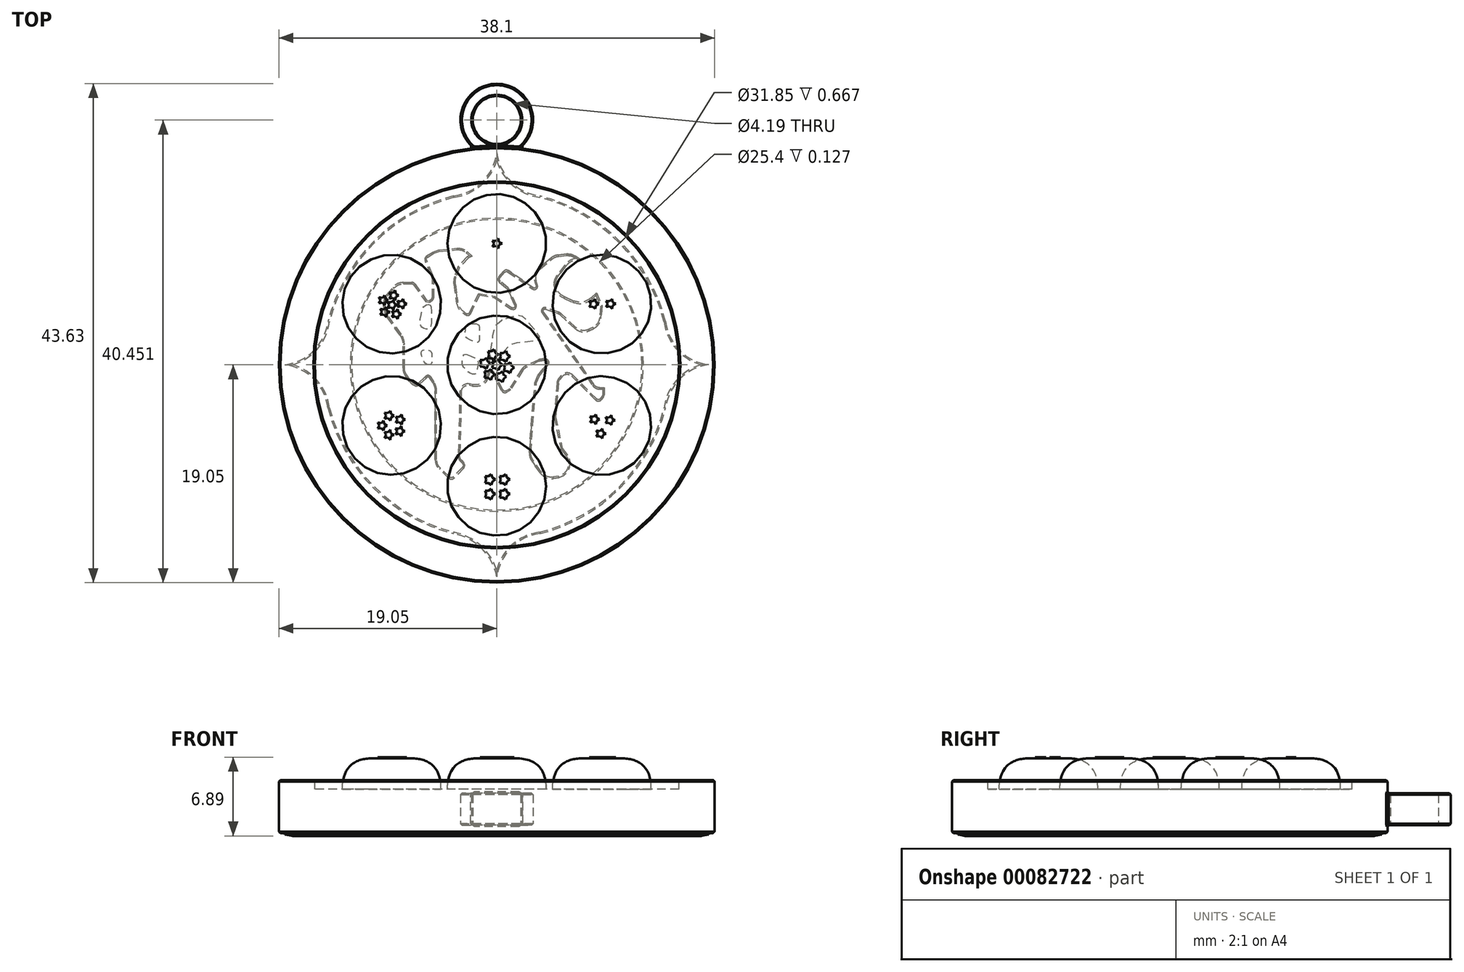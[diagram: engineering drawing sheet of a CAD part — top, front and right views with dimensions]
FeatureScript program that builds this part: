
annotation { "Feature Type Name" : "Feature", "Feature Type Description" : "" }
export const myFeature = defineFeature(function(context is Context, id is Id, definition is map)
    precondition{}
    {
        {
            var Q0;
            Q0=qCreatedBy(makeId("Top.planeOp"),FACE);
            var sketch = newSketch(context, id + "F0", { "sketchPlane" : qUnion([Q0])});
            skCircle(sketch, "E0", {"center": v(0, 0) * mm, "radius": 19.05 * mm});
            skCircle(sketch, "E1", {"center": v(0, 0) * mm, "radius": 15.92 * mm});
            skSolve(sketch);
        }
        {
            var Q0;
            Q0=qSketchRegion(id+"F0",true);
            var Q1;
            Q1=makeQuery(id+"F0.imprint","IMPRINT",FACE,{"disambiguationData":[TD([[makeQuery(id+"F0.imprint","IMPRINT",EDGE,{"derivedFrom":sQuery(id+"F0.wireOp",EDGE,"E1")}),1.0]])]});
            extrude(context, id + "F35", {"entities" : qUnion([Q0, Q1]), "oppositeDirection" : true, "depth" : 4.64 * mm});
        }
        {
            var Q0;
            Q0=makeQuery(id+"F0.imprint","IMPRINT",FACE,{"disambiguationData":[TD([[makeQuery(id+"F0.imprint","IMPRINT",EDGE,{"derivedFrom":sQuery(id+"F0.wireOp",EDGE,"E1")}),1.0]])]});
            extrude(context, id + "F36", {"entities" : qUnion([Q0]), "operationType" : NewBodyOperationType.REMOVE, "endBound" : BoundingType.SYMMETRIC, "oppositeDirection" : true, "depth" : 1.59 * mm});
        }
        {
            var Q0;
            Q0=qCreatedBy(makeId("Right.planeOp"),FACE);
            var sketch = newSketch(context, id + "F1", { "sketchPlane" : qUnion([Q0])});
            skLineSegment(sketch, "E2", {"start": v(0, -11.88) * mm, "end": v(0, 15.36) * mm});
            skLineSegment(sketch, "E3", {"start": v(14.05, 15.36) * mm, "end": v(14.05, -11.88) * mm});
            skSolve(sketch);
        }
        {
            var Q0;
            Q0=makeQuery(id+"F36.boolean.opBoolean","COPY",FACE,{"derivedFrom":makeQuery(id+"F36.opExtrude","CAP_FACE",FACE,{"disambiguationData":[OSD([sQuery(id+"F0.wireOp",EDGE,"E1")])],"isStart":false})});
            var sketch = newSketch(context, id + "F2", { "sketchPlane" : qUnion([Q0])});
            skCircle(sketch, "E4", {"center": v(0, 0) * mm, "radius": 4.32 * mm});
            skCircle(sketch, "E5", {"center": v(0, -10.61) * mm, "radius": 4.32 * mm});
            skSolve(sketch);
        }
        {
            var Q0;
            Q0=makeQuery(id+"F2.imprint","IMPRINT",FACE,{"disambiguationData":[TD([[makeQuery(id+"F2.imprint","IMPRINT",EDGE,{"derivedFrom":sQuery(id+"F2.wireOp",EDGE,"E5")}),1.0]])]});
            var Q1;
            Q1=sQuery(id+"F2.wireOp",EDGE,"E5");
            extrude(context, id + "F3", {"entities" : qUnion([Q0]), "surfaceEntities" : qUnion([Q1]), "depth" : 2.7 * mm});
        }
        {
            var Q0;
            Q0=makeQuery(id+"F3.opExtrude","SWEPT_BODY",BODY,{"disambiguationData":[OSD([sQuery(id+"F2.wireOp",EDGE,"E5")])]});
            var Q1;
            Q1=sQuery(id+"F1.wireOp",EDGE,"E2");
            circularPattern(context, id + "F4", {"entities" : qUnion([Q0]), "axis" : qUnion([Q1]), "angle" : 360 * degree, "instanceCount" : 6, "equalSpace" : true});
        }
        {
            var Q0;
            Q0=makeQuery(id+"F2.imprint","IMPRINT",FACE,{"disambiguationData":[TD([[makeQuery(id+"F2.imprint","IMPRINT",EDGE,{"derivedFrom":sQuery(id+"F2.wireOp",EDGE,"E4")}),1.0]])]});
            var Q1;
            Q1=sQuery(id+"F2.wireOp",EDGE,"E4");
            extrude(context, id + "F5", {"entities" : qUnion([Q0]), "surfaceEntities" : qUnion([Q1]), "depth" : 2.7 * mm});
        }
        {
            var Q0;
            Q0=qCreatedBy(makeId("Top.planeOp"),FACE);
            cPlane(context, id + "F6", {"entities" : qUnion([Q0]), "cplaneType" : CPlaneType.OFFSET, "offset" : 2.54 * mm, "oppositeDirection" : true, "width" : 152.4 * mm, "height" : 152.4 * mm});
        }
        {
            var Q0;
            Q0=qCreatedBy(id+"F6.planeOp",FACE);
            var sketch = newSketch(context, id + "F7", { "sketchPlane" : qUnion([Q0])});
            skCircle(sketch, "E6", {"center": v(0, 21.4) * mm, "radius": 3.18 * mm});
            skCircle(sketch, "E7", {"center": v(0, 21.4) * mm, "radius": 2.1 * mm});
            skSolve(sketch);
        }
        {
            var Q0;
            Q0=makeQuery(id+"F7.imprint","IMPRINT",FACE,{"disambiguationData":[TD([[makeQuery(id+"F7.imprint","IMPRINT",EDGE,{"derivedFrom":sQuery(id+"F7.wireOp",EDGE,"E6")}),1.0]])]});
            extrude(context, id + "F8", {"entities" : qUnion([Q0]), "operationType" : NewBodyOperationType.ADD, "endBound" : BoundingType.SYMMETRIC, "depth" : 2.8 * mm});
        }
        {
            var Q0;
            Q0=makeQuery(id+"F5.opExtrude","CAP_FACE",FACE,{"disambiguationData":[OSD([sQuery(id+"F2.wireOp",EDGE,"E4")])],"isStart":false});
            var sketch = newSketch(context, id + "F9", { "sketchPlane" : qUnion([Q0])});
            skCircle(sketch, "E8.cCircle", {"center": v(0, 0) * mm, "radius": 0.25 * mm, "construction": true});
            skLineSegment(sketch, "E8.0", {"start": v(-0.1, 0.3) * mm, "end": v(0.25, 0.18) * mm});
            skLineSegment(sketch, "E8.1", {"start": v(0.25, 0.18) * mm, "end": v(0.25, -0.18) * mm});
            skLineSegment(sketch, "E8.2", {"start": v(0.25, -0.18) * mm, "end": v(-0.1, -0.3) * mm});
            skLineSegment(sketch, "E8.3", {"start": v(-0.1, -0.3) * mm, "end": v(-0.31, 0) * mm});
            skLineSegment(sketch, "E8.4", {"start": v(-0.31, 0) * mm, "end": v(-0.1, 0.3) * mm});
            skPoint(sketch, "E8.0.midPoint", {"position": v(0.08, 0.24) * mm});
            skLineSegment(sketch, "E9", {"start": v(-0.1, 0.3) * mm, "end": v(0.15, 0.47) * mm});
            skLineSegment(sketch, "E10", {"start": v(0.15, 0.47) * mm, "end": v(0.25, 0.18) * mm});
            skLineSegment(sketch, "E11", {"start": v(0.25, 0.18) * mm, "end": v(0.5, 0) * mm});
            skPoint(sketch, "E11.endSnap0", {"position": v(0.25, 0) * mm});
            skLineSegment(sketch, "E12", {"start": v(0.5, 0) * mm, "end": v(0.25, -0.18) * mm});
            skLineSegment(sketch, "E13", {"start": v(-0.1, -0.3) * mm, "end": v(0.15, -0.47) * mm});
            skLineSegment(sketch, "E14", {"start": v(0.15, -0.47) * mm, "end": v(0.25, -0.18) * mm});
            skLineSegment(sketch, "E15", {"start": v(-0.31, 0) * mm, "end": v(-0.4, -0.3) * mm});
            skLineSegment(sketch, "E16", {"start": v(-0.4, -0.3) * mm, "end": v(-0.1, -0.3) * mm});
            skLineSegment(sketch, "E17", {"start": v(-0.31, 0) * mm, "end": v(-0.4, 0.3) * mm});
            skLineSegment(sketch, "E18", {"start": v(-0.4, 0.3) * mm, "end": v(-0.1, 0.3) * mm});
            skSolve(sketch);
        }
        {
            var Q0;
            Q0=makeQuery(id+"F9.imprint","IMPRINT",FACE,{"disambiguationData":[TD([[makeQuery(id+"F9.imprint","IMPRINT",EDGE,{"derivedFrom":sQuery(id+"F9.wireOp",EDGE,"E8.2")}),1.0]])]});
            var Q1;
            Q1=makeQuery(id+"F9.imprint","IMPRINT",FACE,{"disambiguationData":[TD([[makeQuery(id+"F9.imprint","IMPRINT",EDGE,{"derivedFrom":sQuery(id+"F9.wireOp",EDGE,"E8.3")}),1.0]])]});
            var Q2;
            Q2=makeQuery(id+"F9.imprint","IMPRINT",FACE,{"disambiguationData":[TD([[makeQuery(id+"F9.imprint","IMPRINT",EDGE,{"derivedFrom":sQuery(id+"F9.wireOp",EDGE,"E8.4")}),1.0]])]});
            var Q3;
            Q3=makeQuery(id+"F9.imprint","IMPRINT",FACE,{"disambiguationData":[TD([[makeQuery(id+"F9.imprint","IMPRINT",EDGE,{"derivedFrom":sQuery(id+"F9.wireOp",EDGE,"E8.0")}),1.0]])]});
            var Q4;
            Q4=makeQuery(id+"F9.imprint","IMPRINT",FACE,{"disambiguationData":[TD([[makeQuery(id+"F9.imprint","IMPRINT",EDGE,{"derivedFrom":sQuery(id+"F9.wireOp",EDGE,"E8.1")}),1.0]])]});
            var Q5;
            Q5=makeQuery(id+"F9.imprint","IMPRINT",FACE,{"disambiguationData":[TD([[makeQuery(id+"F9.imprint","IMPRINT",EDGE,{"derivedFrom":sQuery(id+"F9.wireOp",EDGE,"E8.0")}),-1.0]])]});
            var Q6;
            Q6=makeQuery(id+"F9.imprint","IMPRINT",FACE,{"disambiguationData":[TD([[makeQuery(id+"F9.imprint","IMPRINT",EDGE,{"derivedFrom":sQuery(id+"F9.wireOp",EDGE,"8882a5f5-dcc6-42d5-bc90-ea677534a3c9.0")}),1.0]])]});
            var Q7;
            Q7=makeQuery(id+"F9.imprint","IMPRINT",FACE,{"disambiguationData":[TD([[makeQuery(id+"F9.imprint","IMPRINT",EDGE,{"derivedFrom":sQuery(id+"F9.wireOp",EDGE,"8882a5f5-dcc6-42d5-bc90-ea677534a3c9.4")}),1.0]])]});
            var Q8;
            Q8=makeQuery(id+"F9.imprint","IMPRINT",FACE,{"disambiguationData":[TD([[makeQuery(id+"F9.imprint","IMPRINT",EDGE,{"derivedFrom":sQuery(id+"F9.wireOp",EDGE,"8882a5f5-dcc6-42d5-bc90-ea677534a3c9.3")}),1.0]])]});
            var Q9;
            Q9=makeQuery(id+"F9.imprint","IMPRINT",FACE,{"disambiguationData":[TD([[makeQuery(id+"F9.imprint","IMPRINT",EDGE,{"derivedFrom":sQuery(id+"F9.wireOp",EDGE,"8882a5f5-dcc6-42d5-bc90-ea677534a3c9.2")}),1.0]])]});
            var Q10;
            Q10=makeQuery(id+"F9.imprint","IMPRINT",FACE,{"disambiguationData":[TD([[makeQuery(id+"F9.imprint","IMPRINT",EDGE,{"derivedFrom":sQuery(id+"F9.wireOp",EDGE,"8882a5f5-dcc6-42d5-bc90-ea677534a3c9.1")}),1.0]])]});
            var Q11;
            Q11=makeQuery(id+"F9.imprint","IMPRINT",FACE,{"disambiguationData":[TD([[makeQuery(id+"F9.imprint","IMPRINT",EDGE,{"derivedFrom":sQuery(id+"F9.wireOp",EDGE,"8882a5f5-dcc6-42d5-bc90-ea677534a3c9.0")}),-1.0]])]});
            extrude(context, id + "F10", {"entities" : qUnion([Q0, Q1, Q2, Q3, Q4, Q5, Q6, Q7, Q8, Q9, Q10, Q11]), "operationType" : NewBodyOperationType.ADD, "depth" : 0.1 * mm});
        }
        {
            var Q0;
            Q0=qCreatedBy(makeId("Right.planeOp"),FACE);
            cPlane(context, id + "F11", {"entities" : qUnion([Q0]), "cplaneType" : CPlaneType.OFFSET, "offset" : 12.45 * mm, "oppositeDirection" : true, "width" : 152.4 * mm, "height" : 152.4 * mm});
        }
        {
            var Q0;
            Q0=qCreatedBy(makeId("Right.planeOp"),FACE);
            cPlane(context, id + "F12", {"entities" : qUnion([Q0]), "cplaneType" : CPlaneType.OFFSET, "offset" : 12.45 * mm, "width" : 152.4 * mm, "height" : 152.4 * mm});
        }
        {
            var Q0;
            Q0=makeQuery(id+"F5.opExtrude","CAP_EDGE",EDGE,{"disambiguationData":[OSD([sQuery(id+"F2.wireOp",EDGE,"E4")])],"isStart":false});
            var Q1;
            Q1=makeQuery(id+"F4.opPattern","COPY",EDGE,{"derivedFrom":makeQuery(id+"F3.opExtrude","CAP_EDGE",EDGE,{"disambiguationData":[OSD([sQuery(id+"F2.wireOp",EDGE,"E5")])],"isStart":false}),"instanceName":"3"});
            var Q2;
            Q2=makeQuery(id+"F4.opPattern","COPY",EDGE,{"derivedFrom":makeQuery(id+"F3.opExtrude","CAP_EDGE",EDGE,{"disambiguationData":[OSD([sQuery(id+"F2.wireOp",EDGE,"E5")])],"isStart":false}),"instanceName":"2"});
            var Q3;
            Q3=makeQuery(id+"F4.opPattern","COPY",EDGE,{"derivedFrom":makeQuery(id+"F3.opExtrude","CAP_EDGE",EDGE,{"disambiguationData":[OSD([sQuery(id+"F2.wireOp",EDGE,"E5")])],"isStart":false}),"instanceName":"1"});
            var Q4;
            Q4=makeQuery(id+"F4.opPattern","COPY",EDGE,{"derivedFrom":makeQuery(id+"F3.opExtrude","CAP_EDGE",EDGE,{"disambiguationData":[OSD([sQuery(id+"F2.wireOp",EDGE,"E5")])],"isStart":false}),"instanceName":"5"});
            var Q5;
            Q5=makeQuery(id+"F3.opExtrude","CAP_EDGE",EDGE,{"disambiguationData":[OSD([sQuery(id+"F2.wireOp",EDGE,"E5")])],"isStart":false});
            var Q6;
            Q6=makeQuery(id+"F4.opPattern","COPY",EDGE,{"derivedFrom":makeQuery(id+"F3.opExtrude","CAP_EDGE",EDGE,{"disambiguationData":[OSD([sQuery(id+"F2.wireOp",EDGE,"E5")])],"isStart":false}),"instanceName":"4"});
            fillet(context, id + "F13", {"entities" : qUnion([Q0, Q1, Q2, Q3, Q4, Q5, Q6]), "radius" : 2.7 * mm, "rho" : 0.5, "crossSection" : FilletCrossSection.CONIC, "allowEdgeOverflow" : false});
        }
        {
            var Q0;
            Q0=makeQuery(id+"F4.opPattern","COPY",FACE,{"derivedFrom":makeQuery(id+"F3.opExtrude","CAP_FACE",FACE,{"disambiguationData":[OSD([sQuery(id+"F2.wireOp",EDGE,"E5")])],"isStart":false}),"instanceName":"3"});
            var sketch = newSketch(context, id + "F14", { "sketchPlane" : qUnion([Q0])});
            skCircle(sketch, "E19.cCircle", {"center": v(0, 10.6) * mm, "radius": 0.19 * mm, "construction": true});
            skLineSegment(sketch, "E19.0", {"start": v(-0.07, 10.83) * mm, "end": v(0.19, 10.74) * mm});
            skLineSegment(sketch, "E19.1", {"start": v(0.19, 10.74) * mm, "end": v(0.19, 10.47) * mm});
            skLineSegment(sketch, "E19.2", {"start": v(0.19, 10.47) * mm, "end": v(-0.07, 10.39) * mm});
            skLineSegment(sketch, "E19.3", {"start": v(-0.07, 10.39) * mm, "end": v(-0.23, 10.6) * mm});
            skLineSegment(sketch, "E19.4", {"start": v(-0.23, 10.6) * mm, "end": v(-0.07, 10.83) * mm});
            skPoint(sketch, "E19.0.midPoint", {"position": v(0.06, 10.78) * mm});
            skLineSegment(sketch, "E20", {"start": v(-0.07, 10.83) * mm, "end": v(0.14, 11.04) * mm});
            skLineSegment(sketch, "E21", {"start": v(0.14, 11.04) * mm, "end": v(0.19, 10.74) * mm});
            skLineSegment(sketch, "E22", {"start": v(0.19, 10.74) * mm, "end": v(0.46, 10.6) * mm});
            skPoint(sketch, "E22.endSnap0", {"position": v(0.19, 10.6) * mm});
            skLineSegment(sketch, "E23", {"start": v(0.46, 10.6) * mm, "end": v(0.19, 10.47) * mm});
            skLineSegment(sketch, "E24", {"start": v(-0.07, 10.39) * mm, "end": v(0.14, 10.17) * mm});
            skLineSegment(sketch, "E25", {"start": v(0.14, 10.17) * mm, "end": v(0.19, 10.47) * mm});
            skLineSegment(sketch, "E26", {"start": v(-0.23, 10.6) * mm, "end": v(-0.37, 10.34) * mm});
            skLineSegment(sketch, "E27", {"start": v(-0.37, 10.34) * mm, "end": v(-0.07, 10.39) * mm});
            skLineSegment(sketch, "E28", {"start": v(-0.23, 10.6) * mm, "end": v(-0.37, 10.88) * mm});
            skLineSegment(sketch, "E29", {"start": v(-0.37, 10.88) * mm, "end": v(-0.07, 10.83) * mm});
            skSolve(sketch);
        }
        {
            var Q0;
            Q0=makeQuery(id+"F4.opPattern","COPY",FACE,{"derivedFrom":makeQuery(id+"F3.opExtrude","CAP_FACE",FACE,{"disambiguationData":[OSD([sQuery(id+"F2.wireOp",EDGE,"E5")])],"isStart":false}),"instanceName":"2"});
            var sketch = newSketch(context, id + "F15", { "sketchPlane" : qUnion([Q0])});
            skCircle(sketch, "E30.cCircle", {"center": v(8.46, 5.32) * mm, "radius": 0.19 * mm, "construction": true});
            skLineSegment(sketch, "E30.0", {"start": v(8.4, 5.54) * mm, "end": v(8.65, 5.46) * mm});
            skLineSegment(sketch, "E30.1", {"start": v(8.65, 5.46) * mm, "end": v(8.65, 5.19) * mm});
            skLineSegment(sketch, "E30.2", {"start": v(8.65, 5.19) * mm, "end": v(8.4, 5.1) * mm});
            skLineSegment(sketch, "E30.3", {"start": v(8.4, 5.1) * mm, "end": v(8.23, 5.32) * mm});
            skLineSegment(sketch, "E30.4", {"start": v(8.23, 5.32) * mm, "end": v(8.4, 5.54) * mm});
            skPoint(sketch, "E30.0.midPoint", {"position": v(8.52, 5.5) * mm});
            skLineSegment(sketch, "E31", {"start": v(8.4, 5.54) * mm, "end": v(8.6, 5.76) * mm});
            skLineSegment(sketch, "E32", {"start": v(8.6, 5.76) * mm, "end": v(8.65, 5.46) * mm});
            skLineSegment(sketch, "E33", {"start": v(8.65, 5.46) * mm, "end": v(8.92, 5.32) * mm});
            skPoint(sketch, "E33.endSnap0", {"position": v(8.65, 5.32) * mm});
            skLineSegment(sketch, "E34", {"start": v(8.92, 5.32) * mm, "end": v(8.65, 5.19) * mm});
            skLineSegment(sketch, "E35", {"start": v(8.4, 5.1) * mm, "end": v(8.6, 4.88) * mm});
            skLineSegment(sketch, "E36", {"start": v(8.6, 4.88) * mm, "end": v(8.65, 5.19) * mm});
            skLineSegment(sketch, "E37", {"start": v(8.23, 5.32) * mm, "end": v(8.1, 5.05) * mm});
            skLineSegment(sketch, "E38", {"start": v(8.1, 5.05) * mm, "end": v(8.4, 5.1) * mm});
            skLineSegment(sketch, "E39", {"start": v(8.23, 5.32) * mm, "end": v(8.1, 5.6) * mm});
            skLineSegment(sketch, "E40", {"start": v(8.1, 5.6) * mm, "end": v(8.4, 5.54) * mm});
            skCircle(sketch, "E41.cCircle", {"center": v(9.94, 5.33) * mm, "radius": 0.19 * mm, "construction": true});
            skLineSegment(sketch, "E41.0", {"start": v(9.87, 5.55) * mm, "end": v(10.12, 5.47) * mm});
            skLineSegment(sketch, "E41.1", {"start": v(10.12, 5.47) * mm, "end": v(10.12, 5.2) * mm});
            skLineSegment(sketch, "E41.2", {"start": v(10.12, 5.2) * mm, "end": v(9.87, 5.11) * mm});
            skLineSegment(sketch, "E41.3", {"start": v(9.87, 5.11) * mm, "end": v(9.7, 5.33) * mm});
            skLineSegment(sketch, "E41.4", {"start": v(9.7, 5.33) * mm, "end": v(9.87, 5.55) * mm});
            skPoint(sketch, "E41.0.midPoint", {"position": v(10, 5.5) * mm});
            skLineSegment(sketch, "E42", {"start": v(9.87, 5.55) * mm, "end": v(10.08, 5.77) * mm});
            skLineSegment(sketch, "E43", {"start": v(10.08, 5.77) * mm, "end": v(10.12, 5.47) * mm});
            skLineSegment(sketch, "E44", {"start": v(10.12, 5.47) * mm, "end": v(10.4, 5.33) * mm});
            skPoint(sketch, "E44.endSnap0", {"position": v(10.12, 5.33) * mm});
            skLineSegment(sketch, "E45", {"start": v(10.4, 5.33) * mm, "end": v(10.12, 5.2) * mm});
            skLineSegment(sketch, "E46", {"start": v(9.87, 5.11) * mm, "end": v(10.08, 4.9) * mm});
            skLineSegment(sketch, "E47", {"start": v(10.08, 4.9) * mm, "end": v(10.12, 5.2) * mm});
            skLineSegment(sketch, "E48", {"start": v(9.7, 5.33) * mm, "end": v(9.56, 5.06) * mm});
            skLineSegment(sketch, "E49", {"start": v(9.56, 5.06) * mm, "end": v(9.87, 5.11) * mm});
            skLineSegment(sketch, "E50", {"start": v(9.7, 5.33) * mm, "end": v(9.56, 5.6) * mm});
            skLineSegment(sketch, "E51", {"start": v(9.56, 5.6) * mm, "end": v(9.87, 5.55) * mm});
            skSolve(sketch);
        }
        {
            var Q0;
            Q0=makeQuery(id+"F4.opPattern","COPY",FACE,{"derivedFrom":makeQuery(id+"F3.opExtrude","CAP_FACE",FACE,{"disambiguationData":[OSD([sQuery(id+"F2.wireOp",EDGE,"E5")])],"isStart":false}),"instanceName":"1"});
            var sketch = newSketch(context, id + "F16", { "sketchPlane" : qUnion([Q0])});
            skCircle(sketch, "E52.cCircle", {"center": v(9.08, -6.01) * mm, "radius": 0.19 * mm, "construction": true});
            skLineSegment(sketch, "E52.0", {"start": v(9, -5.8) * mm, "end": v(9.27, -5.87) * mm});
            skLineSegment(sketch, "E52.1", {"start": v(9.27, -5.87) * mm, "end": v(9.27, -6.15) * mm});
            skLineSegment(sketch, "E52.2", {"start": v(9.27, -6.15) * mm, "end": v(9, -6.23) * mm});
            skLineSegment(sketch, "E52.3", {"start": v(9, -6.23) * mm, "end": v(8.85, -6.01) * mm});
            skLineSegment(sketch, "E52.4", {"start": v(8.85, -6.01) * mm, "end": v(9, -5.8) * mm});
            skPoint(sketch, "E52.0.midPoint", {"position": v(9.14, -5.83) * mm});
            skLineSegment(sketch, "E53", {"start": v(9, -5.8) * mm, "end": v(9.22, -5.57) * mm});
            skLineSegment(sketch, "E54", {"start": v(9.22, -5.57) * mm, "end": v(9.27, -5.87) * mm});
            skLineSegment(sketch, "E55", {"start": v(9.27, -5.87) * mm, "end": v(9.54, -6.01) * mm});
            skPoint(sketch, "E55.endSnap0", {"position": v(9.27, -6.01) * mm});
            skLineSegment(sketch, "E56", {"start": v(9.54, -6.01) * mm, "end": v(9.27, -6.15) * mm});
            skLineSegment(sketch, "E57", {"start": v(9, -6.23) * mm, "end": v(9.22, -6.45) * mm});
            skLineSegment(sketch, "E58", {"start": v(9.22, -6.45) * mm, "end": v(9.27, -6.15) * mm});
            skLineSegment(sketch, "E59", {"start": v(8.85, -6.01) * mm, "end": v(8.7, -6.28) * mm});
            skLineSegment(sketch, "E60", {"start": v(8.7, -6.28) * mm, "end": v(9, -6.23) * mm});
            skLineSegment(sketch, "E61", {"start": v(8.85, -6.01) * mm, "end": v(8.7, -5.74) * mm});
            skLineSegment(sketch, "E62", {"start": v(8.7, -5.74) * mm, "end": v(9, -5.8) * mm});
            skCircle(sketch, "E63.cCircle", {"center": v(8.54, -4.77) * mm, "radius": 0.19 * mm, "construction": true});
            skLineSegment(sketch, "E63.0", {"start": v(8.47, -4.55) * mm, "end": v(8.72, -4.63) * mm});
            skLineSegment(sketch, "E63.1", {"start": v(8.72, -4.63) * mm, "end": v(8.72, -4.9) * mm});
            skLineSegment(sketch, "E63.2", {"start": v(8.72, -4.9) * mm, "end": v(8.47, -4.99) * mm});
            skLineSegment(sketch, "E63.3", {"start": v(8.47, -4.99) * mm, "end": v(8.3, -4.77) * mm});
            skLineSegment(sketch, "E63.4", {"start": v(8.3, -4.77) * mm, "end": v(8.47, -4.55) * mm});
            skPoint(sketch, "E63.0.midPoint", {"position": v(8.6, -4.59) * mm});
            skLineSegment(sketch, "E64", {"start": v(8.47, -4.55) * mm, "end": v(8.68, -4.33) * mm});
            skLineSegment(sketch, "E65", {"start": v(8.68, -4.33) * mm, "end": v(8.72, -4.63) * mm});
            skLineSegment(sketch, "E66", {"start": v(8.72, -4.63) * mm, "end": v(9, -4.77) * mm});
            skPoint(sketch, "E66.endSnap0", {"position": v(8.72, -4.77) * mm});
            skLineSegment(sketch, "E67", {"start": v(9, -4.77) * mm, "end": v(8.72, -4.9) * mm});
            skLineSegment(sketch, "E68", {"start": v(8.47, -4.99) * mm, "end": v(8.68, -5.2) * mm});
            skLineSegment(sketch, "E69", {"start": v(8.68, -5.2) * mm, "end": v(8.72, -4.9) * mm});
            skLineSegment(sketch, "E70", {"start": v(8.3, -4.77) * mm, "end": v(8.17, -5.04) * mm});
            skLineSegment(sketch, "E71", {"start": v(8.17, -5.04) * mm, "end": v(8.47, -4.99) * mm});
            skLineSegment(sketch, "E72", {"start": v(8.3, -4.77) * mm, "end": v(8.17, -4.5) * mm});
            skLineSegment(sketch, "E73", {"start": v(8.17, -4.5) * mm, "end": v(8.47, -4.55) * mm});
            skCircle(sketch, "E74.cCircle", {"center": v(9.88, -4.84) * mm, "radius": 0.19 * mm, "construction": true});
            skLineSegment(sketch, "E74.0", {"start": v(9.8, -4.62) * mm, "end": v(10.07, -4.7) * mm});
            skLineSegment(sketch, "E74.1", {"start": v(10.07, -4.7) * mm, "end": v(10.07, -4.97) * mm});
            skLineSegment(sketch, "E74.2", {"start": v(10.07, -4.97) * mm, "end": v(9.8, -5.06) * mm});
            skLineSegment(sketch, "E74.3", {"start": v(9.8, -5.06) * mm, "end": v(9.65, -4.84) * mm});
            skLineSegment(sketch, "E74.4", {"start": v(9.65, -4.84) * mm, "end": v(9.8, -4.62) * mm});
            skPoint(sketch, "E74.0.midPoint", {"position": v(9.94, -4.66) * mm});
            skLineSegment(sketch, "E75", {"start": v(9.8, -4.62) * mm, "end": v(10.02, -4.4) * mm});
            skLineSegment(sketch, "E76", {"start": v(10.02, -4.4) * mm, "end": v(10.07, -4.7) * mm});
            skLineSegment(sketch, "E77", {"start": v(10.07, -4.7) * mm, "end": v(10.34, -4.84) * mm});
            skPoint(sketch, "E77.endSnap0", {"position": v(10.07, -4.84) * mm});
            skLineSegment(sketch, "E78", {"start": v(10.34, -4.84) * mm, "end": v(10.07, -4.97) * mm});
            skLineSegment(sketch, "E79", {"start": v(9.8, -5.06) * mm, "end": v(10.02, -5.28) * mm});
            skLineSegment(sketch, "E80", {"start": v(10.02, -5.28) * mm, "end": v(10.07, -4.97) * mm});
            skLineSegment(sketch, "E81", {"start": v(9.65, -4.84) * mm, "end": v(9.5, -5.1) * mm});
            skLineSegment(sketch, "E82", {"start": v(9.5, -5.1) * mm, "end": v(9.8, -5.06) * mm});
            skLineSegment(sketch, "E83", {"start": v(9.65, -4.84) * mm, "end": v(9.5, -4.57) * mm});
            skLineSegment(sketch, "E84", {"start": v(9.5, -4.57) * mm, "end": v(9.8, -4.62) * mm});
            skSolve(sketch);
        }
        {
            var Q0;
            Q0=makeQuery(id+"F3.opExtrude","CAP_FACE",FACE,{"disambiguationData":[OSD([sQuery(id+"F2.wireOp",EDGE,"E5")])],"isStart":false});
            var sketch = newSketch(context, id + "F17", { "sketchPlane" : qUnion([Q0])});
            skLineSegment(sketch, "E85.bottom", {"start": v(-0.62, -10.04) * mm, "end": v(0.65, -10.04) * mm});
            skLineSegment(sketch, "E85.top", {"start": v(-0.62, -11.3) * mm, "end": v(0.65, -11.3) * mm});
            skLineSegment(sketch, "E85.left", {"start": v(-0.62, -10.04) * mm, "end": v(-0.62, -11.3) * mm});
            skLineSegment(sketch, "E85.right", {"start": v(0.65, -10.04) * mm, "end": v(0.65, -11.3) * mm});
            skPoint(sketch, "E85.middle", {"position": v(0.01, -10.67) * mm});
            skCircle(sketch, "E86.cCircle", {"center": v(0.65, -10.04) * mm, "radius": 0.25 * mm, "construction": true});
            skLineSegment(sketch, "E86.0", {"start": v(0.55, -9.74) * mm, "end": v(0.9, -9.85) * mm});
            skLineSegment(sketch, "E86.1", {"start": v(0.9, -9.85) * mm, "end": v(0.9, -10.22) * mm});
            skLineSegment(sketch, "E86.2", {"start": v(0.9, -10.22) * mm, "end": v(0.55, -10.33) * mm});
            skLineSegment(sketch, "E86.3", {"start": v(0.55, -10.33) * mm, "end": v(0.34, -10.04) * mm});
            skLineSegment(sketch, "E86.4", {"start": v(0.34, -10.04) * mm, "end": v(0.55, -9.74) * mm});
            skPoint(sketch, "E86.0.midPoint", {"position": v(0.73, -9.8) * mm});
            skLineSegment(sketch, "E87", {"start": v(0.55, -9.74) * mm, "end": v(0.8, -9.56) * mm});
            skLineSegment(sketch, "E88", {"start": v(0.8, -9.56) * mm, "end": v(0.9, -9.85) * mm});
            skLineSegment(sketch, "E89", {"start": v(0.9, -9.85) * mm, "end": v(1.15, -10.04) * mm});
            skPoint(sketch, "E89.endSnap0", {"position": v(0.9, -10.04) * mm});
            skLineSegment(sketch, "E90", {"start": v(1.15, -10.04) * mm, "end": v(0.9, -10.22) * mm});
            skLineSegment(sketch, "E91", {"start": v(0.55, -10.33) * mm, "end": v(0.8, -10.5) * mm});
            skLineSegment(sketch, "E92", {"start": v(0.8, -10.5) * mm, "end": v(0.9, -10.22) * mm});
            skLineSegment(sketch, "E93", {"start": v(0.34, -10.04) * mm, "end": v(0.25, -10.33) * mm});
            skLineSegment(sketch, "E94", {"start": v(0.25, -10.33) * mm, "end": v(0.55, -10.33) * mm});
            skLineSegment(sketch, "E95", {"start": v(0.34, -10.04) * mm, "end": v(0.25, -9.74) * mm});
            skLineSegment(sketch, "E96", {"start": v(0.25, -9.74) * mm, "end": v(0.55, -9.74) * mm});
            skCircle(sketch, "E97.cCircle", {"center": v(-0.62, -10.04) * mm, "radius": 0.25 * mm, "construction": true});
            skLineSegment(sketch, "E97.0", {"start": v(-0.72, -9.74) * mm, "end": v(-0.37, -9.85) * mm});
            skLineSegment(sketch, "E97.1", {"start": v(-0.37, -9.85) * mm, "end": v(-0.37, -10.22) * mm});
            skLineSegment(sketch, "E97.2", {"start": v(-0.37, -10.22) * mm, "end": v(-0.72, -10.33) * mm});
            skLineSegment(sketch, "E97.3", {"start": v(-0.72, -10.33) * mm, "end": v(-0.93, -10.04) * mm});
            skLineSegment(sketch, "E97.4", {"start": v(-0.93, -10.04) * mm, "end": v(-0.72, -9.74) * mm});
            skPoint(sketch, "E97.0.midPoint", {"position": v(-0.54, -9.8) * mm});
            skLineSegment(sketch, "E98", {"start": v(-0.72, -9.74) * mm, "end": v(-0.47, -9.56) * mm});
            skLineSegment(sketch, "E99", {"start": v(-0.47, -9.56) * mm, "end": v(-0.37, -9.85) * mm});
            skLineSegment(sketch, "E100", {"start": v(-0.37, -9.85) * mm, "end": v(-0.12, -10.04) * mm});
            skPoint(sketch, "E100.endSnap0", {"position": v(-0.37, -10.04) * mm});
            skLineSegment(sketch, "E101", {"start": v(-0.12, -10.04) * mm, "end": v(-0.37, -10.22) * mm});
            skLineSegment(sketch, "E102", {"start": v(-0.72, -10.33) * mm, "end": v(-0.47, -10.5) * mm});
            skLineSegment(sketch, "E103", {"start": v(-0.47, -10.5) * mm, "end": v(-0.37, -10.22) * mm});
            skLineSegment(sketch, "E104", {"start": v(-0.93, -10.04) * mm, "end": v(-1.02, -10.33) * mm});
            skLineSegment(sketch, "E105", {"start": v(-1.02, -10.33) * mm, "end": v(-0.72, -10.33) * mm});
            skLineSegment(sketch, "E106", {"start": v(-0.93, -10.04) * mm, "end": v(-1.02, -9.74) * mm});
            skLineSegment(sketch, "E107", {"start": v(-1.02, -9.74) * mm, "end": v(-0.72, -9.74) * mm});
            skCircle(sketch, "E108.cCircle", {"center": v(-0.62, -11.3) * mm, "radius": 0.25 * mm, "construction": true});
            skLineSegment(sketch, "E108.0", {"start": v(-0.72, -11.01) * mm, "end": v(-0.37, -11.12) * mm});
            skLineSegment(sketch, "E108.1", {"start": v(-0.37, -11.12) * mm, "end": v(-0.37, -11.49) * mm});
            skLineSegment(sketch, "E108.2", {"start": v(-0.37, -11.49) * mm, "end": v(-0.72, -11.6) * mm});
            skLineSegment(sketch, "E108.3", {"start": v(-0.72, -11.6) * mm, "end": v(-0.93, -11.3) * mm});
            skLineSegment(sketch, "E108.4", {"start": v(-0.93, -11.3) * mm, "end": v(-0.72, -11.01) * mm});
            skPoint(sketch, "E108.0.midPoint", {"position": v(-0.54, -11.07) * mm});
            skLineSegment(sketch, "E109", {"start": v(-0.72, -11.01) * mm, "end": v(-0.47, -10.83) * mm});
            skLineSegment(sketch, "E110", {"start": v(-0.47, -10.83) * mm, "end": v(-0.37, -11.12) * mm});
            skLineSegment(sketch, "E111", {"start": v(-0.37, -11.12) * mm, "end": v(-0.12, -11.3) * mm});
            skPoint(sketch, "E111.endSnap0", {"position": v(-0.37, -11.3) * mm});
            skLineSegment(sketch, "E112", {"start": v(-0.12, -11.3) * mm, "end": v(-0.37, -11.49) * mm});
            skLineSegment(sketch, "E113", {"start": v(-0.72, -11.6) * mm, "end": v(-0.47, -11.78) * mm});
            skLineSegment(sketch, "E114", {"start": v(-0.47, -11.78) * mm, "end": v(-0.37, -11.49) * mm});
            skLineSegment(sketch, "E115", {"start": v(-0.93, -11.3) * mm, "end": v(-1.02, -11.6) * mm});
            skLineSegment(sketch, "E116", {"start": v(-1.02, -11.6) * mm, "end": v(-0.72, -11.6) * mm});
            skLineSegment(sketch, "E117", {"start": v(-0.93, -11.3) * mm, "end": v(-1.02, -11.01) * mm});
            skLineSegment(sketch, "E118", {"start": v(-1.02, -11.01) * mm, "end": v(-0.72, -11.01) * mm});
            skCircle(sketch, "E119.cCircle", {"center": v(0.65, -11.3) * mm, "radius": 0.25 * mm, "construction": true});
            skLineSegment(sketch, "E119.0", {"start": v(0.55, -11.01) * mm, "end": v(0.9, -11.12) * mm});
            skLineSegment(sketch, "E119.1", {"start": v(0.9, -11.12) * mm, "end": v(0.9, -11.49) * mm});
            skLineSegment(sketch, "E119.2", {"start": v(0.9, -11.49) * mm, "end": v(0.55, -11.6) * mm});
            skLineSegment(sketch, "E119.3", {"start": v(0.55, -11.6) * mm, "end": v(0.34, -11.3) * mm});
            skLineSegment(sketch, "E119.4", {"start": v(0.34, -11.3) * mm, "end": v(0.55, -11.01) * mm});
            skPoint(sketch, "E119.0.midPoint", {"position": v(0.73, -11.07) * mm});
            skLineSegment(sketch, "E120", {"start": v(0.55, -11.01) * mm, "end": v(0.8, -10.83) * mm});
            skLineSegment(sketch, "E121", {"start": v(0.8, -10.83) * mm, "end": v(0.9, -11.12) * mm});
            skLineSegment(sketch, "E122", {"start": v(0.9, -11.12) * mm, "end": v(1.15, -11.3) * mm});
            skPoint(sketch, "E122.endSnap0", {"position": v(0.9, -11.3) * mm});
            skLineSegment(sketch, "E123", {"start": v(1.15, -11.3) * mm, "end": v(0.9, -11.49) * mm});
            skLineSegment(sketch, "E124", {"start": v(0.55, -11.6) * mm, "end": v(0.8, -11.78) * mm});
            skLineSegment(sketch, "E125", {"start": v(0.8, -11.78) * mm, "end": v(0.9, -11.49) * mm});
            skLineSegment(sketch, "E126", {"start": v(0.34, -11.3) * mm, "end": v(0.25, -11.6) * mm});
            skLineSegment(sketch, "E127", {"start": v(0.25, -11.6) * mm, "end": v(0.55, -11.6) * mm});
            skLineSegment(sketch, "E128", {"start": v(0.34, -11.3) * mm, "end": v(0.25, -11.01) * mm});
            skLineSegment(sketch, "E129", {"start": v(0.25, -11.01) * mm, "end": v(0.55, -11.01) * mm});
            skSolve(sketch);
        }
        {
            var Q0;
            Q0=makeQuery(id+"F4.opPattern","COPY",FACE,{"derivedFrom":makeQuery(id+"F3.opExtrude","CAP_FACE",FACE,{"disambiguationData":[OSD([sQuery(id+"F2.wireOp",EDGE,"E5")])],"isStart":false}),"instanceName":"5"});
            var sketch = newSketch(context, id + "F18", { "sketchPlane" : qUnion([Q0])});
            skCircle(sketch, "E130.cCircle", {"center": v(-9.17, -5.27) * mm, "radius": 0.7 * mm, "construction": true});
            skLineSegment(sketch, "E130.0", {"start": v(-8.47, -4.76) * mm, "end": v(-8.47, -5.78) * mm});
            skLineSegment(sketch, "E130.1", {"start": v(-8.47, -5.78) * mm, "end": v(-9.44, -6.1) * mm});
            skLineSegment(sketch, "E130.2", {"start": v(-9.44, -6.1) * mm, "end": v(-10.04, -5.27) * mm});
            skLineSegment(sketch, "E130.3", {"start": v(-10.04, -5.27) * mm, "end": v(-9.44, -4.45) * mm});
            skLineSegment(sketch, "E130.4", {"start": v(-9.44, -4.45) * mm, "end": v(-8.47, -4.76) * mm});
            skPoint(sketch, "E130.0.midPoint", {"position": v(-8.47, -5.27) * mm});
            skCircle(sketch, "E131.cCircle", {"center": v(-9.44, -4.45) * mm, "radius": 0.19 * mm, "construction": true});
            skLineSegment(sketch, "E131.0", {"start": v(-9.51, -4.23) * mm, "end": v(-9.25, -4.31) * mm});
            skLineSegment(sketch, "E131.1", {"start": v(-9.25, -4.31) * mm, "end": v(-9.25, -4.58) * mm});
            skLineSegment(sketch, "E131.2", {"start": v(-9.25, -4.58) * mm, "end": v(-9.51, -4.67) * mm});
            skLineSegment(sketch, "E131.3", {"start": v(-9.51, -4.67) * mm, "end": v(-9.67, -4.45) * mm});
            skLineSegment(sketch, "E131.4", {"start": v(-9.67, -4.45) * mm, "end": v(-9.51, -4.23) * mm});
            skPoint(sketch, "E131.0.midPoint", {"position": v(-9.38, -4.27) * mm});
            skLineSegment(sketch, "E132", {"start": v(-9.51, -4.23) * mm, "end": v(-9.3, -4.01) * mm});
            skLineSegment(sketch, "E133", {"start": v(-9.3, -4.01) * mm, "end": v(-9.25, -4.31) * mm});
            skLineSegment(sketch, "E134", {"start": v(-9.25, -4.31) * mm, "end": v(-8.98, -4.45) * mm});
            skPoint(sketch, "E134.endSnap0", {"position": v(-9.25, -4.45) * mm});
            skLineSegment(sketch, "E135", {"start": v(-8.98, -4.45) * mm, "end": v(-9.25, -4.58) * mm});
            skLineSegment(sketch, "E136", {"start": v(-9.51, -4.67) * mm, "end": v(-9.3, -4.89) * mm});
            skLineSegment(sketch, "E137", {"start": v(-9.3, -4.89) * mm, "end": v(-9.25, -4.58) * mm});
            skLineSegment(sketch, "E138", {"start": v(-9.67, -4.45) * mm, "end": v(-9.81, -4.72) * mm});
            skLineSegment(sketch, "E139", {"start": v(-9.81, -4.72) * mm, "end": v(-9.51, -4.67) * mm});
            skLineSegment(sketch, "E140", {"start": v(-9.67, -4.45) * mm, "end": v(-9.81, -4.18) * mm});
            skLineSegment(sketch, "E141", {"start": v(-9.81, -4.18) * mm, "end": v(-9.51, -4.23) * mm});
            skCircle(sketch, "E142.cCircle", {"center": v(-8.46, -4.79) * mm, "radius": 0.19 * mm, "construction": true});
            skLineSegment(sketch, "E142.0", {"start": v(-8.53, -4.57) * mm, "end": v(-8.27, -4.65) * mm});
            skLineSegment(sketch, "E142.1", {"start": v(-8.27, -4.65) * mm, "end": v(-8.27, -4.92) * mm});
            skLineSegment(sketch, "E142.2", {"start": v(-8.27, -4.92) * mm, "end": v(-8.53, -5) * mm});
            skLineSegment(sketch, "E142.3", {"start": v(-8.53, -5) * mm, "end": v(-8.69, -4.79) * mm});
            skLineSegment(sketch, "E142.4", {"start": v(-8.69, -4.79) * mm, "end": v(-8.53, -4.57) * mm});
            skPoint(sketch, "E142.0.midPoint", {"position": v(-8.4, -4.61) * mm});
            skLineSegment(sketch, "E143", {"start": v(-8.53, -4.57) * mm, "end": v(-8.32, -4.35) * mm});
            skLineSegment(sketch, "E144", {"start": v(-8.32, -4.35) * mm, "end": v(-8.27, -4.65) * mm});
            skLineSegment(sketch, "E145", {"start": v(-8.27, -4.65) * mm, "end": v(-8, -4.79) * mm});
            skPoint(sketch, "E145.endSnap0", {"position": v(-8.27, -4.79) * mm});
            skLineSegment(sketch, "E146", {"start": v(-8, -4.79) * mm, "end": v(-8.27, -4.92) * mm});
            skLineSegment(sketch, "E147", {"start": v(-8.53, -5) * mm, "end": v(-8.32, -5.22) * mm});
            skLineSegment(sketch, "E148", {"start": v(-8.32, -5.22) * mm, "end": v(-8.27, -4.92) * mm});
            skLineSegment(sketch, "E149", {"start": v(-8.69, -4.79) * mm, "end": v(-8.83, -5.06) * mm});
            skLineSegment(sketch, "E150", {"start": v(-8.83, -5.06) * mm, "end": v(-8.53, -5) * mm});
            skLineSegment(sketch, "E151", {"start": v(-8.69, -4.79) * mm, "end": v(-8.83, -4.52) * mm});
            skLineSegment(sketch, "E152", {"start": v(-8.83, -4.52) * mm, "end": v(-8.53, -4.57) * mm});
            skCircle(sketch, "E153.cCircle", {"center": v(-8.48, -5.8) * mm, "radius": 0.19 * mm, "construction": true});
            skLineSegment(sketch, "E153.0", {"start": v(-8.56, -5.58) * mm, "end": v(-8.3, -5.67) * mm});
            skLineSegment(sketch, "E153.1", {"start": v(-8.3, -5.67) * mm, "end": v(-8.3, -5.94) * mm});
            skLineSegment(sketch, "E153.2", {"start": v(-8.3, -5.94) * mm, "end": v(-8.56, -6.02) * mm});
            skLineSegment(sketch, "E153.3", {"start": v(-8.56, -6.02) * mm, "end": v(-8.71, -5.8) * mm});
            skLineSegment(sketch, "E153.4", {"start": v(-8.71, -5.8) * mm, "end": v(-8.56, -5.58) * mm});
            skPoint(sketch, "E153.0.midPoint", {"position": v(-8.43, -5.62) * mm});
            skLineSegment(sketch, "E154", {"start": v(-8.56, -5.58) * mm, "end": v(-8.34, -5.37) * mm});
            skLineSegment(sketch, "E155", {"start": v(-8.34, -5.37) * mm, "end": v(-8.3, -5.67) * mm});
            skLineSegment(sketch, "E156", {"start": v(-8.3, -5.67) * mm, "end": v(-8.02, -5.8) * mm});
            skPoint(sketch, "E156.endSnap0", {"position": v(-8.3, -5.8) * mm});
            skLineSegment(sketch, "E157", {"start": v(-8.02, -5.8) * mm, "end": v(-8.3, -5.94) * mm});
            skLineSegment(sketch, "E158", {"start": v(-8.56, -6.02) * mm, "end": v(-8.34, -6.24) * mm});
            skLineSegment(sketch, "E159", {"start": v(-8.34, -6.24) * mm, "end": v(-8.3, -5.94) * mm});
            skLineSegment(sketch, "E160", {"start": v(-8.71, -5.8) * mm, "end": v(-8.86, -6.07) * mm});
            skLineSegment(sketch, "E161", {"start": v(-8.86, -6.07) * mm, "end": v(-8.56, -6.02) * mm});
            skLineSegment(sketch, "E162", {"start": v(-8.71, -5.8) * mm, "end": v(-8.86, -5.53) * mm});
            skLineSegment(sketch, "E163", {"start": v(-8.86, -5.53) * mm, "end": v(-8.56, -5.58) * mm});
            skCircle(sketch, "E164.cCircle", {"center": v(-9.45, -6.12) * mm, "radius": 0.19 * mm, "construction": true});
            skLineSegment(sketch, "E164.0", {"start": v(-9.52, -5.9) * mm, "end": v(-9.26, -5.99) * mm});
            skLineSegment(sketch, "E164.1", {"start": v(-9.26, -5.99) * mm, "end": v(-9.26, -6.26) * mm});
            skLineSegment(sketch, "E164.2", {"start": v(-9.26, -6.26) * mm, "end": v(-9.52, -6.34) * mm});
            skLineSegment(sketch, "E164.3", {"start": v(-9.52, -6.34) * mm, "end": v(-9.68, -6.12) * mm});
            skLineSegment(sketch, "E164.4", {"start": v(-9.68, -6.12) * mm, "end": v(-9.52, -5.9) * mm});
            skPoint(sketch, "E164.0.midPoint", {"position": v(-9.4, -5.94) * mm});
            skLineSegment(sketch, "E165", {"start": v(-9.52, -5.9) * mm, "end": v(-9.3, -5.68) * mm});
            skLineSegment(sketch, "E166", {"start": v(-9.3, -5.68) * mm, "end": v(-9.26, -5.99) * mm});
            skLineSegment(sketch, "E167", {"start": v(-9.26, -5.99) * mm, "end": v(-8.99, -6.12) * mm});
            skPoint(sketch, "E167.endSnap0", {"position": v(-9.26, -6.12) * mm});
            skLineSegment(sketch, "E168", {"start": v(-8.99, -6.12) * mm, "end": v(-9.26, -6.26) * mm});
            skLineSegment(sketch, "E169", {"start": v(-9.52, -6.34) * mm, "end": v(-9.3, -6.56) * mm});
            skLineSegment(sketch, "E170", {"start": v(-9.3, -6.56) * mm, "end": v(-9.26, -6.26) * mm});
            skLineSegment(sketch, "E171", {"start": v(-9.68, -6.12) * mm, "end": v(-9.82, -6.4) * mm});
            skLineSegment(sketch, "E172", {"start": v(-9.82, -6.4) * mm, "end": v(-9.52, -6.34) * mm});
            skLineSegment(sketch, "E173", {"start": v(-9.68, -6.12) * mm, "end": v(-9.82, -5.85) * mm});
            skLineSegment(sketch, "E174", {"start": v(-9.82, -5.85) * mm, "end": v(-9.52, -5.9) * mm});
            skCircle(sketch, "E175.cCircle", {"center": v(-10.04, -5.31) * mm, "radius": 0.19 * mm, "construction": true});
            skLineSegment(sketch, "E175.0", {"start": v(-10.11, -5.1) * mm, "end": v(-9.85, -5.18) * mm});
            skLineSegment(sketch, "E175.1", {"start": v(-9.85, -5.18) * mm, "end": v(-9.85, -5.45) * mm});
            skLineSegment(sketch, "E175.2", {"start": v(-9.85, -5.45) * mm, "end": v(-10.11, -5.53) * mm});
            skLineSegment(sketch, "E175.3", {"start": v(-10.11, -5.53) * mm, "end": v(-10.27, -5.31) * mm});
            skLineSegment(sketch, "E175.4", {"start": v(-10.27, -5.31) * mm, "end": v(-10.11, -5.1) * mm});
            skPoint(sketch, "E175.0.midPoint", {"position": v(-9.98, -5.14) * mm});
            skLineSegment(sketch, "E176", {"start": v(-10.11, -5.1) * mm, "end": v(-9.9, -4.88) * mm});
            skLineSegment(sketch, "E177", {"start": v(-9.9, -4.88) * mm, "end": v(-9.85, -5.18) * mm});
            skLineSegment(sketch, "E178", {"start": v(-9.85, -5.18) * mm, "end": v(-9.58, -5.31) * mm});
            skPoint(sketch, "E178.endSnap0", {"position": v(-9.85, -5.31) * mm});
            skLineSegment(sketch, "E179", {"start": v(-9.58, -5.31) * mm, "end": v(-9.85, -5.45) * mm});
            skLineSegment(sketch, "E180", {"start": v(-10.11, -5.53) * mm, "end": v(-9.9, -5.75) * mm});
            skLineSegment(sketch, "E181", {"start": v(-9.9, -5.75) * mm, "end": v(-9.85, -5.45) * mm});
            skLineSegment(sketch, "E182", {"start": v(-10.27, -5.31) * mm, "end": v(-10.41, -5.58) * mm});
            skLineSegment(sketch, "E183", {"start": v(-10.41, -5.58) * mm, "end": v(-10.11, -5.53) * mm});
            skLineSegment(sketch, "E184", {"start": v(-10.27, -5.31) * mm, "end": v(-10.41, -5.04) * mm});
            skLineSegment(sketch, "E185", {"start": v(-10.41, -5.04) * mm, "end": v(-10.11, -5.1) * mm});
            skSolve(sketch);
        }
        {
            var Q0;
            Q0=makeQuery(id+"F4.opPattern","COPY",FACE,{"derivedFrom":makeQuery(id+"F3.opExtrude","CAP_FACE",FACE,{"disambiguationData":[OSD([sQuery(id+"F2.wireOp",EDGE,"E5")])],"isStart":false}),"instanceName":"4"});
            var sketch = newSketch(context, id + "F19", { "sketchPlane" : qUnion([Q0])});
            skCircle(sketch, "E186.cCircle", {"center": v(-9.18, 5.24) * mm, "radius": 0.19 * mm, "construction": true});
            skLineSegment(sketch, "E186.0", {"start": v(-9.25, 5.46) * mm, "end": v(-8.99, 5.37) * mm});
            skLineSegment(sketch, "E186.1", {"start": v(-8.99, 5.37) * mm, "end": v(-8.99, 5.1) * mm});
            skLineSegment(sketch, "E186.2", {"start": v(-8.99, 5.1) * mm, "end": v(-9.25, 5.02) * mm});
            skLineSegment(sketch, "E186.3", {"start": v(-9.25, 5.02) * mm, "end": v(-9.4, 5.24) * mm});
            skLineSegment(sketch, "E186.4", {"start": v(-9.4, 5.24) * mm, "end": v(-9.25, 5.46) * mm});
            skPoint(sketch, "E186.0.midPoint", {"position": v(-9.12, 5.41) * mm});
            skLineSegment(sketch, "E187", {"start": v(-9.25, 5.46) * mm, "end": v(-9.03, 5.67) * mm});
            skLineSegment(sketch, "E188", {"start": v(-9.03, 5.67) * mm, "end": v(-8.99, 5.37) * mm});
            skLineSegment(sketch, "E189", {"start": v(-8.99, 5.37) * mm, "end": v(-8.72, 5.24) * mm});
            skPoint(sketch, "E189.endSnap0", {"position": v(-8.99, 5.24) * mm});
            skLineSegment(sketch, "E190", {"start": v(-8.72, 5.24) * mm, "end": v(-8.99, 5.1) * mm});
            skLineSegment(sketch, "E191", {"start": v(-9.25, 5.02) * mm, "end": v(-9.03, 4.8) * mm});
            skLineSegment(sketch, "E192", {"start": v(-9.03, 4.8) * mm, "end": v(-8.99, 5.1) * mm});
            skLineSegment(sketch, "E193", {"start": v(-9.4, 5.24) * mm, "end": v(-9.55, 4.97) * mm});
            skLineSegment(sketch, "E194", {"start": v(-9.55, 4.97) * mm, "end": v(-9.25, 5.02) * mm});
            skLineSegment(sketch, "E195", {"start": v(-9.4, 5.24) * mm, "end": v(-9.55, 5.5) * mm});
            skLineSegment(sketch, "E196", {"start": v(-9.55, 5.5) * mm, "end": v(-9.25, 5.46) * mm});
            skCircle(sketch, "E197.cCircle", {"center": v(-9.18, 5.24) * mm, "radius": 0.7 * mm, "construction": true});
            skLineSegment(sketch, "E197.0", {"start": v(-9.93, 5.65) * mm, "end": v(-9.01, 6.09) * mm});
            skLineSegment(sketch, "E197.1", {"start": v(-9.01, 6.09) * mm, "end": v(-8.32, 5.35) * mm});
            skLineSegment(sketch, "E197.2", {"start": v(-8.32, 5.35) * mm, "end": v(-8.8, 4.46) * mm});
            skLineSegment(sketch, "E197.3", {"start": v(-8.8, 4.46) * mm, "end": v(-9.8, 4.64) * mm});
            skLineSegment(sketch, "E197.4", {"start": v(-9.8, 4.64) * mm, "end": v(-9.93, 5.65) * mm});
            skPoint(sketch, "E197.0.midPoint", {"position": v(-9.47, 5.87) * mm});
            skCircle(sketch, "E198.cCircle", {"center": v(-9.03, 6.07) * mm, "radius": 0.19 * mm, "construction": true});
            skLineSegment(sketch, "E198.0", {"start": v(-9.1, 6.3) * mm, "end": v(-8.84, 6.2) * mm});
            skLineSegment(sketch, "E198.1", {"start": v(-8.84, 6.2) * mm, "end": v(-8.84, 5.94) * mm});
            skLineSegment(sketch, "E198.2", {"start": v(-8.84, 5.94) * mm, "end": v(-9.1, 5.85) * mm});
            skLineSegment(sketch, "E198.3", {"start": v(-9.1, 5.85) * mm, "end": v(-9.26, 6.07) * mm});
            skLineSegment(sketch, "E198.4", {"start": v(-9.26, 6.07) * mm, "end": v(-9.1, 6.3) * mm});
            skPoint(sketch, "E198.0.midPoint", {"position": v(-8.97, 6.25) * mm});
            skLineSegment(sketch, "E199", {"start": v(-9.1, 6.3) * mm, "end": v(-8.88, 6.5) * mm});
            skLineSegment(sketch, "E200", {"start": v(-8.88, 6.5) * mm, "end": v(-8.84, 6.2) * mm});
            skLineSegment(sketch, "E201", {"start": v(-8.84, 6.2) * mm, "end": v(-8.57, 6.07) * mm});
            skPoint(sketch, "E201.endSnap0", {"position": v(-8.84, 6.07) * mm});
            skLineSegment(sketch, "E202", {"start": v(-8.57, 6.07) * mm, "end": v(-8.84, 5.94) * mm});
            skLineSegment(sketch, "E203", {"start": v(-9.1, 5.85) * mm, "end": v(-8.88, 5.64) * mm});
            skLineSegment(sketch, "E204", {"start": v(-8.88, 5.64) * mm, "end": v(-8.84, 5.94) * mm});
            skLineSegment(sketch, "E205", {"start": v(-9.26, 6.07) * mm, "end": v(-9.4, 5.8) * mm});
            skLineSegment(sketch, "E206", {"start": v(-9.4, 5.8) * mm, "end": v(-9.1, 5.85) * mm});
            skLineSegment(sketch, "E207", {"start": v(-9.26, 6.07) * mm, "end": v(-9.4, 6.34) * mm});
            skLineSegment(sketch, "E208", {"start": v(-9.4, 6.34) * mm, "end": v(-9.1, 6.3) * mm});
            skCircle(sketch, "E209.cCircle", {"center": v(-8.32, 5.33) * mm, "radius": 0.19 * mm, "construction": true});
            skLineSegment(sketch, "E209.0", {"start": v(-8.4, 5.55) * mm, "end": v(-8.14, 5.46) * mm});
            skLineSegment(sketch, "E209.1", {"start": v(-8.14, 5.46) * mm, "end": v(-8.14, 5.2) * mm});
            skLineSegment(sketch, "E209.2", {"start": v(-8.14, 5.2) * mm, "end": v(-8.4, 5.1) * mm});
            skLineSegment(sketch, "E209.3", {"start": v(-8.4, 5.1) * mm, "end": v(-8.55, 5.33) * mm});
            skLineSegment(sketch, "E209.4", {"start": v(-8.55, 5.33) * mm, "end": v(-8.4, 5.55) * mm});
            skPoint(sketch, "E209.0.midPoint", {"position": v(-8.27, 5.5) * mm});
            skLineSegment(sketch, "E210", {"start": v(-8.4, 5.55) * mm, "end": v(-8.18, 5.76) * mm});
            skLineSegment(sketch, "E211", {"start": v(-8.18, 5.76) * mm, "end": v(-8.14, 5.46) * mm});
            skLineSegment(sketch, "E212", {"start": v(-8.14, 5.46) * mm, "end": v(-7.86, 5.33) * mm});
            skPoint(sketch, "E212.endSnap0", {"position": v(-8.14, 5.33) * mm});
            skLineSegment(sketch, "E213", {"start": v(-7.86, 5.33) * mm, "end": v(-8.14, 5.2) * mm});
            skLineSegment(sketch, "E214", {"start": v(-8.4, 5.1) * mm, "end": v(-8.18, 4.89) * mm});
            skLineSegment(sketch, "E215", {"start": v(-8.18, 4.89) * mm, "end": v(-8.14, 5.2) * mm});
            skLineSegment(sketch, "E216", {"start": v(-8.55, 5.33) * mm, "end": v(-8.7, 5.06) * mm});
            skLineSegment(sketch, "E217", {"start": v(-8.7, 5.06) * mm, "end": v(-8.4, 5.1) * mm});
            skLineSegment(sketch, "E218", {"start": v(-8.55, 5.33) * mm, "end": v(-8.7, 5.6) * mm});
            skLineSegment(sketch, "E219", {"start": v(-8.7, 5.6) * mm, "end": v(-8.4, 5.55) * mm});
            skCircle(sketch, "E220.cCircle", {"center": v(-8.8, 4.44) * mm, "radius": 0.19 * mm, "construction": true});
            skLineSegment(sketch, "E220.0", {"start": v(-8.87, 4.66) * mm, "end": v(-8.62, 4.57) * mm});
            skLineSegment(sketch, "E220.1", {"start": v(-8.62, 4.57) * mm, "end": v(-8.62, 4.3) * mm});
            skLineSegment(sketch, "E220.2", {"start": v(-8.62, 4.3) * mm, "end": v(-8.87, 4.22) * mm});
            skLineSegment(sketch, "E220.3", {"start": v(-8.87, 4.22) * mm, "end": v(-9.03, 4.44) * mm});
            skLineSegment(sketch, "E220.4", {"start": v(-9.03, 4.44) * mm, "end": v(-8.87, 4.66) * mm});
            skPoint(sketch, "E220.0.midPoint", {"position": v(-8.75, 4.61) * mm});
            skLineSegment(sketch, "E221", {"start": v(-8.87, 4.66) * mm, "end": v(-8.66, 4.87) * mm});
            skLineSegment(sketch, "E222", {"start": v(-8.66, 4.87) * mm, "end": v(-8.62, 4.57) * mm});
            skLineSegment(sketch, "E223", {"start": v(-8.62, 4.57) * mm, "end": v(-8.34, 4.44) * mm});
            skPoint(sketch, "E223.endSnap0", {"position": v(-8.62, 4.44) * mm});
            skLineSegment(sketch, "E224", {"start": v(-8.34, 4.44) * mm, "end": v(-8.62, 4.3) * mm});
            skLineSegment(sketch, "E225", {"start": v(-8.87, 4.22) * mm, "end": v(-8.66, 4) * mm});
            skLineSegment(sketch, "E226", {"start": v(-8.66, 4) * mm, "end": v(-8.62, 4.3) * mm});
            skLineSegment(sketch, "E227", {"start": v(-9.03, 4.44) * mm, "end": v(-9.17, 4.17) * mm});
            skLineSegment(sketch, "E228", {"start": v(-9.17, 4.17) * mm, "end": v(-8.87, 4.22) * mm});
            skLineSegment(sketch, "E229", {"start": v(-9.03, 4.44) * mm, "end": v(-9.17, 4.7) * mm});
            skLineSegment(sketch, "E230", {"start": v(-9.17, 4.7) * mm, "end": v(-8.87, 4.66) * mm});
            skCircle(sketch, "E231.cCircle", {"center": v(-9.81, 4.62) * mm, "radius": 0.19 * mm, "construction": true});
            skLineSegment(sketch, "E231.0", {"start": v(-9.88, 4.84) * mm, "end": v(-9.62, 4.76) * mm});
            skLineSegment(sketch, "E231.1", {"start": v(-9.62, 4.76) * mm, "end": v(-9.62, 4.48) * mm});
            skLineSegment(sketch, "E231.2", {"start": v(-9.62, 4.48) * mm, "end": v(-9.88, 4.4) * mm});
            skLineSegment(sketch, "E231.3", {"start": v(-9.88, 4.4) * mm, "end": v(-10.04, 4.62) * mm});
            skLineSegment(sketch, "E231.4", {"start": v(-10.04, 4.62) * mm, "end": v(-9.88, 4.84) * mm});
            skPoint(sketch, "E231.0.midPoint", {"position": v(-9.75, 4.8) * mm});
            skLineSegment(sketch, "E232", {"start": v(-9.88, 4.84) * mm, "end": v(-9.67, 5.06) * mm});
            skLineSegment(sketch, "E233", {"start": v(-9.67, 5.06) * mm, "end": v(-9.62, 4.76) * mm});
            skLineSegment(sketch, "E234", {"start": v(-9.62, 4.76) * mm, "end": v(-9.35, 4.62) * mm});
            skPoint(sketch, "E234.endSnap0", {"position": v(-9.62, 4.62) * mm});
            skLineSegment(sketch, "E235", {"start": v(-9.35, 4.62) * mm, "end": v(-9.62, 4.48) * mm});
            skLineSegment(sketch, "E236", {"start": v(-9.88, 4.4) * mm, "end": v(-9.67, 4.18) * mm});
            skLineSegment(sketch, "E237", {"start": v(-9.67, 4.18) * mm, "end": v(-9.62, 4.48) * mm});
            skLineSegment(sketch, "E238", {"start": v(-10.04, 4.62) * mm, "end": v(-10.18, 4.35) * mm});
            skLineSegment(sketch, "E239", {"start": v(-10.18, 4.35) * mm, "end": v(-9.88, 4.4) * mm});
            skLineSegment(sketch, "E240", {"start": v(-10.04, 4.62) * mm, "end": v(-10.18, 4.89) * mm});
            skLineSegment(sketch, "E241", {"start": v(-10.18, 4.89) * mm, "end": v(-9.88, 4.84) * mm});
            skCircle(sketch, "E242.cCircle", {"center": v(-9.94, 5.64) * mm, "radius": 0.19 * mm, "construction": true});
            skLineSegment(sketch, "E242.0", {"start": v(-10.02, 5.86) * mm, "end": v(-9.76, 5.78) * mm});
            skLineSegment(sketch, "E242.1", {"start": v(-9.76, 5.78) * mm, "end": v(-9.76, 5.5) * mm});
            skLineSegment(sketch, "E242.2", {"start": v(-9.76, 5.5) * mm, "end": v(-10.02, 5.42) * mm});
            skLineSegment(sketch, "E242.3", {"start": v(-10.02, 5.42) * mm, "end": v(-10.18, 5.64) * mm});
            skLineSegment(sketch, "E242.4", {"start": v(-10.18, 5.64) * mm, "end": v(-10.02, 5.86) * mm});
            skPoint(sketch, "E242.0.midPoint", {"position": v(-9.89, 5.82) * mm});
            skLineSegment(sketch, "E243", {"start": v(-10.02, 5.86) * mm, "end": v(-9.8, 6.08) * mm});
            skLineSegment(sketch, "E244", {"start": v(-9.8, 6.08) * mm, "end": v(-9.76, 5.78) * mm});
            skLineSegment(sketch, "E245", {"start": v(-9.76, 5.78) * mm, "end": v(-9.48, 5.64) * mm});
            skPoint(sketch, "E245.endSnap0", {"position": v(-9.76, 5.64) * mm});
            skLineSegment(sketch, "E246", {"start": v(-9.48, 5.64) * mm, "end": v(-9.76, 5.5) * mm});
            skLineSegment(sketch, "E247", {"start": v(-10.02, 5.42) * mm, "end": v(-9.8, 5.2) * mm});
            skLineSegment(sketch, "E248", {"start": v(-9.8, 5.2) * mm, "end": v(-9.76, 5.5) * mm});
            skLineSegment(sketch, "E249", {"start": v(-10.18, 5.64) * mm, "end": v(-10.32, 5.37) * mm});
            skLineSegment(sketch, "E250", {"start": v(-10.32, 5.37) * mm, "end": v(-10.02, 5.42) * mm});
            skLineSegment(sketch, "E251", {"start": v(-10.18, 5.64) * mm, "end": v(-10.32, 5.91) * mm});
            skLineSegment(sketch, "E252", {"start": v(-10.32, 5.91) * mm, "end": v(-10.02, 5.86) * mm});
            skSolve(sketch);
        }
        {
            var Q0;
            Q0=makeQuery(id+"F14.imprint","IMPRINT",FACE,{"disambiguationData":[TD([[makeQuery(id+"F14.imprint","IMPRINT",EDGE,{"derivedFrom":sQuery(id+"F14.wireOp",EDGE,"E19.4")}),1.0]])]});
            var Q1;
            Q1=makeQuery(id+"F14.imprint","IMPRINT",FACE,{"disambiguationData":[TD([[makeQuery(id+"F14.imprint","IMPRINT",EDGE,{"derivedFrom":sQuery(id+"F14.wireOp",EDGE,"E19.3")}),1.0]])]});
            var Q2;
            Q2=makeQuery(id+"F14.imprint","IMPRINT",FACE,{"disambiguationData":[TD([[makeQuery(id+"F14.imprint","IMPRINT",EDGE,{"derivedFrom":sQuery(id+"F14.wireOp",EDGE,"E19.2")}),1.0]])]});
            var Q3;
            Q3=makeQuery(id+"F14.imprint","IMPRINT",FACE,{"disambiguationData":[TD([[makeQuery(id+"F14.imprint","IMPRINT",EDGE,{"derivedFrom":sQuery(id+"F14.wireOp",EDGE,"E19.1")}),1.0]])]});
            var Q4;
            Q4=makeQuery(id+"F14.imprint","IMPRINT",FACE,{"disambiguationData":[TD([[makeQuery(id+"F14.imprint","IMPRINT",EDGE,{"derivedFrom":sQuery(id+"F14.wireOp",EDGE,"E19.0")}),1.0]])]});
            var Q5;
            Q5=makeQuery(id+"F14.imprint","IMPRINT",FACE,{"disambiguationData":[TD([[makeQuery(id+"F14.imprint","IMPRINT",EDGE,{"derivedFrom":sQuery(id+"F14.wireOp",EDGE,"E19.0")}),-1.0]])]});
            extrude(context, id + "F20", {"entities" : qUnion([Q0, Q1, Q2, Q3, Q4, Q5]), "operationType" : NewBodyOperationType.ADD, "depth" : 0.1 * mm});
        }
        {
            var Q0;
            Q0=makeQuery(id+"F15.imprint","IMPRINT",FACE,{"disambiguationData":[TD([[makeQuery(id+"F15.imprint","IMPRINT",EDGE,{"derivedFrom":sQuery(id+"F15.wireOp",EDGE,"E30.3")}),1.0]])]});
            var Q1;
            Q1=makeQuery(id+"F15.imprint","IMPRINT",FACE,{"disambiguationData":[TD([[makeQuery(id+"F15.imprint","IMPRINT",EDGE,{"derivedFrom":sQuery(id+"F15.wireOp",EDGE,"E30.4")}),1.0]])]});
            var Q2;
            Q2=makeQuery(id+"F15.imprint","IMPRINT",FACE,{"disambiguationData":[TD([[makeQuery(id+"F15.imprint","IMPRINT",EDGE,{"derivedFrom":sQuery(id+"F15.wireOp",EDGE,"E30.0")}),1.0]])]});
            var Q3;
            Q3=makeQuery(id+"F15.imprint","IMPRINT",FACE,{"disambiguationData":[TD([[makeQuery(id+"F15.imprint","IMPRINT",EDGE,{"derivedFrom":sQuery(id+"F15.wireOp",EDGE,"E30.1")}),1.0]])]});
            var Q4;
            Q4=makeQuery(id+"F15.imprint","IMPRINT",FACE,{"disambiguationData":[TD([[makeQuery(id+"F15.imprint","IMPRINT",EDGE,{"derivedFrom":sQuery(id+"F15.wireOp",EDGE,"E30.2")}),1.0]])]});
            var Q5;
            Q5=makeQuery(id+"F15.imprint","IMPRINT",FACE,{"disambiguationData":[TD([[makeQuery(id+"F15.imprint","IMPRINT",EDGE,{"derivedFrom":sQuery(id+"F15.wireOp",EDGE,"E30.0")}),-1.0]])]});
            var Q6;
            Q6=makeQuery(id+"F15.imprint","IMPRINT",FACE,{"disambiguationData":[TD([[makeQuery(id+"F15.imprint","IMPRINT",EDGE,{"derivedFrom":sQuery(id+"F15.wireOp",EDGE,"E41.0")}),1.0]])]});
            var Q7;
            Q7=makeQuery(id+"F15.imprint","IMPRINT",FACE,{"disambiguationData":[TD([[makeQuery(id+"F15.imprint","IMPRINT",EDGE,{"derivedFrom":sQuery(id+"F15.wireOp",EDGE,"E41.4")}),1.0]])]});
            var Q8;
            Q8=makeQuery(id+"F15.imprint","IMPRINT",FACE,{"disambiguationData":[TD([[makeQuery(id+"F15.imprint","IMPRINT",EDGE,{"derivedFrom":sQuery(id+"F15.wireOp",EDGE,"E41.2")}),1.0]])]});
            var Q9;
            Q9=makeQuery(id+"F15.imprint","IMPRINT",FACE,{"disambiguationData":[TD([[makeQuery(id+"F15.imprint","IMPRINT",EDGE,{"derivedFrom":sQuery(id+"F15.wireOp",EDGE,"E41.1")}),1.0]])]});
            var Q10;
            Q10=makeQuery(id+"F15.imprint","IMPRINT",FACE,{"disambiguationData":[TD([[makeQuery(id+"F15.imprint","IMPRINT",EDGE,{"derivedFrom":sQuery(id+"F15.wireOp",EDGE,"E41.3")}),1.0]])]});
            var Q11;
            Q11=makeQuery(id+"F15.imprint","IMPRINT",FACE,{"disambiguationData":[TD([[makeQuery(id+"F15.imprint","IMPRINT",EDGE,{"derivedFrom":sQuery(id+"F15.wireOp",EDGE,"E41.0")}),-1.0]])]});
            extrude(context, id + "F21", {"entities" : qUnion([Q0, Q1, Q2, Q3, Q4, Q5, Q6, Q7, Q8, Q9, Q10, Q11]), "operationType" : NewBodyOperationType.ADD, "depth" : 0.1 * mm});
        }
        {
            var Q0;
            Q0=makeQuery(id+"F16.imprint","IMPRINT",FACE,{"disambiguationData":[TD([[makeQuery(id+"F16.imprint","IMPRINT",EDGE,{"derivedFrom":sQuery(id+"F16.wireOp",EDGE,"E63.4")}),1.0]])]});
            var Q1;
            Q1=makeQuery(id+"F16.imprint","IMPRINT",FACE,{"disambiguationData":[TD([[makeQuery(id+"F16.imprint","IMPRINT",EDGE,{"derivedFrom":sQuery(id+"F16.wireOp",EDGE,"E63.3")}),1.0]])]});
            var Q2;
            Q2=makeQuery(id+"F16.imprint","IMPRINT",FACE,{"disambiguationData":[TD([[makeQuery(id+"F16.imprint","IMPRINT",EDGE,{"derivedFrom":sQuery(id+"F16.wireOp",EDGE,"E63.2")}),1.0]])]});
            var Q3;
            Q3=makeQuery(id+"F16.imprint","IMPRINT",FACE,{"disambiguationData":[TD([[makeQuery(id+"F16.imprint","IMPRINT",EDGE,{"derivedFrom":sQuery(id+"F16.wireOp",EDGE,"E63.0")}),1.0]])]});
            var Q4;
            Q4=makeQuery(id+"F16.imprint","IMPRINT",FACE,{"disambiguationData":[TD([[makeQuery(id+"F16.imprint","IMPRINT",EDGE,{"derivedFrom":sQuery(id+"F16.wireOp",EDGE,"E63.1")}),1.0]])]});
            var Q5;
            Q5=makeQuery(id+"F16.imprint","IMPRINT",FACE,{"disambiguationData":[TD([[makeQuery(id+"F16.imprint","IMPRINT",EDGE,{"derivedFrom":sQuery(id+"F16.wireOp",EDGE,"E63.0")}),-1.0]])]});
            var Q6;
            Q6=makeQuery(id+"F16.imprint","IMPRINT",FACE,{"disambiguationData":[TD([[makeQuery(id+"F16.imprint","IMPRINT",EDGE,{"derivedFrom":sQuery(id+"F16.wireOp",EDGE,"E52.0")}),1.0]])]});
            var Q7;
            Q7=makeQuery(id+"F16.imprint","IMPRINT",FACE,{"disambiguationData":[TD([[makeQuery(id+"F16.imprint","IMPRINT",EDGE,{"derivedFrom":sQuery(id+"F16.wireOp",EDGE,"E52.0")}),-1.0]])]});
            var Q8;
            Q8=makeQuery(id+"F16.imprint","IMPRINT",FACE,{"disambiguationData":[TD([[makeQuery(id+"F16.imprint","IMPRINT",EDGE,{"derivedFrom":sQuery(id+"F16.wireOp",EDGE,"E52.4")}),1.0]])]});
            var Q9;
            Q9=makeQuery(id+"F16.imprint","IMPRINT",FACE,{"disambiguationData":[TD([[makeQuery(id+"F16.imprint","IMPRINT",EDGE,{"derivedFrom":sQuery(id+"F16.wireOp",EDGE,"E52.3")}),1.0]])]});
            var Q10;
            Q10=makeQuery(id+"F16.imprint","IMPRINT",FACE,{"disambiguationData":[TD([[makeQuery(id+"F16.imprint","IMPRINT",EDGE,{"derivedFrom":sQuery(id+"F16.wireOp",EDGE,"E52.2")}),1.0]])]});
            var Q11;
            Q11=makeQuery(id+"F16.imprint","IMPRINT",FACE,{"disambiguationData":[TD([[makeQuery(id+"F16.imprint","IMPRINT",EDGE,{"derivedFrom":sQuery(id+"F16.wireOp",EDGE,"E52.1")}),1.0]])]});
            var Q12;
            Q12=makeQuery(id+"F16.imprint","IMPRINT",FACE,{"disambiguationData":[TD([[makeQuery(id+"F16.imprint","IMPRINT",EDGE,{"derivedFrom":sQuery(id+"F16.wireOp",EDGE,"E74.0")}),-1.0]])]});
            var Q13;
            Q13=makeQuery(id+"F16.imprint","IMPRINT",FACE,{"disambiguationData":[TD([[makeQuery(id+"F16.imprint","IMPRINT",EDGE,{"derivedFrom":sQuery(id+"F16.wireOp",EDGE,"E74.4")}),1.0]])]});
            var Q14;
            Q14=makeQuery(id+"F16.imprint","IMPRINT",FACE,{"disambiguationData":[TD([[makeQuery(id+"F16.imprint","IMPRINT",EDGE,{"derivedFrom":sQuery(id+"F16.wireOp",EDGE,"E74.3")}),1.0]])]});
            var Q15;
            Q15=makeQuery(id+"F16.imprint","IMPRINT",FACE,{"disambiguationData":[TD([[makeQuery(id+"F16.imprint","IMPRINT",EDGE,{"derivedFrom":sQuery(id+"F16.wireOp",EDGE,"E74.2")}),1.0]])]});
            var Q16;
            Q16=makeQuery(id+"F16.imprint","IMPRINT",FACE,{"disambiguationData":[TD([[makeQuery(id+"F16.imprint","IMPRINT",EDGE,{"derivedFrom":sQuery(id+"F16.wireOp",EDGE,"E74.1")}),1.0]])]});
            var Q17;
            Q17=makeQuery(id+"F16.imprint","IMPRINT",FACE,{"disambiguationData":[TD([[makeQuery(id+"F16.imprint","IMPRINT",EDGE,{"derivedFrom":sQuery(id+"F16.wireOp",EDGE,"E74.0")}),1.0]])]});
            extrude(context, id + "F22", {"entities" : qUnion([Q0, Q1, Q2, Q3, Q4, Q5, Q6, Q7, Q8, Q9, Q10, Q11, Q12, Q13, Q14, Q15, Q16, Q17]), "operationType" : NewBodyOperationType.ADD, "depth" : 0.1 * mm});
        }
        {
            var Q0;
            Q0=makeQuery(id+"F9.imprint","IMPRINT",FACE,{"disambiguationData":[TD([[makeQuery(id+"F9.imprint","IMPRINT",EDGE,{"derivedFrom":sQuery(id+"F9.wireOp",EDGE,"E9")}),1.0]])]});
            var sketch = newSketch(context, id + "F23", { "sketchPlane" : qUnion([Q0])});
            skCircle(sketch, "E253.cCircle", {"center": v(0, -0.04) * mm, "radius": 0.9 * mm, "construction": true});
            skLineSegment(sketch, "E253.0", {"start": v(-1.03, 0.14) * mm, "end": v(-0.37, 0.94) * mm});
            skLineSegment(sketch, "E253.1", {"start": v(-0.37, 0.94) * mm, "end": v(0.66, 0.77) * mm});
            skLineSegment(sketch, "E253.2", {"start": v(0.66, 0.77) * mm, "end": v(1.02, -0.2) * mm});
            skLineSegment(sketch, "E253.3", {"start": v(1.02, -0.2) * mm, "end": v(0.36, -1.01) * mm});
            skLineSegment(sketch, "E253.4", {"start": v(0.36, -1.01) * mm, "end": v(-0.67, -0.84) * mm});
            skLineSegment(sketch, "E253.5", {"start": v(-0.67, -0.84) * mm, "end": v(-1.03, 0.14) * mm});
            skPoint(sketch, "E253.0.midPoint", {"position": v(-0.7, 0.54) * mm});
            skCircle(sketch, "E254.cCircle", {"center": v(-0.37, 0.88) * mm, "radius": 0.25 * mm, "construction": true});
            skLineSegment(sketch, "E254.0", {"start": v(-0.46, 1.18) * mm, "end": v(-0.12, 1.07) * mm});
            skLineSegment(sketch, "E254.1", {"start": v(-0.12, 1.07) * mm, "end": v(-0.12, 0.7) * mm});
            skLineSegment(sketch, "E254.2", {"start": v(-0.12, 0.7) * mm, "end": v(-0.46, 0.59) * mm});
            skLineSegment(sketch, "E254.3", {"start": v(-0.46, 0.59) * mm, "end": v(-0.68, 0.88) * mm});
            skLineSegment(sketch, "E254.4", {"start": v(-0.68, 0.88) * mm, "end": v(-0.46, 1.18) * mm});
            skPoint(sketch, "E254.0.midPoint", {"position": v(-0.3, 1.12) * mm});
            skLineSegment(sketch, "E255", {"start": v(-0.46, 1.18) * mm, "end": v(-0.22, 1.35) * mm});
            skLineSegment(sketch, "E256", {"start": v(-0.22, 1.35) * mm, "end": v(-0.12, 1.07) * mm});
            skLineSegment(sketch, "E257", {"start": v(-0.12, 1.07) * mm, "end": v(0.13, 0.88) * mm});
            skPoint(sketch, "E257.endSnap0", {"position": v(-0.12, 0.88) * mm});
            skLineSegment(sketch, "E258", {"start": v(0.13, 0.88) * mm, "end": v(-0.12, 0.7) * mm});
            skLineSegment(sketch, "E259", {"start": v(-0.46, 0.59) * mm, "end": v(-0.22, 0.41) * mm});
            skLineSegment(sketch, "E260", {"start": v(-0.22, 0.41) * mm, "end": v(-0.12, 0.7) * mm});
            skLineSegment(sketch, "E261", {"start": v(-0.68, 0.88) * mm, "end": v(-0.77, 0.6) * mm});
            skLineSegment(sketch, "E262", {"start": v(-0.77, 0.6) * mm, "end": v(-0.46, 0.59) * mm});
            skLineSegment(sketch, "E263", {"start": v(-0.68, 0.88) * mm, "end": v(-0.77, 1.17) * mm});
            skLineSegment(sketch, "E264", {"start": v(-0.77, 1.17) * mm, "end": v(-0.46, 1.18) * mm});
            skCircle(sketch, "E265.cCircle", {"center": v(0.67, 0.73) * mm, "radius": 0.25 * mm, "construction": true});
            skLineSegment(sketch, "E265.0", {"start": v(0.57, 1.02) * mm, "end": v(0.92, 0.91) * mm});
            skLineSegment(sketch, "E265.1", {"start": v(0.92, 0.91) * mm, "end": v(0.92, 0.55) * mm});
            skLineSegment(sketch, "E265.2", {"start": v(0.92, 0.55) * mm, "end": v(0.57, 0.43) * mm});
            skLineSegment(sketch, "E265.3", {"start": v(0.57, 0.43) * mm, "end": v(0.36, 0.73) * mm});
            skLineSegment(sketch, "E265.4", {"start": v(0.36, 0.73) * mm, "end": v(0.57, 1.02) * mm});
            skPoint(sketch, "E265.0.midPoint", {"position": v(0.75, 0.97) * mm});
            skLineSegment(sketch, "E266", {"start": v(0.57, 1.02) * mm, "end": v(0.82, 1.2) * mm});
            skLineSegment(sketch, "E267", {"start": v(0.82, 1.2) * mm, "end": v(0.92, 0.91) * mm});
            skLineSegment(sketch, "E268", {"start": v(0.92, 0.91) * mm, "end": v(1.16, 0.73) * mm});
            skPoint(sketch, "E268.endSnap0", {"position": v(0.92, 0.73) * mm});
            skLineSegment(sketch, "E269", {"start": v(1.16, 0.73) * mm, "end": v(0.92, 0.55) * mm});
            skLineSegment(sketch, "E270", {"start": v(0.57, 0.43) * mm, "end": v(0.82, 0.26) * mm});
            skLineSegment(sketch, "E271", {"start": v(0.82, 0.26) * mm, "end": v(0.92, 0.55) * mm});
            skLineSegment(sketch, "E272", {"start": v(0.36, 0.73) * mm, "end": v(0.27, 0.44) * mm});
            skLineSegment(sketch, "E273", {"start": v(0.27, 0.44) * mm, "end": v(0.57, 0.43) * mm});
            skLineSegment(sketch, "E274", {"start": v(0.36, 0.73) * mm, "end": v(0.27, 1.02) * mm});
            skLineSegment(sketch, "E275", {"start": v(0.27, 1.02) * mm, "end": v(0.57, 1.02) * mm});
            skCircle(sketch, "E276.cCircle", {"center": v(1.02, -0.25) * mm, "radius": 0.25 * mm, "construction": true});
            skLineSegment(sketch, "E276.0", {"start": v(0.92, 0.04) * mm, "end": v(1.27, -0.07) * mm});
            skLineSegment(sketch, "E276.1", {"start": v(1.27, -0.07) * mm, "end": v(1.27, -0.44) * mm});
            skLineSegment(sketch, "E276.2", {"start": v(1.27, -0.44) * mm, "end": v(0.92, -0.55) * mm});
            skLineSegment(sketch, "E276.3", {"start": v(0.92, -0.55) * mm, "end": v(0.7, -0.25) * mm});
            skLineSegment(sketch, "E276.4", {"start": v(0.7, -0.25) * mm, "end": v(0.92, 0.04) * mm});
            skPoint(sketch, "E276.0.midPoint", {"position": v(1.1, -0.01) * mm});
            skLineSegment(sketch, "E277", {"start": v(0.92, 0.04) * mm, "end": v(1.17, 0.22) * mm});
            skLineSegment(sketch, "E278", {"start": v(1.17, 0.22) * mm, "end": v(1.27, -0.07) * mm});
            skLineSegment(sketch, "E279", {"start": v(1.27, -0.07) * mm, "end": v(1.52, -0.25) * mm});
            skPoint(sketch, "E279.endSnap0", {"position": v(1.27, -0.25) * mm});
            skLineSegment(sketch, "E280", {"start": v(1.52, -0.25) * mm, "end": v(1.27, -0.44) * mm});
            skLineSegment(sketch, "E281", {"start": v(0.92, -0.55) * mm, "end": v(1.17, -0.72) * mm});
            skLineSegment(sketch, "E282", {"start": v(1.17, -0.72) * mm, "end": v(1.27, -0.44) * mm});
            skLineSegment(sketch, "E283", {"start": v(0.7, -0.25) * mm, "end": v(0.62, -0.54) * mm});
            skLineSegment(sketch, "E284", {"start": v(0.62, -0.54) * mm, "end": v(0.92, -0.55) * mm});
            skLineSegment(sketch, "E285", {"start": v(0.7, -0.25) * mm, "end": v(0.62, 0.04) * mm});
            skLineSegment(sketch, "E286", {"start": v(0.62, 0.04) * mm, "end": v(0.92, 0.04) * mm});
            skCircle(sketch, "E287.cCircle", {"center": v(0.34, -1.04) * mm, "radius": 0.25 * mm, "construction": true});
            skLineSegment(sketch, "E287.0", {"start": v(0.24, -0.74) * mm, "end": v(0.6, -0.86) * mm});
            skLineSegment(sketch, "E287.1", {"start": v(0.6, -0.86) * mm, "end": v(0.6, -1.22) * mm});
            skLineSegment(sketch, "E287.2", {"start": v(0.6, -1.22) * mm, "end": v(0.24, -1.33) * mm});
            skLineSegment(sketch, "E287.3", {"start": v(0.24, -1.33) * mm, "end": v(0.03, -1.04) * mm});
            skLineSegment(sketch, "E287.4", {"start": v(0.03, -1.04) * mm, "end": v(0.24, -0.74) * mm});
            skPoint(sketch, "E287.0.midPoint", {"position": v(0.42, -0.8) * mm});
            skLineSegment(sketch, "E288", {"start": v(0.24, -0.74) * mm, "end": v(0.5, -0.57) * mm});
            skLineSegment(sketch, "E289", {"start": v(0.5, -0.57) * mm, "end": v(0.6, -0.86) * mm});
            skLineSegment(sketch, "E290", {"start": v(0.6, -0.86) * mm, "end": v(0.84, -1.04) * mm});
            skPoint(sketch, "E290.endSnap0", {"position": v(0.6, -1.04) * mm});
            skLineSegment(sketch, "E291", {"start": v(0.84, -1.04) * mm, "end": v(0.6, -1.22) * mm});
            skLineSegment(sketch, "E292", {"start": v(0.24, -1.33) * mm, "end": v(0.5, -1.5) * mm});
            skLineSegment(sketch, "E293", {"start": v(0.5, -1.5) * mm, "end": v(0.6, -1.22) * mm});
            skLineSegment(sketch, "E294", {"start": v(0.03, -1.04) * mm, "end": v(-0.06, -1.33) * mm});
            skLineSegment(sketch, "E295", {"start": v(-0.06, -1.33) * mm, "end": v(0.24, -1.33) * mm});
            skLineSegment(sketch, "E296", {"start": v(0.03, -1.04) * mm, "end": v(-0.06, -0.75) * mm});
            skLineSegment(sketch, "E297", {"start": v(-0.06, -0.75) * mm, "end": v(0.24, -0.74) * mm});
            skCircle(sketch, "E298.cCircle", {"center": v(-0.67, -0.85) * mm, "radius": 0.25 * mm, "construction": true});
            skLineSegment(sketch, "E298.0", {"start": v(-0.77, -0.55) * mm, "end": v(-0.42, -0.67) * mm});
            skLineSegment(sketch, "E298.1", {"start": v(-0.42, -0.67) * mm, "end": v(-0.42, -1.03) * mm});
            skLineSegment(sketch, "E298.2", {"start": v(-0.42, -1.03) * mm, "end": v(-0.77, -1.14) * mm});
            skLineSegment(sketch, "E298.3", {"start": v(-0.77, -1.14) * mm, "end": v(-0.98, -0.85) * mm});
            skLineSegment(sketch, "E298.4", {"start": v(-0.98, -0.85) * mm, "end": v(-0.77, -0.55) * mm});
            skPoint(sketch, "E298.0.midPoint", {"position": v(-0.6, -0.6) * mm});
            skLineSegment(sketch, "E299", {"start": v(-0.77, -0.55) * mm, "end": v(-0.52, -0.38) * mm});
            skLineSegment(sketch, "E300", {"start": v(-0.52, -0.38) * mm, "end": v(-0.42, -0.67) * mm});
            skLineSegment(sketch, "E301", {"start": v(-0.42, -0.67) * mm, "end": v(-0.17, -0.85) * mm});
            skPoint(sketch, "E301.endSnap0", {"position": v(-0.42, -0.85) * mm});
            skLineSegment(sketch, "E302", {"start": v(-0.17, -0.85) * mm, "end": v(-0.42, -1.03) * mm});
            skLineSegment(sketch, "E303", {"start": v(-0.77, -1.14) * mm, "end": v(-0.52, -1.32) * mm});
            skLineSegment(sketch, "E304", {"start": v(-0.52, -1.32) * mm, "end": v(-0.42, -1.03) * mm});
            skLineSegment(sketch, "E305", {"start": v(-0.98, -0.85) * mm, "end": v(-1.07, -1.14) * mm});
            skLineSegment(sketch, "E306", {"start": v(-1.07, -1.14) * mm, "end": v(-0.77, -1.14) * mm});
            skLineSegment(sketch, "E307", {"start": v(-0.98, -0.85) * mm, "end": v(-1.07, -0.56) * mm});
            skLineSegment(sketch, "E308", {"start": v(-1.07, -0.56) * mm, "end": v(-0.77, -0.55) * mm});
            skCircle(sketch, "E309.cCircle", {"center": v(-1.06, 0.13) * mm, "radius": 0.25 * mm, "construction": true});
            skLineSegment(sketch, "E309.0", {"start": v(-1.15, 0.42) * mm, "end": v(-0.8, 0.3) * mm});
            skLineSegment(sketch, "E309.1", {"start": v(-0.8, 0.3) * mm, "end": v(-0.8, -0.06) * mm});
            skLineSegment(sketch, "E309.2", {"start": v(-0.8, -0.06) * mm, "end": v(-1.15, -0.17) * mm});
            skLineSegment(sketch, "E309.3", {"start": v(-1.15, -0.17) * mm, "end": v(-1.37, 0.13) * mm});
            skLineSegment(sketch, "E309.4", {"start": v(-1.37, 0.13) * mm, "end": v(-1.15, 0.42) * mm});
            skPoint(sketch, "E309.0.midPoint", {"position": v(-0.98, 0.37) * mm});
            skLineSegment(sketch, "E310", {"start": v(-1.15, 0.42) * mm, "end": v(-0.9, 0.6) * mm});
            skLineSegment(sketch, "E311", {"start": v(-0.9, 0.6) * mm, "end": v(-0.8, 0.3) * mm});
            skLineSegment(sketch, "E312", {"start": v(-0.8, 0.3) * mm, "end": v(-0.56, 0.13) * mm});
            skPoint(sketch, "E312.endSnap0", {"position": v(-0.8, 0.13) * mm});
            skLineSegment(sketch, "E313", {"start": v(-0.56, 0.13) * mm, "end": v(-0.8, -0.06) * mm});
            skLineSegment(sketch, "E314", {"start": v(-1.15, -0.17) * mm, "end": v(-0.9, -0.35) * mm});
            skLineSegment(sketch, "E315", {"start": v(-0.9, -0.35) * mm, "end": v(-0.8, -0.06) * mm});
            skLineSegment(sketch, "E316", {"start": v(-1.37, 0.13) * mm, "end": v(-1.46, -0.17) * mm});
            skLineSegment(sketch, "E317", {"start": v(-1.46, -0.17) * mm, "end": v(-1.15, -0.17) * mm});
            skLineSegment(sketch, "E318", {"start": v(-1.37, 0.13) * mm, "end": v(-1.46, 0.42) * mm});
            skLineSegment(sketch, "E319", {"start": v(-1.46, 0.42) * mm, "end": v(-1.15, 0.42) * mm});
            skSolve(sketch);
        }
        {
            var Q0;
            Q0=makeQuery(id+"F18.imprint","IMPRINT",FACE,{"disambiguationData":[TD([[makeQuery(id+"F18.imprint","IMPRINT",EDGE,{"derivedFrom":sQuery(id+"F18.wireOp",EDGE,"E131.4")}),1.0]])]});
            var Q1;
            {var subQ5=sQuery(id+"F18.wireOp",EDGE,"E138");Q1=makeQuery(id+"F18.imprint","IMPRINT",FACE,{"disambiguationData":[TD([[makeQuery(id+"F18.imprint","IMPRINT",EDGE,{"derivedFrom":subQ5}),1.0]])]});}
            var Q2;
            {var subQ0=sQuery(id+"F18.wireOp",EDGE,"E139");var subQ1=sQuery(id+"F18.wireOp",EDGE,"E130.3");var subQ2=makeQuery(id+"F18.imprint","INTERSECT",VERTEX,{"derivedFrom":[subQ1,subQ0]});Q2=makeQuery(id+"F18.imprint","IMPRINT",FACE,{"disambiguationData":[TD([[makeQuery(id+"F18.imprint","IMPRINT",EDGE,{"disambiguationData":[TD([[subQ2,-1.0]])],"derivedFrom":subQ1}),-1.0]])]});}
            var Q3;
            Q3=makeQuery(id+"F18.imprint","IMPRINT",FACE,{"disambiguationData":[TD([[makeQuery(id+"F18.imprint","IMPRINT",EDGE,{"derivedFrom":sQuery(id+"F18.wireOp",EDGE,"E131.2")}),1.0]])]});
            var Q4;
            {var subQ5=sQuery(id+"F18.wireOp",EDGE,"E134");Q4=makeQuery(id+"F18.imprint","IMPRINT",FACE,{"disambiguationData":[TD([[makeQuery(id+"F18.imprint","IMPRINT",EDGE,{"derivedFrom":subQ5}),-1.0]])]});}
            var Q5;
            {var subQ0=sQuery(id+"F18.wireOp",EDGE,"E131.1");var subQ1=sQuery(id+"F18.wireOp",EDGE,"E130.4");var subQ2=makeQuery(id+"F18.imprint","INTERSECT",VERTEX,{"derivedFrom":[subQ1,subQ0]});Q5=makeQuery(id+"F18.imprint","IMPRINT",FACE,{"disambiguationData":[TD([[makeQuery(id+"F18.imprint","IMPRINT",EDGE,{"disambiguationData":[TD([[subQ2,-1.0]])],"derivedFrom":subQ1}),-1.0]])]});}
            var Q6;
            Q6=makeQuery(id+"F18.imprint","IMPRINT",FACE,{"disambiguationData":[TD([[makeQuery(id+"F18.imprint","IMPRINT",EDGE,{"derivedFrom":sQuery(id+"F18.wireOp",EDGE,"E131.0")}),1.0]])]});
            var Q7;
            {var subQ5=sQuery(id+"F18.wireOp",EDGE,"E176");Q7=makeQuery(id+"F18.imprint","IMPRINT",FACE,{"disambiguationData":[TD([[makeQuery(id+"F18.imprint","IMPRINT",EDGE,{"derivedFrom":subQ5}),-1.0]])]});}
            var Q8;
            Q8=makeQuery(id+"F18.imprint","IMPRINT",FACE,{"disambiguationData":[TD([[makeQuery(id+"F18.imprint","IMPRINT",EDGE,{"derivedFrom":sQuery(id+"F18.wireOp",EDGE,"E175.4")}),1.0]])]});
            var Q9;
            Q9=makeQuery(id+"F18.imprint","IMPRINT",FACE,{"disambiguationData":[TD([[makeQuery(id+"F18.imprint","IMPRINT",EDGE,{"derivedFrom":sQuery(id+"F18.wireOp",EDGE,"E175.3")}),1.0]])]});
            var Q10;
            {var subQ5=sQuery(id+"F18.wireOp",EDGE,"E180");Q10=makeQuery(id+"F18.imprint","IMPRINT",FACE,{"disambiguationData":[TD([[makeQuery(id+"F18.imprint","IMPRINT",EDGE,{"derivedFrom":subQ5}),1.0]])]});}
            var Q11;
            Q11=makeQuery(id+"F18.imprint","IMPRINT",FACE,{"disambiguationData":[TD([[makeQuery(id+"F18.imprint","IMPRINT",EDGE,{"derivedFrom":sQuery(id+"F18.wireOp",EDGE,"E175.1")}),1.0]])]});
            var Q12;
            {var subQ0=sQuery(id+"F18.wireOp",EDGE,"E175.0");var subQ1=sQuery(id+"F18.wireOp",EDGE,"E130.3");var subQ2=makeQuery(id+"F18.imprint","INTERSECT",VERTEX,{"derivedFrom":[subQ1,subQ0]});Q12=makeQuery(id+"F18.imprint","IMPRINT",FACE,{"disambiguationData":[TD([[makeQuery(id+"F18.imprint","IMPRINT",EDGE,{"disambiguationData":[TD([[subQ2,-1.0]])],"derivedFrom":subQ1}),-1.0]])]});}
            var Q13;
            {var subQ0=sQuery(id+"F18.wireOp",EDGE,"E175.3");Q13=makeQuery(id+"F18.imprint","IMPRINT",FACE,{"disambiguationData":[TD([[makeQuery(id+"F18.imprint","IMPRINT",EDGE,{"derivedFrom":subQ0}),-1.0]])]});}
            var Q14;
            {var subQ0=sQuery(id+"F18.wireOp",EDGE,"E175.1");Q14=makeQuery(id+"F18.imprint","IMPRINT",FACE,{"disambiguationData":[TD([[makeQuery(id+"F18.imprint","IMPRINT",EDGE,{"derivedFrom":subQ0}),-1.0]])]});}
            var Q15;
            {var subQ1=sQuery(id+"F18.wireOp",EDGE,"E131.0");Q15=makeQuery(id+"F18.imprint","IMPRINT",FACE,{"disambiguationData":[TD([[makeQuery(id+"F18.imprint","IMPRINT",EDGE,{"derivedFrom":subQ1}),-1.0]])]});}
            var Q16;
            {var subQ0=sQuery(id+"F18.wireOp",EDGE,"E131.2");Q16=makeQuery(id+"F18.imprint","IMPRINT",FACE,{"disambiguationData":[TD([[makeQuery(id+"F18.imprint","IMPRINT",EDGE,{"derivedFrom":subQ0}),-1.0]])]});}
            var Q17;
            {var subQ0=sQuery(id+"F18.wireOp",EDGE,"E142.3");Q17=makeQuery(id+"F18.imprint","IMPRINT",FACE,{"disambiguationData":[TD([[makeQuery(id+"F18.imprint","IMPRINT",EDGE,{"derivedFrom":subQ0}),-1.0]])]});}
            var Q18;
            {var subQ6=sQuery(id+"F18.wireOp",EDGE,"E142.0");Q18=makeQuery(id+"F18.imprint","IMPRINT",FACE,{"disambiguationData":[TD([[makeQuery(id+"F18.imprint","IMPRINT",EDGE,{"derivedFrom":subQ6}),-1.0]])]});}
            var Q19;
            {var subQ0=sQuery(id+"F18.wireOp",EDGE,"E153.4");Q19=makeQuery(id+"F18.imprint","IMPRINT",FACE,{"disambiguationData":[TD([[makeQuery(id+"F18.imprint","IMPRINT",EDGE,{"derivedFrom":subQ0}),-1.0]])]});}
            var Q20;
            {var subQ0=sQuery(id+"F18.wireOp",EDGE,"E153.1");Q20=makeQuery(id+"F18.imprint","IMPRINT",FACE,{"disambiguationData":[TD([[makeQuery(id+"F18.imprint","IMPRINT",EDGE,{"derivedFrom":subQ0}),-1.0]])]});}
            var Q21;
            {var subQ0=sQuery(id+"F18.wireOp",EDGE,"E164.0");Q21=makeQuery(id+"F18.imprint","IMPRINT",FACE,{"disambiguationData":[TD([[makeQuery(id+"F18.imprint","IMPRINT",EDGE,{"derivedFrom":subQ0}),-1.0]])]});}
            var Q22;
            {var subQ0=sQuery(id+"F18.wireOp",EDGE,"E164.2");Q22=makeQuery(id+"F18.imprint","IMPRINT",FACE,{"disambiguationData":[TD([[makeQuery(id+"F18.imprint","IMPRINT",EDGE,{"derivedFrom":subQ0}),-1.0]])]});}
            var Q23;
            {var subQ5=sQuery(id+"F18.wireOp",EDGE,"E173");Q23=makeQuery(id+"F18.imprint","IMPRINT",FACE,{"disambiguationData":[TD([[makeQuery(id+"F18.imprint","IMPRINT",EDGE,{"derivedFrom":subQ5}),-1.0]])]});}
            var Q24;
            Q24=makeQuery(id+"F18.imprint","IMPRINT",FACE,{"disambiguationData":[TD([[makeQuery(id+"F18.imprint","IMPRINT",EDGE,{"derivedFrom":sQuery(id+"F18.wireOp",EDGE,"E164.3")}),1.0]])]});
            var Q25;
            Q25=makeQuery(id+"F18.imprint","IMPRINT",FACE,{"disambiguationData":[TD([[makeQuery(id+"F18.imprint","IMPRINT",EDGE,{"derivedFrom":sQuery(id+"F18.wireOp",EDGE,"E164.2")}),1.0]])]});
            var Q26;
            {var subQ5=sQuery(id+"F18.wireOp",EDGE,"E168");Q26=makeQuery(id+"F18.imprint","IMPRINT",FACE,{"disambiguationData":[TD([[makeQuery(id+"F18.imprint","IMPRINT",EDGE,{"derivedFrom":subQ5}),-1.0]])]});}
            var Q27;
            Q27=makeQuery(id+"F18.imprint","IMPRINT",FACE,{"disambiguationData":[TD([[makeQuery(id+"F18.imprint","IMPRINT",EDGE,{"derivedFrom":sQuery(id+"F18.wireOp",EDGE,"E164.0")}),1.0]])]});
            var Q28;
            Q28=makeQuery(id+"F18.imprint","IMPRINT",FACE,{"disambiguationData":[TD([[makeQuery(id+"F18.imprint","IMPRINT",EDGE,{"derivedFrom":sQuery(id+"F18.wireOp",EDGE,"E153.4")}),1.0]])]});
            var Q29;
            {var subQ5=sQuery(id+"F18.wireOp",EDGE,"E161");Q29=makeQuery(id+"F18.imprint","IMPRINT",FACE,{"disambiguationData":[TD([[makeQuery(id+"F18.imprint","IMPRINT",EDGE,{"derivedFrom":subQ5}),1.0]])]});}
            var Q30;
            {var subQ0=sQuery(id+"F18.wireOp",EDGE,"E153.3");var subQ1=sQuery(id+"F18.wireOp",EDGE,"E130.1");var subQ2=makeQuery(id+"F18.imprint","INTERSECT",VERTEX,{"derivedFrom":[subQ1,subQ0]});Q30=makeQuery(id+"F18.imprint","IMPRINT",FACE,{"disambiguationData":[TD([[makeQuery(id+"F18.imprint","IMPRINT",EDGE,{"disambiguationData":[TD([[subQ2,-1.0]])],"derivedFrom":subQ1}),-1.0]])]});}
            var Q31;
            Q31=makeQuery(id+"F18.imprint","IMPRINT",FACE,{"disambiguationData":[TD([[makeQuery(id+"F18.imprint","IMPRINT",EDGE,{"derivedFrom":sQuery(id+"F18.wireOp",EDGE,"E153.2")}),1.0]])]});
            var Q32;
            Q32=makeQuery(id+"F18.imprint","IMPRINT",FACE,{"disambiguationData":[TD([[makeQuery(id+"F18.imprint","IMPRINT",EDGE,{"derivedFrom":sQuery(id+"F18.wireOp",EDGE,"E153.1")}),1.0]])]});
            var Q33;
            {var subQ5=sQuery(id+"F18.wireOp",EDGE,"E155");Q33=makeQuery(id+"F18.imprint","IMPRINT",FACE,{"disambiguationData":[TD([[makeQuery(id+"F18.imprint","IMPRINT",EDGE,{"derivedFrom":subQ5}),-1.0]])]});}
            var Q34;
            {var subQ5=sQuery(id+"F18.wireOp",EDGE,"E148");Q34=makeQuery(id+"F18.imprint","IMPRINT",FACE,{"disambiguationData":[TD([[makeQuery(id+"F18.imprint","IMPRINT",EDGE,{"derivedFrom":subQ5}),1.0]])]});}
            var Q35;
            Q35=makeQuery(id+"F18.imprint","IMPRINT",FACE,{"disambiguationData":[TD([[makeQuery(id+"F18.imprint","IMPRINT",EDGE,{"derivedFrom":sQuery(id+"F18.wireOp",EDGE,"E142.1")}),1.0]])]});
            var Q36;
            Q36=makeQuery(id+"F18.imprint","IMPRINT",FACE,{"disambiguationData":[TD([[makeQuery(id+"F18.imprint","IMPRINT",EDGE,{"derivedFrom":sQuery(id+"F18.wireOp",EDGE,"E142.0")}),1.0]])]});
            var Q37;
            {var subQ5=sQuery(id+"F18.wireOp",EDGE,"E152");Q37=makeQuery(id+"F18.imprint","IMPRINT",FACE,{"disambiguationData":[TD([[makeQuery(id+"F18.imprint","IMPRINT",EDGE,{"derivedFrom":subQ5}),-1.0]])]});}
            var Q38;
            {var subQ0=sQuery(id+"F18.wireOp",EDGE,"E151");var subQ1=sQuery(id+"F18.wireOp",EDGE,"E130.4");var subQ2=makeQuery(id+"F18.imprint","INTERSECT",VERTEX,{"derivedFrom":[subQ1,subQ0]});Q38=makeQuery(id+"F18.imprint","IMPRINT",FACE,{"disambiguationData":[TD([[makeQuery(id+"F18.imprint","IMPRINT",EDGE,{"disambiguationData":[TD([[subQ2,-1.0]])],"derivedFrom":subQ1}),-1.0]])]});}
            var Q39;
            Q39=makeQuery(id+"F18.imprint","IMPRINT",FACE,{"disambiguationData":[TD([[makeQuery(id+"F18.imprint","IMPRINT",EDGE,{"derivedFrom":sQuery(id+"F18.wireOp",EDGE,"E142.3")}),1.0]])]});
            var Q40;
            {var subQ0=sQuery(id+"F18.wireOp",EDGE,"E142.2");var subQ1=sQuery(id+"F18.wireOp",EDGE,"E130.0");var subQ2=makeQuery(id+"F18.imprint","INTERSECT",VERTEX,{"derivedFrom":[subQ1,subQ0]});Q40=makeQuery(id+"F18.imprint","IMPRINT",FACE,{"disambiguationData":[TD([[makeQuery(id+"F18.imprint","IMPRINT",EDGE,{"disambiguationData":[TD([[subQ2,-1.0]])],"derivedFrom":subQ1}),-1.0]])]});}
            var Q41;
            {var subQ0=sQuery(id+"F18.wireOp",EDGE,"E154");var subQ1=sQuery(id+"F18.wireOp",EDGE,"E130.0");var subQ2=makeQuery(id+"F18.imprint","INTERSECT",VERTEX,{"derivedFrom":[subQ1,subQ0]});Q41=makeQuery(id+"F18.imprint","IMPRINT",FACE,{"disambiguationData":[TD([[makeQuery(id+"F18.imprint","IMPRINT",EDGE,{"disambiguationData":[TD([[subQ2,-1.0]])],"derivedFrom":subQ1}),-1.0]])]});}
            var Q42;
            {var subQ0=sQuery(id+"F18.wireOp",EDGE,"E164.4");var subQ1=sQuery(id+"F18.wireOp",EDGE,"E130.2");var subQ2=makeQuery(id+"F18.imprint","INTERSECT",VERTEX,{"derivedFrom":[subQ1,subQ0]});Q42=makeQuery(id+"F18.imprint","IMPRINT",FACE,{"disambiguationData":[TD([[makeQuery(id+"F18.imprint","IMPRINT",EDGE,{"disambiguationData":[TD([[subQ2,-1.0]])],"derivedFrom":subQ1}),-1.0]])]});}
            var Q43;
            {var subQ0=sQuery(id+"F18.wireOp",EDGE,"E167");var subQ1=sQuery(id+"F18.wireOp",EDGE,"E130.1");var subQ2=makeQuery(id+"F18.imprint","INTERSECT",VERTEX,{"derivedFrom":[subQ1,subQ0]});Q43=makeQuery(id+"F18.imprint","IMPRINT",FACE,{"disambiguationData":[TD([[makeQuery(id+"F18.imprint","IMPRINT",EDGE,{"disambiguationData":[TD([[subQ2,-1.0]])],"derivedFrom":subQ1}),-1.0]])]});}
            var Q44;
            {var subQ0=sQuery(id+"F18.wireOp",EDGE,"E181");var subQ1=sQuery(id+"F18.wireOp",EDGE,"E130.2");var subQ2=makeQuery(id+"F18.imprint","INTERSECT",VERTEX,{"derivedFrom":[subQ1,subQ0]});Q44=makeQuery(id+"F18.imprint","IMPRINT",FACE,{"disambiguationData":[TD([[makeQuery(id+"F18.imprint","IMPRINT",EDGE,{"disambiguationData":[TD([[subQ2,-1.0]])],"derivedFrom":subQ1}),-1.0]])]});}
            extrude(context, id + "F24", {"entities" : qUnion([Q0, Q1, Q2, Q3, Q4, Q5, Q6, Q7, Q8, Q9, Q10, Q11, Q12, Q13, Q14, Q15, Q16, Q17, Q18, Q19, Q20, Q21, Q22, Q23, Q24, Q25, Q26, Q27, Q28, Q29, Q30, Q31, Q32, Q33, Q34, Q35, Q36, Q37, Q38, Q39, Q40, Q41, Q42, Q43, Q44]), "operationType" : NewBodyOperationType.ADD, "depth" : 0.1 * mm});
        }
        {
            var Q0;
            {var subQ5=sQuery(id+"F23.wireOp",EDGE,"E310");Q0=makeQuery(id+"F23.imprint","IMPRINT",FACE,{"disambiguationData":[TD([[makeQuery(id+"F23.imprint","IMPRINT",EDGE,{"derivedFrom":subQ5}),-1.0]])]});}
            var Q1;
            Q1=makeQuery(id+"F23.imprint","IMPRINT",FACE,{"disambiguationData":[TD([[makeQuery(id+"F23.imprint","IMPRINT",EDGE,{"derivedFrom":sQuery(id+"F23.wireOp",EDGE,"E309.4")}),1.0]])]});
            var Q2;
            Q2=makeQuery(id+"F23.imprint","IMPRINT",FACE,{"disambiguationData":[TD([[makeQuery(id+"F23.imprint","IMPRINT",EDGE,{"derivedFrom":sQuery(id+"F23.wireOp",EDGE,"E309.3")}),1.0]])]});
            var Q3;
            {var subQ5=sQuery(id+"F23.wireOp",EDGE,"E314");Q3=makeQuery(id+"F23.imprint","IMPRINT",FACE,{"disambiguationData":[TD([[makeQuery(id+"F23.imprint","IMPRINT",EDGE,{"derivedFrom":subQ5}),1.0]])]});}
            var Q4;
            {var subQ0=sQuery(id+"F23.wireOp",EDGE,"E315");var subQ1=sQuery(id+"F23.wireOp",EDGE,"E253.5");var subQ2=makeQuery(id+"F23.imprint","INTERSECT",VERTEX,{"derivedFrom":[subQ1,subQ0]});Q4=makeQuery(id+"F23.imprint","IMPRINT",FACE,{"disambiguationData":[TD([[makeQuery(id+"F23.imprint","IMPRINT",EDGE,{"disambiguationData":[TD([[subQ2,-1.0]])],"derivedFrom":subQ1}),-1.0]])]});}
            var Q5;
            Q5=makeQuery(id+"F23.imprint","IMPRINT",FACE,{"disambiguationData":[TD([[makeQuery(id+"F23.imprint","IMPRINT",EDGE,{"derivedFrom":sQuery(id+"F23.wireOp",EDGE,"E309.1")}),1.0]])]});
            var Q6;
            {var subQ0=sQuery(id+"F23.wireOp",EDGE,"E309.1");Q6=makeQuery(id+"F23.imprint","IMPRINT",FACE,{"disambiguationData":[TD([[makeQuery(id+"F23.imprint","IMPRINT",EDGE,{"derivedFrom":subQ0}),-1.0]])]});}
            var Q7;
            {var subQ0=sQuery(id+"F23.wireOp",EDGE,"E309.3");Q7=makeQuery(id+"F23.imprint","IMPRINT",FACE,{"disambiguationData":[TD([[makeQuery(id+"F23.imprint","IMPRINT",EDGE,{"derivedFrom":subQ0}),-1.0]])]});}
            var Q8;
            {var subQ0=sQuery(id+"F23.wireOp",EDGE,"E309.0");var subQ1=sQuery(id+"F23.wireOp",EDGE,"E253.0");var subQ2=makeQuery(id+"F23.imprint","INTERSECT",VERTEX,{"derivedFrom":[subQ1,subQ0]});Q8=makeQuery(id+"F23.imprint","IMPRINT",FACE,{"disambiguationData":[TD([[makeQuery(id+"F23.imprint","IMPRINT",EDGE,{"disambiguationData":[TD([[subQ2,-1.0]])],"derivedFrom":subQ1}),-1.0]])]});}
            var Q9;
            {var subQ5=sQuery(id+"F23.wireOp",EDGE,"E261");Q9=makeQuery(id+"F23.imprint","IMPRINT",FACE,{"disambiguationData":[TD([[makeQuery(id+"F23.imprint","IMPRINT",EDGE,{"derivedFrom":subQ5}),1.0]])]});}
            var Q10;
            {var subQ0=sQuery(id+"F23.wireOp",EDGE,"E262");var subQ1=sQuery(id+"F23.wireOp",EDGE,"E253.0");var subQ2=makeQuery(id+"F23.imprint","INTERSECT",VERTEX,{"derivedFrom":[subQ1,subQ0]});Q10=makeQuery(id+"F23.imprint","IMPRINT",FACE,{"disambiguationData":[TD([[makeQuery(id+"F23.imprint","IMPRINT",EDGE,{"disambiguationData":[TD([[subQ2,-1.0]])],"derivedFrom":subQ1}),-1.0]])]});}
            var Q11;
            Q11=makeQuery(id+"F23.imprint","IMPRINT",FACE,{"disambiguationData":[TD([[makeQuery(id+"F23.imprint","IMPRINT",EDGE,{"derivedFrom":sQuery(id+"F23.wireOp",EDGE,"E254.2")}),1.0]])]});
            var Q12;
            {var subQ0=sQuery(id+"F23.wireOp",EDGE,"E254.1");var subQ1=sQuery(id+"F23.wireOp",EDGE,"E253.1");var subQ2=makeQuery(id+"F23.imprint","INTERSECT",VERTEX,{"derivedFrom":[subQ1,subQ0]});Q12=makeQuery(id+"F23.imprint","IMPRINT",FACE,{"disambiguationData":[TD([[makeQuery(id+"F23.imprint","IMPRINT",EDGE,{"disambiguationData":[TD([[subQ2,-1.0]])],"derivedFrom":subQ1}),-1.0]])]});}
            var Q13;
            {var subQ5=sQuery(id+"F23.wireOp",EDGE,"E257");Q13=makeQuery(id+"F23.imprint","IMPRINT",FACE,{"disambiguationData":[TD([[makeQuery(id+"F23.imprint","IMPRINT",EDGE,{"derivedFrom":subQ5}),-1.0]])]});}
            var Q14;
            Q14=makeQuery(id+"F23.imprint","IMPRINT",FACE,{"disambiguationData":[TD([[makeQuery(id+"F23.imprint","IMPRINT",EDGE,{"derivedFrom":sQuery(id+"F23.wireOp",EDGE,"E254.0")}),1.0]])]});
            var Q15;
            Q15=makeQuery(id+"F23.imprint","IMPRINT",FACE,{"disambiguationData":[TD([[makeQuery(id+"F23.imprint","IMPRINT",EDGE,{"derivedFrom":sQuery(id+"F23.wireOp",EDGE,"E254.4")}),1.0]])]});
            var Q16;
            {var subQ1=sQuery(id+"F23.wireOp",EDGE,"E254.0");Q16=makeQuery(id+"F23.imprint","IMPRINT",FACE,{"disambiguationData":[TD([[makeQuery(id+"F23.imprint","IMPRINT",EDGE,{"derivedFrom":subQ1}),-1.0]])]});}
            var Q17;
            {var subQ0=sQuery(id+"F23.wireOp",EDGE,"E254.2");Q17=makeQuery(id+"F23.imprint","IMPRINT",FACE,{"disambiguationData":[TD([[makeQuery(id+"F23.imprint","IMPRINT",EDGE,{"derivedFrom":subQ0}),-1.0]])]});}
            var Q18;
            {var subQ5=sQuery(id+"F23.wireOp",EDGE,"E275");Q18=makeQuery(id+"F23.imprint","IMPRINT",FACE,{"disambiguationData":[TD([[makeQuery(id+"F23.imprint","IMPRINT",EDGE,{"derivedFrom":subQ5}),-1.0]])]});}
            var Q19;
            {var subQ0=sQuery(id+"F23.wireOp",EDGE,"E274");var subQ1=sQuery(id+"F23.wireOp",EDGE,"E253.1");var subQ2=makeQuery(id+"F23.imprint","INTERSECT",VERTEX,{"derivedFrom":[subQ1,subQ0]});Q19=makeQuery(id+"F23.imprint","IMPRINT",FACE,{"disambiguationData":[TD([[makeQuery(id+"F23.imprint","IMPRINT",EDGE,{"disambiguationData":[TD([[subQ2,-1.0]])],"derivedFrom":subQ1}),-1.0]])]});}
            var Q20;
            Q20=makeQuery(id+"F23.imprint","IMPRINT",FACE,{"disambiguationData":[TD([[makeQuery(id+"F23.imprint","IMPRINT",EDGE,{"derivedFrom":sQuery(id+"F23.wireOp",EDGE,"E265.3")}),1.0]])]});
            var Q21;
            {var subQ5=sQuery(id+"F23.wireOp",EDGE,"E270");Q21=makeQuery(id+"F23.imprint","IMPRINT",FACE,{"disambiguationData":[TD([[makeQuery(id+"F23.imprint","IMPRINT",EDGE,{"derivedFrom":subQ5}),1.0]])]});}
            var Q22;
            {var subQ0=sQuery(id+"F23.wireOp",EDGE,"E265.2");var subQ1=sQuery(id+"F23.wireOp",EDGE,"E253.2");var subQ2=makeQuery(id+"F23.imprint","INTERSECT",VERTEX,{"derivedFrom":[subQ1,subQ0]});Q22=makeQuery(id+"F23.imprint","IMPRINT",FACE,{"disambiguationData":[TD([[makeQuery(id+"F23.imprint","IMPRINT",EDGE,{"disambiguationData":[TD([[subQ2,-1.0]])],"derivedFrom":subQ1}),1.0]])]});}
            var Q23;
            Q23=makeQuery(id+"F23.imprint","IMPRINT",FACE,{"disambiguationData":[TD([[makeQuery(id+"F23.imprint","IMPRINT",EDGE,{"derivedFrom":sQuery(id+"F23.wireOp",EDGE,"E265.1")}),1.0]])]});
            var Q24;
            Q24=makeQuery(id+"F23.imprint","IMPRINT",FACE,{"disambiguationData":[TD([[makeQuery(id+"F23.imprint","IMPRINT",EDGE,{"derivedFrom":sQuery(id+"F23.wireOp",EDGE,"E265.0")}),1.0]])]});
            var Q25;
            {var subQ2=sQuery(id+"F23.wireOp",EDGE,"E265.0");Q25=makeQuery(id+"F23.imprint","IMPRINT",FACE,{"disambiguationData":[TD([[makeQuery(id+"F23.imprint","IMPRINT",EDGE,{"derivedFrom":subQ2}),-1.0]])]});}
            var Q26;
            {var subQ0=sQuery(id+"F23.wireOp",EDGE,"E265.3");Q26=makeQuery(id+"F23.imprint","IMPRINT",FACE,{"disambiguationData":[TD([[makeQuery(id+"F23.imprint","IMPRINT",EDGE,{"derivedFrom":subQ0}),-1.0]])]});}
            var Q27;
            Q27=makeQuery(id+"F23.imprint","IMPRINT",FACE,{"disambiguationData":[TD([[makeQuery(id+"F23.imprint","IMPRINT",EDGE,{"derivedFrom":sQuery(id+"F23.wireOp",EDGE,"E276.4")}),1.0]])]});
            var Q28;
            {var subQ5=sQuery(id+"F23.wireOp",EDGE,"E283");Q28=makeQuery(id+"F23.imprint","IMPRINT",FACE,{"disambiguationData":[TD([[makeQuery(id+"F23.imprint","IMPRINT",EDGE,{"derivedFrom":subQ5}),1.0]])]});}
            var Q29;
            {var subQ0=sQuery(id+"F23.wireOp",EDGE,"E276.3");var subQ1=sQuery(id+"F23.wireOp",EDGE,"E253.3");var subQ2=makeQuery(id+"F23.imprint","INTERSECT",VERTEX,{"derivedFrom":[subQ1,subQ0]});Q29=makeQuery(id+"F23.imprint","IMPRINT",FACE,{"disambiguationData":[TD([[makeQuery(id+"F23.imprint","IMPRINT",EDGE,{"disambiguationData":[TD([[subQ2,-1.0]])],"derivedFrom":subQ1}),1.0]])]});}
            var Q30;
            Q30=makeQuery(id+"F23.imprint","IMPRINT",FACE,{"disambiguationData":[TD([[makeQuery(id+"F23.imprint","IMPRINT",EDGE,{"derivedFrom":sQuery(id+"F23.wireOp",EDGE,"E276.2")}),1.0]])]});
            var Q31;
            Q31=makeQuery(id+"F23.imprint","IMPRINT",FACE,{"disambiguationData":[TD([[makeQuery(id+"F23.imprint","IMPRINT",EDGE,{"derivedFrom":sQuery(id+"F23.wireOp",EDGE,"E276.1")}),1.0]])]});
            var Q32;
            {var subQ5=sQuery(id+"F23.wireOp",EDGE,"E278");Q32=makeQuery(id+"F23.imprint","IMPRINT",FACE,{"disambiguationData":[TD([[makeQuery(id+"F23.imprint","IMPRINT",EDGE,{"derivedFrom":subQ5}),-1.0]])]});}
            var Q33;
            {var subQ0=sQuery(id+"F23.wireOp",EDGE,"E276.4");Q33=makeQuery(id+"F23.imprint","IMPRINT",FACE,{"disambiguationData":[TD([[makeQuery(id+"F23.imprint","IMPRINT",EDGE,{"derivedFrom":subQ0}),-1.0]])]});}
            var Q34;
            {var subQ0=sQuery(id+"F23.wireOp",EDGE,"E276.1");Q34=makeQuery(id+"F23.imprint","IMPRINT",FACE,{"disambiguationData":[TD([[makeQuery(id+"F23.imprint","IMPRINT",EDGE,{"derivedFrom":subQ0}),-1.0]])]});}
            var Q35;
            Q35=makeQuery(id+"F23.imprint","IMPRINT",FACE,{"disambiguationData":[TD([[makeQuery(id+"F23.imprint","IMPRINT",EDGE,{"derivedFrom":sQuery(id+"F23.wireOp",EDGE,"E287.1")}),1.0]])]});
            var Q36;
            Q36=makeQuery(id+"F23.imprint","IMPRINT",FACE,{"disambiguationData":[TD([[makeQuery(id+"F23.imprint","IMPRINT",EDGE,{"derivedFrom":sQuery(id+"F23.wireOp",EDGE,"E287.2")}),1.0]])]});
            var Q37;
            Q37=makeQuery(id+"F23.imprint","IMPRINT",FACE,{"disambiguationData":[TD([[makeQuery(id+"F23.imprint","IMPRINT",EDGE,{"derivedFrom":sQuery(id+"F23.wireOp",EDGE,"E287.3")}),1.0]])]});
            var Q38;
            {var subQ0=sQuery(id+"F23.wireOp",EDGE,"E287.4");var subQ1=sQuery(id+"F23.wireOp",EDGE,"E253.4");var subQ2=makeQuery(id+"F23.imprint","INTERSECT",VERTEX,{"derivedFrom":[subQ1,subQ0]});Q38=makeQuery(id+"F23.imprint","IMPRINT",FACE,{"disambiguationData":[TD([[makeQuery(id+"F23.imprint","IMPRINT",EDGE,{"disambiguationData":[TD([[subQ2,-1.0]])],"derivedFrom":subQ1}),1.0]])]});}
            var Q39;
            {var subQ5=sQuery(id+"F23.wireOp",EDGE,"E297");Q39=makeQuery(id+"F23.imprint","IMPRINT",FACE,{"disambiguationData":[TD([[makeQuery(id+"F23.imprint","IMPRINT",EDGE,{"derivedFrom":subQ5}),-1.0]])]});}
            var Q40;
            {var subQ5=sQuery(id+"F23.wireOp",EDGE,"E288");Q40=makeQuery(id+"F23.imprint","IMPRINT",FACE,{"disambiguationData":[TD([[makeQuery(id+"F23.imprint","IMPRINT",EDGE,{"derivedFrom":subQ5}),-1.0]])]});}
            var Q41;
            {var subQ0=sQuery(id+"F23.wireOp",EDGE,"E253.4");var subQ1=sQuery(id+"F23.wireOp",EDGE,"E253.3");var subQ2=makeQuery(id+"F23.imprint","INTERSECT",VERTEX,{"derivedFrom":[subQ1,subQ0]});Q41=makeQuery(id+"F23.imprint","IMPRINT",FACE,{"disambiguationData":[TD([[makeQuery(id+"F23.imprint","IMPRINT",EDGE,{"disambiguationData":[TD([[subQ2,1.0]])],"derivedFrom":subQ1}),-1.0]])]});}
            var Q42;
            {var subQ0=sQuery(id+"F23.wireOp",EDGE,"E287.1");Q42=makeQuery(id+"F23.imprint","IMPRINT",FACE,{"disambiguationData":[TD([[makeQuery(id+"F23.imprint","IMPRINT",EDGE,{"derivedFrom":subQ0}),-1.0]])]});}
            var Q43;
            {var subQ5=sQuery(id+"F23.wireOp",EDGE,"E301");Q43=makeQuery(id+"F23.imprint","IMPRINT",FACE,{"disambiguationData":[TD([[makeQuery(id+"F23.imprint","IMPRINT",EDGE,{"derivedFrom":subQ5}),-1.0]])]});}
            var Q44;
            {var subQ0=sQuery(id+"F23.wireOp",EDGE,"E302");var subQ1=sQuery(id+"F23.wireOp",EDGE,"E253.4");var subQ2=makeQuery(id+"F23.imprint","INTERSECT",VERTEX,{"derivedFrom":[subQ1,subQ0]});Q44=makeQuery(id+"F23.imprint","IMPRINT",FACE,{"disambiguationData":[TD([[makeQuery(id+"F23.imprint","IMPRINT",EDGE,{"disambiguationData":[TD([[subQ2,-1.0]])],"derivedFrom":subQ1}),1.0]])]});}
            var Q45;
            Q45=makeQuery(id+"F23.imprint","IMPRINT",FACE,{"disambiguationData":[TD([[makeQuery(id+"F23.imprint","IMPRINT",EDGE,{"derivedFrom":sQuery(id+"F23.wireOp",EDGE,"E298.2")}),1.0]])]});
            var Q46;
            Q46=makeQuery(id+"F23.imprint","IMPRINT",FACE,{"disambiguationData":[TD([[makeQuery(id+"F23.imprint","IMPRINT",EDGE,{"derivedFrom":sQuery(id+"F23.wireOp",EDGE,"E298.3")}),1.0]])]});
            var Q47;
            {var subQ5=sQuery(id+"F23.wireOp",EDGE,"E307");Q47=makeQuery(id+"F23.imprint","IMPRINT",FACE,{"disambiguationData":[TD([[makeQuery(id+"F23.imprint","IMPRINT",EDGE,{"derivedFrom":subQ5}),-1.0]])]});}
            var Q48;
            Q48=makeQuery(id+"F23.imprint","IMPRINT",FACE,{"disambiguationData":[TD([[makeQuery(id+"F23.imprint","IMPRINT",EDGE,{"derivedFrom":sQuery(id+"F23.wireOp",EDGE,"E298.0")}),1.0]])]});
            var Q49;
            {var subQ1=sQuery(id+"F23.wireOp",EDGE,"E298.0");Q49=makeQuery(id+"F23.imprint","IMPRINT",FACE,{"disambiguationData":[TD([[makeQuery(id+"F23.imprint","IMPRINT",EDGE,{"derivedFrom":subQ1}),-1.0]])]});}
            var Q50;
            {var subQ0=sQuery(id+"F23.wireOp",EDGE,"E298.2");Q50=makeQuery(id+"F23.imprint","IMPRINT",FACE,{"disambiguationData":[TD([[makeQuery(id+"F23.imprint","IMPRINT",EDGE,{"derivedFrom":subQ0}),-1.0]])]});}
            extrude(context, id + "F25", {"entities" : qUnion([Q0, Q1, Q2, Q3, Q4, Q5, Q6, Q7, Q8, Q9, Q10, Q11, Q12, Q13, Q14, Q15, Q16, Q17, Q18, Q19, Q20, Q21, Q22, Q23, Q24, Q25, Q26, Q27, Q28, Q29, Q30, Q31, Q32, Q33, Q34, Q35, Q36, Q37, Q38, Q39, Q40, Q41, Q42, Q43, Q44, Q45, Q46, Q47, Q48, Q49, Q50]), "operationType" : NewBodyOperationType.ADD, "depth" : 0.1 * mm});
        }
        {
            var Q0;
            Q0=makeQuery(id+"F17.imprint","IMPRINT",FACE,{"disambiguationData":[TD([[makeQuery(id+"F17.imprint","IMPRINT",EDGE,{"derivedFrom":sQuery(id+"F17.wireOp",EDGE,"E97.0")}),1.0]])]});
            var Q1;
            Q1=makeQuery(id+"F17.imprint","IMPRINT",FACE,{"disambiguationData":[TD([[makeQuery(id+"F17.imprint","IMPRINT",EDGE,{"derivedFrom":sQuery(id+"F17.wireOp",EDGE,"E97.4")}),1.0]])]});
            var Q2;
            Q2=makeQuery(id+"F17.imprint","IMPRINT",FACE,{"disambiguationData":[TD([[makeQuery(id+"F17.imprint","IMPRINT",EDGE,{"derivedFrom":sQuery(id+"F17.wireOp",EDGE,"E97.3")}),1.0]])]});
            var Q3;
            {var subQ5=sQuery(id+"F17.wireOp",EDGE,"E103");Q3=makeQuery(id+"F17.imprint","IMPRINT",FACE,{"disambiguationData":[TD([[makeQuery(id+"F17.imprint","IMPRINT",EDGE,{"derivedFrom":subQ5}),1.0]])]});}
            var Q4;
            {var subQ0=sQuery(id+"F17.wireOp",EDGE,"E97.2");var subQ1=sQuery(id+"F17.wireOp",EDGE,"E85.left");var subQ2=makeQuery(id+"F17.imprint","INTERSECT",VERTEX,{"derivedFrom":[subQ1,subQ0]});Q4=makeQuery(id+"F17.imprint","IMPRINT",FACE,{"disambiguationData":[TD([[makeQuery(id+"F17.imprint","IMPRINT",EDGE,{"disambiguationData":[TD([[subQ2,-1.0]])],"derivedFrom":subQ1}),-1.0]])]});}
            var Q5;
            {var subQ1=sQuery(id+"F17.wireOp",EDGE,"E97.0");Q5=makeQuery(id+"F17.imprint","IMPRINT",FACE,{"disambiguationData":[TD([[makeQuery(id+"F17.imprint","IMPRINT",EDGE,{"derivedFrom":subQ1}),-1.0]])]});}
            var Q6;
            {var subQ0=sQuery(id+"F17.wireOp",EDGE,"E85.left");var subQ1=sQuery(id+"F17.wireOp",EDGE,"E85.bottom");var subQ2=makeQuery(id+"F17.imprint","INTERSECT",VERTEX,{"derivedFrom":[subQ1,subQ0]});Q6=makeQuery(id+"F17.imprint","IMPRINT",FACE,{"disambiguationData":[TD([[makeQuery(id+"F17.imprint","IMPRINT",EDGE,{"disambiguationData":[TD([[subQ2,-1.0]])],"derivedFrom":subQ1}),-1.0]])]});}
            var Q7;
            {var subQ0=sQuery(id+"F17.wireOp",EDGE,"E101");Q7=makeQuery(id+"F17.imprint","IMPRINT",FACE,{"disambiguationData":[TD([[makeQuery(id+"F17.imprint","IMPRINT",EDGE,{"derivedFrom":subQ0}),-1.0]])]});}
            var Q8;
            {var subQ0=sQuery(id+"F17.wireOp",EDGE,"E100");Q8=makeQuery(id+"F17.imprint","IMPRINT",FACE,{"disambiguationData":[TD([[makeQuery(id+"F17.imprint","IMPRINT",EDGE,{"derivedFrom":subQ0}),-1.0]])]});}
            var Q9;
            Q9=makeQuery(id+"F17.imprint","IMPRINT",FACE,{"disambiguationData":[TD([[makeQuery(id+"F17.imprint","IMPRINT",EDGE,{"derivedFrom":sQuery(id+"F17.wireOp",EDGE,"E86.4")}),1.0]])]});
            var Q10;
            Q10=makeQuery(id+"F17.imprint","IMPRINT",FACE,{"disambiguationData":[TD([[makeQuery(id+"F17.imprint","IMPRINT",EDGE,{"derivedFrom":sQuery(id+"F17.wireOp",EDGE,"E86.0")}),-1.0]])]});
            var Q11;
            Q11=makeQuery(id+"F17.imprint","IMPRINT",FACE,{"disambiguationData":[TD([[makeQuery(id+"F17.imprint","IMPRINT",EDGE,{"derivedFrom":sQuery(id+"F17.wireOp",EDGE,"E86.0")}),1.0]])]});
            var Q12;
            Q12=makeQuery(id+"F17.imprint","IMPRINT",FACE,{"disambiguationData":[TD([[makeQuery(id+"F17.imprint","IMPRINT",EDGE,{"derivedFrom":sQuery(id+"F17.wireOp",EDGE,"E86.1")}),1.0]])]});
            var Q13;
            {var subQ5=sQuery(id+"F17.wireOp",EDGE,"E92");Q13=makeQuery(id+"F17.imprint","IMPRINT",FACE,{"disambiguationData":[TD([[makeQuery(id+"F17.imprint","IMPRINT",EDGE,{"derivedFrom":subQ5}),1.0]])]});}
            var Q14;
            {var subQ3=sQuery(id+"F17.wireOp",EDGE,"E86.3");Q14=makeQuery(id+"F17.imprint","IMPRINT",FACE,{"disambiguationData":[TD([[makeQuery(id+"F17.imprint","IMPRINT",EDGE,{"derivedFrom":subQ3}),-1.0]])]});}
            var Q15;
            Q15=makeQuery(id+"F17.imprint","IMPRINT",FACE,{"disambiguationData":[TD([[makeQuery(id+"F17.imprint","IMPRINT",EDGE,{"derivedFrom":sQuery(id+"F17.wireOp",EDGE,"E86.3")}),1.0]])]});
            var Q16;
            {var subQ0=sQuery(id+"F17.wireOp",EDGE,"E86.2");var subQ1=sQuery(id+"F17.wireOp",EDGE,"E85.right");var subQ2=makeQuery(id+"F17.imprint","INTERSECT",VERTEX,{"derivedFrom":[subQ1,subQ0]});Q16=makeQuery(id+"F17.imprint","IMPRINT",FACE,{"disambiguationData":[TD([[makeQuery(id+"F17.imprint","IMPRINT",EDGE,{"disambiguationData":[TD([[subQ2,-1.0]])],"derivedFrom":subQ1}),-1.0]])]});}
            var Q17;
            {var subQ5=sQuery(id+"F17.wireOp",EDGE,"E121");Q17=makeQuery(id+"F17.imprint","IMPRINT",FACE,{"disambiguationData":[TD([[makeQuery(id+"F17.imprint","IMPRINT",EDGE,{"derivedFrom":subQ5}),-1.0]])]});}
            var Q18;
            {var subQ0=sQuery(id+"F17.wireOp",EDGE,"E120");var subQ1=sQuery(id+"F17.wireOp",EDGE,"E85.right");var subQ2=makeQuery(id+"F17.imprint","INTERSECT",VERTEX,{"derivedFrom":[subQ1,subQ0]});Q18=makeQuery(id+"F17.imprint","IMPRINT",FACE,{"disambiguationData":[TD([[makeQuery(id+"F17.imprint","IMPRINT",EDGE,{"disambiguationData":[TD([[subQ2,-1.0]])],"derivedFrom":subQ1}),-1.0]])]});}
            var Q19;
            Q19=makeQuery(id+"F17.imprint","IMPRINT",FACE,{"disambiguationData":[TD([[makeQuery(id+"F17.imprint","IMPRINT",EDGE,{"derivedFrom":sQuery(id+"F17.wireOp",EDGE,"E119.4")}),1.0]])]});
            var Q20;
            Q20=makeQuery(id+"F17.imprint","IMPRINT",FACE,{"disambiguationData":[TD([[makeQuery(id+"F17.imprint","IMPRINT",EDGE,{"derivedFrom":sQuery(id+"F17.wireOp",EDGE,"E119.3")}),1.0]])]});
            var Q21;
            Q21=makeQuery(id+"F17.imprint","IMPRINT",FACE,{"disambiguationData":[TD([[makeQuery(id+"F17.imprint","IMPRINT",EDGE,{"derivedFrom":sQuery(id+"F17.wireOp",EDGE,"E119.2")}),1.0]])]});
            var Q22;
            Q22=makeQuery(id+"F17.imprint","IMPRINT",FACE,{"disambiguationData":[TD([[makeQuery(id+"F17.imprint","IMPRINT",EDGE,{"derivedFrom":sQuery(id+"F17.wireOp",EDGE,"E119.1")}),1.0]])]});
            var Q23;
            {var subQ0=sQuery(id+"F17.wireOp",EDGE,"E119.1");Q23=makeQuery(id+"F17.imprint","IMPRINT",FACE,{"disambiguationData":[TD([[makeQuery(id+"F17.imprint","IMPRINT",EDGE,{"derivedFrom":subQ0}),-1.0]])]});}
            var Q24;
            {var subQ3=sQuery(id+"F17.wireOp",EDGE,"E119.4");Q24=makeQuery(id+"F17.imprint","IMPRINT",FACE,{"disambiguationData":[TD([[makeQuery(id+"F17.imprint","IMPRINT",EDGE,{"derivedFrom":subQ3}),-1.0]])]});}
            var Q25;
            Q25=makeQuery(id+"F17.imprint","IMPRINT",FACE,{"disambiguationData":[TD([[makeQuery(id+"F17.imprint","IMPRINT",EDGE,{"derivedFrom":sQuery(id+"F17.wireOp",EDGE,"E119.4")}),1.0]])]});
            var Q26;
            {var subQ5=sQuery(id+"F17.wireOp",EDGE,"E110");Q26=makeQuery(id+"F17.imprint","IMPRINT",FACE,{"disambiguationData":[TD([[makeQuery(id+"F17.imprint","IMPRINT",EDGE,{"derivedFrom":subQ5}),-1.0]])]});}
            var Q27;
            {var subQ0=sQuery(id+"F17.wireOp",EDGE,"E85.left");var subQ1=sQuery(id+"F17.wireOp",EDGE,"E85.top");var subQ2=makeQuery(id+"F17.imprint","INTERSECT",VERTEX,{"derivedFrom":[subQ1,subQ0]});Q27=makeQuery(id+"F17.imprint","IMPRINT",FACE,{"disambiguationData":[TD([[makeQuery(id+"F17.imprint","IMPRINT",EDGE,{"disambiguationData":[TD([[subQ2,-1.0]])],"derivedFrom":subQ1}),1.0]])]});}
            var Q28;
            {var subQ0=sQuery(id+"F17.wireOp",EDGE,"E111");Q28=makeQuery(id+"F17.imprint","IMPRINT",FACE,{"disambiguationData":[TD([[makeQuery(id+"F17.imprint","IMPRINT",EDGE,{"derivedFrom":subQ0}),-1.0]])]});}
            var Q29;
            {var subQ0=sQuery(id+"F17.wireOp",EDGE,"E112");Q29=makeQuery(id+"F17.imprint","IMPRINT",FACE,{"disambiguationData":[TD([[makeQuery(id+"F17.imprint","IMPRINT",EDGE,{"derivedFrom":subQ0}),-1.0]])]});}
            var Q30;
            {var subQ0=sQuery(id+"F17.wireOp",EDGE,"E108.2");Q30=makeQuery(id+"F17.imprint","IMPRINT",FACE,{"disambiguationData":[TD([[makeQuery(id+"F17.imprint","IMPRINT",EDGE,{"derivedFrom":subQ0}),-1.0]])]});}
            var Q31;
            Q31=makeQuery(id+"F17.imprint","IMPRINT",FACE,{"disambiguationData":[TD([[makeQuery(id+"F17.imprint","IMPRINT",EDGE,{"derivedFrom":sQuery(id+"F17.wireOp",EDGE,"E108.2")}),1.0]])]});
            var Q32;
            Q32=makeQuery(id+"F17.imprint","IMPRINT",FACE,{"disambiguationData":[TD([[makeQuery(id+"F17.imprint","IMPRINT",EDGE,{"derivedFrom":sQuery(id+"F17.wireOp",EDGE,"E108.3")}),1.0]])]});
            var Q33;
            Q33=makeQuery(id+"F17.imprint","IMPRINT",FACE,{"disambiguationData":[TD([[makeQuery(id+"F17.imprint","IMPRINT",EDGE,{"derivedFrom":sQuery(id+"F17.wireOp",EDGE,"E108.4")}),1.0]])]});
            var Q34;
            {var subQ0=sQuery(id+"F17.wireOp",EDGE,"E109");var subQ1=sQuery(id+"F17.wireOp",EDGE,"E85.left");var subQ2=makeQuery(id+"F17.imprint","INTERSECT",VERTEX,{"derivedFrom":[subQ1,subQ0]});Q34=makeQuery(id+"F17.imprint","IMPRINT",FACE,{"disambiguationData":[TD([[makeQuery(id+"F17.imprint","IMPRINT",EDGE,{"disambiguationData":[TD([[subQ2,-1.0]])],"derivedFrom":subQ1}),-1.0]])]});}
            extrude(context, id + "F26", {"entities" : qUnion([Q0, Q1, Q2, Q3, Q4, Q5, Q6, Q7, Q8, Q9, Q10, Q11, Q12, Q13, Q14, Q15, Q16, Q17, Q18, Q19, Q20, Q21, Q22, Q23, Q24, Q25, Q26, Q27, Q28, Q29, Q30, Q31, Q32, Q33, Q34]), "operationType" : NewBodyOperationType.ADD, "depth" : 0.1 * mm});
        }
        {
            var Q0;
            Q0=makeQuery(id+"F19.imprint","IMPRINT",FACE,{"disambiguationData":[TD([[makeQuery(id+"F19.imprint","IMPRINT",EDGE,{"derivedFrom":sQuery(id+"F19.wireOp",EDGE,"E186.0")}),-1.0]])]});
            var Q1;
            {var subQ0=sQuery(id+"F19.wireOp",EDGE,"E231.2");Q1=makeQuery(id+"F19.imprint","IMPRINT",FACE,{"disambiguationData":[TD([[makeQuery(id+"F19.imprint","IMPRINT",EDGE,{"derivedFrom":subQ0}),-1.0]])]});}
            var Q2;
            {var subQ0=sQuery(id+"F19.wireOp",EDGE,"E197.4");var subQ1=sQuery(id+"F19.wireOp",EDGE,"E197.3");var subQ2=makeQuery(id+"F19.imprint","INTERSECT",VERTEX,{"derivedFrom":[subQ1,subQ0]});Q2=makeQuery(id+"F19.imprint","IMPRINT",FACE,{"disambiguationData":[TD([[makeQuery(id+"F19.imprint","IMPRINT",EDGE,{"disambiguationData":[TD([[subQ2,1.0]])],"derivedFrom":subQ1}),-1.0]])]});}
            var Q3;
            {var subQ0=sQuery(id+"F19.wireOp",EDGE,"E242.0");Q3=makeQuery(id+"F19.imprint","IMPRINT",FACE,{"disambiguationData":[TD([[makeQuery(id+"F19.imprint","IMPRINT",EDGE,{"derivedFrom":subQ0}),-1.0]])]});}
            var Q4;
            {var subQ0=sQuery(id+"F19.wireOp",EDGE,"E197.4");var subQ1=sQuery(id+"F19.wireOp",EDGE,"E197.0");var subQ2=makeQuery(id+"F19.imprint","INTERSECT",VERTEX,{"derivedFrom":[subQ1,subQ0]});Q4=makeQuery(id+"F19.imprint","IMPRINT",FACE,{"disambiguationData":[TD([[makeQuery(id+"F19.imprint","IMPRINT",EDGE,{"disambiguationData":[TD([[subQ2,-1.0]])],"derivedFrom":subQ1}),-1.0]])]});}
            var Q5;
            {var subQ0=sQuery(id+"F19.wireOp",EDGE,"E197.1");var subQ1=sQuery(id+"F19.wireOp",EDGE,"E197.0");var subQ2=makeQuery(id+"F19.imprint","INTERSECT",VERTEX,{"derivedFrom":[subQ1,subQ0]});Q5=makeQuery(id+"F19.imprint","IMPRINT",FACE,{"disambiguationData":[TD([[makeQuery(id+"F19.imprint","IMPRINT",EDGE,{"disambiguationData":[TD([[subQ2,1.0]])],"derivedFrom":subQ1}),-1.0]])]});}
            var Q6;
            Q6=makeQuery(id+"F19.imprint","IMPRINT",FACE,{"disambiguationData":[TD([[makeQuery(id+"F19.imprint","IMPRINT",EDGE,{"derivedFrom":sQuery(id+"F19.wireOp",EDGE,"E198.0")}),-1.0]])]});
            var Q7;
            {var subQ0=sQuery(id+"F19.wireOp",EDGE,"E197.2");var subQ1=sQuery(id+"F19.wireOp",EDGE,"E197.1");var subQ2=makeQuery(id+"F19.imprint","INTERSECT",VERTEX,{"derivedFrom":[subQ1,subQ0]});Q7=makeQuery(id+"F19.imprint","IMPRINT",FACE,{"disambiguationData":[TD([[makeQuery(id+"F19.imprint","IMPRINT",EDGE,{"disambiguationData":[TD([[subQ2,1.0]])],"derivedFrom":subQ1}),-1.0]])]});}
            var Q8;
            {var subQ5=sQuery(id+"F19.wireOp",EDGE,"E209.0");Q8=makeQuery(id+"F19.imprint","IMPRINT",FACE,{"disambiguationData":[TD([[makeQuery(id+"F19.imprint","IMPRINT",EDGE,{"derivedFrom":subQ5}),-1.0]])]});}
            var Q9;
            {var subQ0=sQuery(id+"F19.wireOp",EDGE,"E197.3");var subQ1=sQuery(id+"F19.wireOp",EDGE,"E197.2");var subQ2=makeQuery(id+"F19.imprint","INTERSECT",VERTEX,{"derivedFrom":[subQ1,subQ0]});Q9=makeQuery(id+"F19.imprint","IMPRINT",FACE,{"disambiguationData":[TD([[makeQuery(id+"F19.imprint","IMPRINT",EDGE,{"disambiguationData":[TD([[subQ2,1.0]])],"derivedFrom":subQ1}),-1.0]])]});}
            var Q10;
            {var subQ0=sQuery(id+"F19.wireOp",EDGE,"E220.1");Q10=makeQuery(id+"F19.imprint","IMPRINT",FACE,{"disambiguationData":[TD([[makeQuery(id+"F19.imprint","IMPRINT",EDGE,{"derivedFrom":subQ0}),-1.0]])]});}
            var Q11;
            Q11=makeQuery(id+"F19.imprint","IMPRINT",FACE,{"disambiguationData":[TD([[makeQuery(id+"F19.imprint","IMPRINT",EDGE,{"derivedFrom":sQuery(id+"F19.wireOp",EDGE,"E220.3")}),1.0]])]});
            var Q12;
            Q12=makeQuery(id+"F19.imprint","IMPRINT",FACE,{"disambiguationData":[TD([[makeQuery(id+"F19.imprint","IMPRINT",EDGE,{"derivedFrom":sQuery(id+"F19.wireOp",EDGE,"E220.2")}),1.0]])]});
            var Q13;
            Q13=makeQuery(id+"F19.imprint","IMPRINT",FACE,{"disambiguationData":[TD([[makeQuery(id+"F19.imprint","IMPRINT",EDGE,{"derivedFrom":sQuery(id+"F19.wireOp",EDGE,"E220.1")}),1.0]])]});
            var Q14;
            {var subQ0=sQuery(id+"F19.wireOp",EDGE,"E222");var subQ1=sQuery(id+"F19.wireOp",EDGE,"E197.2");var subQ2=makeQuery(id+"F19.imprint","INTERSECT",VERTEX,{"derivedFrom":[subQ1,subQ0]});Q14=makeQuery(id+"F19.imprint","IMPRINT",FACE,{"disambiguationData":[TD([[makeQuery(id+"F19.imprint","IMPRINT",EDGE,{"disambiguationData":[TD([[subQ2,-1.0]])],"derivedFrom":subQ1}),1.0]])]});}
            var Q15;
            {var subQ5=sQuery(id+"F19.wireOp",EDGE,"E221");Q15=makeQuery(id+"F19.imprint","IMPRINT",FACE,{"disambiguationData":[TD([[makeQuery(id+"F19.imprint","IMPRINT",EDGE,{"derivedFrom":subQ5}),-1.0]])]});}
            var Q16;
            {var subQ5=sQuery(id+"F19.wireOp",EDGE,"E230");Q16=makeQuery(id+"F19.imprint","IMPRINT",FACE,{"disambiguationData":[TD([[makeQuery(id+"F19.imprint","IMPRINT",EDGE,{"derivedFrom":subQ5}),-1.0]])]});}
            var Q17;
            {var subQ0=sQuery(id+"F19.wireOp",EDGE,"E220.4");var subQ1=sQuery(id+"F19.wireOp",EDGE,"E197.3");var subQ2=makeQuery(id+"F19.imprint","INTERSECT",VERTEX,{"derivedFrom":[subQ1,subQ0]});Q17=makeQuery(id+"F19.imprint","IMPRINT",FACE,{"disambiguationData":[TD([[makeQuery(id+"F19.imprint","IMPRINT",EDGE,{"disambiguationData":[TD([[subQ2,-1.0]])],"derivedFrom":subQ1}),1.0]])]});}
            var Q18;
            {var subQ5=sQuery(id+"F19.wireOp",EDGE,"E234");Q18=makeQuery(id+"F19.imprint","IMPRINT",FACE,{"disambiguationData":[TD([[makeQuery(id+"F19.imprint","IMPRINT",EDGE,{"derivedFrom":subQ5}),-1.0]])]});}
            var Q19;
            {var subQ0=sQuery(id+"F19.wireOp",EDGE,"E235");var subQ1=sQuery(id+"F19.wireOp",EDGE,"E197.3");var subQ2=makeQuery(id+"F19.imprint","INTERSECT",VERTEX,{"derivedFrom":[subQ1,subQ0]});Q19=makeQuery(id+"F19.imprint","IMPRINT",FACE,{"disambiguationData":[TD([[makeQuery(id+"F19.imprint","IMPRINT",EDGE,{"disambiguationData":[TD([[subQ2,-1.0]])],"derivedFrom":subQ1}),1.0]])]});}
            var Q20;
            Q20=makeQuery(id+"F19.imprint","IMPRINT",FACE,{"disambiguationData":[TD([[makeQuery(id+"F19.imprint","IMPRINT",EDGE,{"derivedFrom":sQuery(id+"F19.wireOp",EDGE,"E231.2")}),1.0]])]});
            var Q21;
            Q21=makeQuery(id+"F19.imprint","IMPRINT",FACE,{"disambiguationData":[TD([[makeQuery(id+"F19.imprint","IMPRINT",EDGE,{"derivedFrom":sQuery(id+"F19.wireOp",EDGE,"E231.3")}),1.0]])]});
            var Q22;
            Q22=makeQuery(id+"F19.imprint","IMPRINT",FACE,{"disambiguationData":[TD([[makeQuery(id+"F19.imprint","IMPRINT",EDGE,{"derivedFrom":sQuery(id+"F19.wireOp",EDGE,"E231.4")}),1.0]])]});
            var Q23;
            {var subQ0=sQuery(id+"F19.wireOp",EDGE,"E231.0");var subQ1=sQuery(id+"F19.wireOp",EDGE,"E197.4");var subQ2=makeQuery(id+"F19.imprint","INTERSECT",VERTEX,{"derivedFrom":[subQ1,subQ0]});Q23=makeQuery(id+"F19.imprint","IMPRINT",FACE,{"disambiguationData":[TD([[makeQuery(id+"F19.imprint","IMPRINT",EDGE,{"disambiguationData":[TD([[subQ2,-1.0]])],"derivedFrom":subQ1}),1.0]])]});}
            var Q24;
            {var subQ5=sQuery(id+"F19.wireOp",EDGE,"E233");Q24=makeQuery(id+"F19.imprint","IMPRINT",FACE,{"disambiguationData":[TD([[makeQuery(id+"F19.imprint","IMPRINT",EDGE,{"derivedFrom":subQ5}),-1.0]])]});}
            var Q25;
            Q25=makeQuery(id+"F19.imprint","IMPRINT",FACE,{"disambiguationData":[TD([[makeQuery(id+"F19.imprint","IMPRINT",EDGE,{"derivedFrom":sQuery(id+"F19.wireOp",EDGE,"E242.3")}),1.0]])]});
            var Q26;
            Q26=makeQuery(id+"F19.imprint","IMPRINT",FACE,{"disambiguationData":[TD([[makeQuery(id+"F19.imprint","IMPRINT",EDGE,{"derivedFrom":sQuery(id+"F19.wireOp",EDGE,"E242.4")}),1.0]])]});
            var Q27;
            Q27=makeQuery(id+"F19.imprint","IMPRINT",FACE,{"disambiguationData":[TD([[makeQuery(id+"F19.imprint","IMPRINT",EDGE,{"derivedFrom":sQuery(id+"F19.wireOp",EDGE,"E242.0")}),1.0]])]});
            var Q28;
            {var subQ5=sQuery(id+"F19.wireOp",EDGE,"E248");Q28=makeQuery(id+"F19.imprint","IMPRINT",FACE,{"disambiguationData":[TD([[makeQuery(id+"F19.imprint","IMPRINT",EDGE,{"derivedFrom":subQ5}),1.0]])]});}
            var Q29;
            {var subQ0=sQuery(id+"F19.wireOp",EDGE,"E247");var subQ1=sQuery(id+"F19.wireOp",EDGE,"E197.4");var subQ2=makeQuery(id+"F19.imprint","INTERSECT",VERTEX,{"derivedFrom":[subQ1,subQ0]});Q29=makeQuery(id+"F19.imprint","IMPRINT",FACE,{"disambiguationData":[TD([[makeQuery(id+"F19.imprint","IMPRINT",EDGE,{"disambiguationData":[TD([[subQ2,-1.0]])],"derivedFrom":subQ1}),1.0]])]});}
            var Q30;
            Q30=makeQuery(id+"F19.imprint","IMPRINT",FACE,{"disambiguationData":[TD([[makeQuery(id+"F19.imprint","IMPRINT",EDGE,{"derivedFrom":sQuery(id+"F19.wireOp",EDGE,"E198.4")}),1.0]])]});
            var Q31;
            {var subQ0=sQuery(id+"F19.wireOp",EDGE,"E205");var subQ1=sQuery(id+"F19.wireOp",EDGE,"E197.0");var subQ2=makeQuery(id+"F19.imprint","INTERSECT",VERTEX,{"derivedFrom":[subQ1,subQ0]});Q31=makeQuery(id+"F19.imprint","IMPRINT",FACE,{"disambiguationData":[TD([[makeQuery(id+"F19.imprint","IMPRINT",EDGE,{"disambiguationData":[TD([[subQ2,-1.0]])],"derivedFrom":subQ1}),1.0]])]});}
            var Q32;
            {var subQ5=sQuery(id+"F19.wireOp",EDGE,"E206");Q32=makeQuery(id+"F19.imprint","IMPRINT",FACE,{"disambiguationData":[TD([[makeQuery(id+"F19.imprint","IMPRINT",EDGE,{"derivedFrom":subQ5}),1.0]])]});}
            var Q33;
            {var subQ5=sQuery(id+"F19.wireOp",EDGE,"E203");Q33=makeQuery(id+"F19.imprint","IMPRINT",FACE,{"disambiguationData":[TD([[makeQuery(id+"F19.imprint","IMPRINT",EDGE,{"derivedFrom":subQ5}),1.0]])]});}
            var Q34;
            Q34=makeQuery(id+"F19.imprint","IMPRINT",FACE,{"disambiguationData":[TD([[makeQuery(id+"F19.imprint","IMPRINT",EDGE,{"derivedFrom":sQuery(id+"F19.wireOp",EDGE,"E198.1")}),1.0]])]});
            var Q35;
            Q35=makeQuery(id+"F19.imprint","IMPRINT",FACE,{"disambiguationData":[TD([[makeQuery(id+"F19.imprint","IMPRINT",EDGE,{"derivedFrom":sQuery(id+"F19.wireOp",EDGE,"E198.0")}),1.0]])]});
            var Q36;
            {var subQ5=sQuery(id+"F19.wireOp",EDGE,"E218");Q36=makeQuery(id+"F19.imprint","IMPRINT",FACE,{"disambiguationData":[TD([[makeQuery(id+"F19.imprint","IMPRINT",EDGE,{"derivedFrom":subQ5}),-1.0]])]});}
            var Q37;
            {var subQ5=sQuery(id+"F19.wireOp",EDGE,"E216");Q37=makeQuery(id+"F19.imprint","IMPRINT",FACE,{"disambiguationData":[TD([[makeQuery(id+"F19.imprint","IMPRINT",EDGE,{"derivedFrom":subQ5}),1.0]])]});}
            var Q38;
            Q38=makeQuery(id+"F19.imprint","IMPRINT",FACE,{"disambiguationData":[TD([[makeQuery(id+"F19.imprint","IMPRINT",EDGE,{"derivedFrom":sQuery(id+"F19.wireOp",EDGE,"E209.2")}),1.0]])]});
            var Q39;
            Q39=makeQuery(id+"F19.imprint","IMPRINT",FACE,{"disambiguationData":[TD([[makeQuery(id+"F19.imprint","IMPRINT",EDGE,{"derivedFrom":sQuery(id+"F19.wireOp",EDGE,"E209.1")}),1.0]])]});
            var Q40;
            Q40=makeQuery(id+"F19.imprint","IMPRINT",FACE,{"disambiguationData":[TD([[makeQuery(id+"F19.imprint","IMPRINT",EDGE,{"derivedFrom":sQuery(id+"F19.wireOp",EDGE,"E209.0")}),1.0]])]});
            var Q41;
            {var subQ0=sQuery(id+"F19.wireOp",EDGE,"E219");var subQ1=sQuery(id+"F19.wireOp",EDGE,"E197.1");var subQ2=makeQuery(id+"F19.imprint","INTERSECT",VERTEX,{"derivedFrom":[subQ1,subQ0]});Q41=makeQuery(id+"F19.imprint","IMPRINT",FACE,{"disambiguationData":[TD([[makeQuery(id+"F19.imprint","IMPRINT",EDGE,{"disambiguationData":[TD([[subQ2,-1.0]])],"derivedFrom":subQ1}),1.0]])]});}
            var Q42;
            {var subQ0=sQuery(id+"F19.wireOp",EDGE,"E209.3");var subQ1=sQuery(id+"F19.wireOp",EDGE,"E197.2");var subQ2=makeQuery(id+"F19.imprint","INTERSECT",VERTEX,{"derivedFrom":[subQ1,subQ0]});Q42=makeQuery(id+"F19.imprint","IMPRINT",FACE,{"disambiguationData":[TD([[makeQuery(id+"F19.imprint","IMPRINT",EDGE,{"disambiguationData":[TD([[subQ2,-1.0]])],"derivedFrom":subQ1}),1.0]])]});}
            var Q43;
            {var subQ0=sQuery(id+"F19.wireOp",EDGE,"E198.2");var subQ1=sQuery(id+"F19.wireOp",EDGE,"E197.1");var subQ2=makeQuery(id+"F19.imprint","INTERSECT",VERTEX,{"derivedFrom":[subQ1,subQ0]});Q43=makeQuery(id+"F19.imprint","IMPRINT",FACE,{"disambiguationData":[TD([[makeQuery(id+"F19.imprint","IMPRINT",EDGE,{"disambiguationData":[TD([[subQ2,-1.0]])],"derivedFrom":subQ1}),1.0]])]});}
            var Q44;
            {var subQ5=sQuery(id+"F19.wireOp",EDGE,"E246");Q44=makeQuery(id+"F19.imprint","IMPRINT",FACE,{"disambiguationData":[TD([[makeQuery(id+"F19.imprint","IMPRINT",EDGE,{"derivedFrom":subQ5}),-1.0]])]});}
            var Q45;
            Q45=makeQuery(id+"F19.imprint","IMPRINT",FACE,{"disambiguationData":[TD([[makeQuery(id+"F19.imprint","IMPRINT",EDGE,{"derivedFrom":sQuery(id+"F19.wireOp",EDGE,"E186.3")}),1.0]])]});
            var Q46;
            Q46=makeQuery(id+"F19.imprint","IMPRINT",FACE,{"disambiguationData":[TD([[makeQuery(id+"F19.imprint","IMPRINT",EDGE,{"derivedFrom":sQuery(id+"F19.wireOp",EDGE,"E186.4")}),1.0]])]});
            var Q47;
            Q47=makeQuery(id+"F19.imprint","IMPRINT",FACE,{"disambiguationData":[TD([[makeQuery(id+"F19.imprint","IMPRINT",EDGE,{"derivedFrom":sQuery(id+"F19.wireOp",EDGE,"E186.0")}),1.0]])]});
            var Q48;
            Q48=makeQuery(id+"F19.imprint","IMPRINT",FACE,{"disambiguationData":[TD([[makeQuery(id+"F19.imprint","IMPRINT",EDGE,{"derivedFrom":sQuery(id+"F19.wireOp",EDGE,"E186.1")}),1.0]])]});
            var Q49;
            Q49=makeQuery(id+"F19.imprint","IMPRINT",FACE,{"disambiguationData":[TD([[makeQuery(id+"F19.imprint","IMPRINT",EDGE,{"derivedFrom":sQuery(id+"F19.wireOp",EDGE,"E186.2")}),1.0]])]});
            var Q50;
            {var subQ0=sQuery(id+"F19.wireOp",EDGE,"E242.1");var subQ1=sQuery(id+"F19.wireOp",EDGE,"E197.0");var subQ2=makeQuery(id+"F19.imprint","INTERSECT",VERTEX,{"derivedFrom":[subQ1,subQ0]});Q50=makeQuery(id+"F19.imprint","IMPRINT",FACE,{"disambiguationData":[TD([[makeQuery(id+"F19.imprint","IMPRINT",EDGE,{"disambiguationData":[TD([[subQ2,-1.0]])],"derivedFrom":subQ1}),1.0]])]});}
            extrude(context, id + "F27", {"entities" : qUnion([Q0, Q1, Q2, Q3, Q4, Q5, Q6, Q7, Q8, Q9, Q10, Q11, Q12, Q13, Q14, Q15, Q16, Q17, Q18, Q19, Q20, Q21, Q22, Q23, Q24, Q25, Q26, Q27, Q28, Q29, Q30, Q31, Q32, Q33, Q34, Q35, Q36, Q37, Q38, Q39, Q40, Q41, Q42, Q43, Q44, Q45, Q46, Q47, Q48, Q49, Q50]), "operationType" : NewBodyOperationType.ADD, "depth" : 0.1 * mm});
        }
        {
            var Q0;
            Q0=makeQuery(id+"F35.opExtrude","CAP_FACE",FACE,{"disambiguationData":[OSD([sQuery(id+"F0.wireOp",EDGE,"E0")])],"isStart":false});
            var sketch = newSketch(context, id + "F28", { "sketchPlane" : qUnion([Q0])});
            skCircle(sketch, "E320", {"center": v(0, 0) * mm, "radius": 15.24 * mm});
            skCircle(sketch, "E321", {"center": v(0, 0) * mm, "radius": 12.7 * mm});
            skLineSegment(sketch, "E322", {"start": v(0, 18.54) * mm, "end": v(0, 15.24) * mm});
            skLineSegment(sketch, "E323", {"start": v(0, 15.24) * mm, "end": v(0, -15.24) * mm});
            skLineSegment(sketch, "E324", {"start": v(0, -15.24) * mm, "end": v(0, -18.54) * mm});
            skLineSegment(sketch, "E325", {"start": v(18.54, 0) * mm, "end": v(15.24, 0) * mm});
            skLineSegment(sketch, "E326", {"start": v(15.24, 0) * mm, "end": v(-15.24, 0) * mm});
            skLineSegment(sketch, "E327", {"start": v(-15.24, 0) * mm, "end": v(-18.54, 0) * mm});
            skLineSegment(sketch, "E328", {"start": v(0, 18.54) * mm, "end": v(3.78, 14.76) * mm});
            skLineSegment(sketch, "E329", {"start": v(0, 18.54) * mm, "end": v(-3.78, 14.76) * mm});
            skArc(sketch, "E330", {"start": v(0, 18.54) * mm, "mid": v(1.24, 16) * mm, "end": v(3.78, 14.76) * mm});
            skArc(sketch, "E331", {"start": v(-3.78, 14.76) * mm, "mid": v(-1.3, 16.07) * mm, "end": v(0, 18.54) * mm});
            skLineSegment(sketch, "E332", {"start": v(18.54, 0) * mm, "end": v(14.76, -3.78) * mm});
            skLineSegment(sketch, "E333", {"start": v(18.54, 0) * mm, "end": v(14.76, 3.78) * mm});
            skArc(sketch, "E334", {"start": v(18.54, 0) * mm, "mid": v(16, -1.24) * mm, "end": v(14.76, -3.78) * mm});
            skArc(sketch, "E335", {"start": v(14.76, 3.78) * mm, "mid": v(16, 1.24) * mm, "end": v(18.54, 0) * mm});
            skLineSegment(sketch, "E336", {"start": v(0, -18.54) * mm, "end": v(3.78, -14.76) * mm});
            skLineSegment(sketch, "E337", {"start": v(0, -18.54) * mm, "end": v(-3.78, -14.76) * mm});
            skArc(sketch, "E338", {"start": v(0, -18.54) * mm, "mid": v(-1.24, -16) * mm, "end": v(-3.78, -14.76) * mm});
            skArc(sketch, "E339", {"start": v(3.78, -14.76) * mm, "mid": v(1.24, -16) * mm, "end": v(0, -18.54) * mm});
            skLineSegment(sketch, "E340", {"start": v(-18.54, 0) * mm, "end": v(-14.76, 3.78) * mm});
            skLineSegment(sketch, "E341", {"start": v(-18.54, 0) * mm, "end": v(-14.76, -3.78) * mm});
            skArc(sketch, "E342", {"start": v(-18.54, 0) * mm, "mid": v(-16, 1.24) * mm, "end": v(-14.76, 3.78) * mm});
            skArc(sketch, "E343", {"start": v(-14.76, -3.78) * mm, "mid": v(-16, -1.24) * mm, "end": v(-18.54, 0) * mm});
            skSolve(sketch);
        }
        {
            var Q0;
            {var subQ0=sQuery(id+"F28.wireOp",EDGE,"E323");var subQ5=sQuery(id+"F28.wireOp",EDGE,"E321");var subQ6=makeQuery(id+"F28.imprint","INTERSECT",VERTEX,{"disambiguationData":[OD(0.0)],"derivedFrom":[subQ5,subQ0]});Q0=makeQuery(id+"F28.imprint","IMPRINT",FACE,{"disambiguationData":[TD([[makeQuery(id+"F28.imprint","IMPRINT",EDGE,{"disambiguationData":[TD([[subQ6,-1.0]])],"derivedFrom":subQ5}),-1.0]])]});}
            var Q1;
            {var subQ1=sQuery(id+"F28.wireOp",EDGE,"E320");var subQ5=sQuery(id+"F28.wireOp",EDGE,"E326");var subQ8=makeQuery(id+"F28.imprint","INTERSECT",VERTEX,{"disambiguationData":[OD(0.0)],"derivedFrom":[subQ1,subQ5]});Q1=makeQuery(id+"F28.imprint","IMPRINT",FACE,{"disambiguationData":[TD([[makeQuery(id+"F28.imprint","IMPRINT",EDGE,{"disambiguationData":[TD([[subQ8,-1.0]])],"derivedFrom":subQ1}),1.0]])]});}
            var Q2;
            {var subQ0=sQuery(id+"F28.wireOp",EDGE,"E323");var subQ1=sQuery(id+"F28.wireOp",EDGE,"E320");var subQ2=makeQuery(id+"F28.imprint","INTERSECT",VERTEX,{"derivedFrom":[subQ1,subQ0]});Q2=makeQuery(id+"F28.imprint","IMPRINT",FACE,{"disambiguationData":[TD([[makeQuery(id+"F28.imprint","IMPRINT",EDGE,{"disambiguationData":[TD([[subQ2,-1.0]])],"derivedFrom":subQ1}),1.0]])]});}
            var Q3;
            {var subQ0=sQuery(id+"F28.wireOp",EDGE,"E323");var subQ1=sQuery(id+"F28.wireOp",EDGE,"E320");var subQ2=makeQuery(id+"F28.imprint","INTERSECT",VERTEX,{"derivedFrom":[subQ1,subQ0]});Q3=makeQuery(id+"F28.imprint","IMPRINT",FACE,{"disambiguationData":[TD([[makeQuery(id+"F28.imprint","IMPRINT",EDGE,{"disambiguationData":[TD([[subQ2,1.0]])],"derivedFrom":subQ1}),1.0]])]});}
            var Q4;
            {var subQ0=sQuery(id+"F28.wireOp",EDGE,"E323");var subQ1=sQuery(id+"F28.wireOp",EDGE,"E321");var subQ2=makeQuery(id+"F28.imprint","INTERSECT",VERTEX,{"disambiguationData":[OD(0.0)],"derivedFrom":[subQ1,subQ0]});Q4=makeQuery(id+"F28.imprint","IMPRINT",FACE,{"disambiguationData":[TD([[makeQuery(id+"F28.imprint","IMPRINT",EDGE,{"disambiguationData":[TD([[subQ2,1.0]])],"derivedFrom":subQ1}),-1.0]])]});}
            var Q5;
            {var subQ0=sQuery(id+"F28.wireOp",EDGE,"E326");var subQ1=sQuery(id+"F28.wireOp",EDGE,"E321");var subQ2=makeQuery(id+"F28.imprint","INTERSECT",VERTEX,{"disambiguationData":[OD(0.0)],"derivedFrom":[subQ1,subQ0]});Q5=makeQuery(id+"F28.imprint","IMPRINT",FACE,{"disambiguationData":[TD([[makeQuery(id+"F28.imprint","IMPRINT",EDGE,{"disambiguationData":[TD([[subQ2,1.0]])],"derivedFrom":subQ1}),-1.0]])]});}
            var Q6;
            {var subQ0=sQuery(id+"F28.wireOp",EDGE,"E327");Q6=makeQuery(id+"F28.imprint","IMPRINT",FACE,{"disambiguationData":[TD([[makeQuery(id+"F28.imprint","IMPRINT",EDGE,{"derivedFrom":subQ0}),-1.0]])]});}
            var Q7;
            {var subQ0=sQuery(id+"F28.wireOp",EDGE,"E327");Q7=makeQuery(id+"F28.imprint","IMPRINT",FACE,{"disambiguationData":[TD([[makeQuery(id+"F28.imprint","IMPRINT",EDGE,{"derivedFrom":subQ0}),1.0]])]});}
            var Q8;
            {var subQ0=sQuery(id+"F28.wireOp",EDGE,"E324");Q8=makeQuery(id+"F28.imprint","IMPRINT",FACE,{"disambiguationData":[TD([[makeQuery(id+"F28.imprint","IMPRINT",EDGE,{"derivedFrom":subQ0}),-1.0]])]});}
            var Q9;
            {var subQ0=sQuery(id+"F28.wireOp",EDGE,"E324");Q9=makeQuery(id+"F28.imprint","IMPRINT",FACE,{"disambiguationData":[TD([[makeQuery(id+"F28.imprint","IMPRINT",EDGE,{"derivedFrom":subQ0}),1.0]])]});}
            var Q10;
            {var subQ0=sQuery(id+"F28.wireOp",EDGE,"E325");Q10=makeQuery(id+"F28.imprint","IMPRINT",FACE,{"disambiguationData":[TD([[makeQuery(id+"F28.imprint","IMPRINT",EDGE,{"derivedFrom":subQ0}),1.0]])]});}
            var Q11;
            {var subQ0=sQuery(id+"F28.wireOp",EDGE,"E325");Q11=makeQuery(id+"F28.imprint","IMPRINT",FACE,{"disambiguationData":[TD([[makeQuery(id+"F28.imprint","IMPRINT",EDGE,{"derivedFrom":subQ0}),-1.0]])]});}
            var Q12;
            {var subQ0=sQuery(id+"F28.wireOp",EDGE,"E322");Q12=makeQuery(id+"F28.imprint","IMPRINT",FACE,{"disambiguationData":[TD([[makeQuery(id+"F28.imprint","IMPRINT",EDGE,{"derivedFrom":subQ0}),-1.0]])]});}
            var Q13;
            {var subQ0=sQuery(id+"F28.wireOp",EDGE,"E322");Q13=makeQuery(id+"F28.imprint","IMPRINT",FACE,{"disambiguationData":[TD([[makeQuery(id+"F28.imprint","IMPRINT",EDGE,{"derivedFrom":subQ0}),1.0]])]});}
            extrude(context, id + "F29", {"entities" : qUnion([Q0, Q1, Q2, Q3, Q4, Q5, Q6, Q7, Q8, Q9, Q10, Q11, Q12, Q13]), "operationType" : NewBodyOperationType.ADD, "depth" : 0.25 * mm});
        }
        {
            var Q0;
            Q0=makeQuery(id+"F35.opExtrude","CAP_FACE",FACE,{"disambiguationData":[OSD([sQuery(id+"F0.wireOp",EDGE,"E0")])],"isStart":false});
            var sketch = newSketch(context, id + "F30", { "sketchPlane" : qUnion([Q0])});
            skLineSegment(sketch, "E344", {"start": v(1.04, -8.23) * mm, "end": v(3.18, -6.74) * mm});
            skLineSegment(sketch, "E345", {"start": v(3.44, -6.93) * mm, "end": v(3.35, -7.2) * mm});
            skLineSegment(sketch, "E346", {"start": v(3.71, -8.48) * mm, "end": v(4.75, -9.34) * mm});
            skLineSegment(sketch, "E347", {"start": v(5.4, -9.61) * mm, "end": v(6.1, -9.68) * mm});
            skLineSegment(sketch, "E348", {"start": v(6.85, -9.5) * mm, "end": v(7.3, -9.2) * mm});
            skLineSegment(sketch, "E349", {"start": v(6.04, -8.64) * mm, "end": v(5.38, -7.76) * mm});
            skLineSegment(sketch, "E350", {"start": v(5.93, -5.94) * mm, "end": v(6.68, -5.6) * mm});
            skLineSegment(sketch, "E351", {"start": v(8.26, -5.86) * mm, "end": v(8.71, -6.3) * mm});
            skLineSegment(sketch, "E352", {"start": v(8.71, -6.3) * mm, "end": v(9.2, -5.14) * mm});
            skLineSegment(sketch, "E353", {"start": v(9.2, -5.14) * mm, "end": v(9.11, -4.1) * mm});
            skLineSegment(sketch, "E354", {"start": v(9.11, -4.1) * mm, "end": v(8.79, -3.63) * mm});
            skLineSegment(sketch, "E355", {"start": v(8.46, -3.16) * mm, "end": v(8.13, -3) * mm});
            skLineSegment(sketch, "E356", {"start": v(8.13, -3) * mm, "end": v(7.47, -3.1) * mm});
            skLineSegment(sketch, "E357", {"start": v(6.81, -3.19) * mm, "end": v(5.55, -4.37) * mm});
            skLineSegment(sketch, "E358", {"start": v(5.55, -4.37) * mm, "end": v(5.45, -4.43) * mm});
            skLineSegment(sketch, "E359", {"start": v(5.34, -4.5) * mm, "end": v(4.26, -4.87) * mm});
            skLineSegment(sketch, "E360", {"start": v(4.26, -4.87) * mm, "end": v(4.16, -4.74) * mm});
            skLineSegment(sketch, "E361", {"start": v(4.06, -4.61) * mm, "end": v(8.5, 1.74) * mm});
            skLineSegment(sketch, "E362", {"start": v(8.5, 1.74) * mm, "end": v(8.74, 1.87) * mm});
            skLineSegment(sketch, "E363", {"start": v(8.99, 2) * mm, "end": v(9.38, 2) * mm});
            skLineSegment(sketch, "E364", {"start": v(9.38, 2) * mm, "end": v(9.38, 2.63) * mm});
            skLineSegment(sketch, "E365", {"start": v(9.38, 2.63) * mm, "end": v(9.35, 2.73) * mm});
            skLineSegment(sketch, "E366", {"start": v(9.31, 2.84) * mm, "end": v(9.16, 3.04) * mm});
            skLineSegment(sketch, "E367", {"start": v(9.16, 3.04) * mm, "end": v(8.9, 3.06) * mm});
            skLineSegment(sketch, "E368", {"start": v(8.65, 3.08) * mm, "end": v(6.57, 1) * mm});
            skLineSegment(sketch, "E369", {"start": v(6.57, 1) * mm, "end": v(6.12, 1.03) * mm});
            skLineSegment(sketch, "E370", {"start": v(5.68, 1.06) * mm, "end": v(5.5, 1.29) * mm});
            skLineSegment(sketch, "E371", {"start": v(5.5, 1.29) * mm, "end": v(5.44, 1.44) * mm});
            skLineSegment(sketch, "E372", {"start": v(5.39, 1.6) * mm, "end": v(5.14, 4.55) * mm});
            skLineSegment(sketch, "E373", {"start": v(5.14, 4.55) * mm, "end": v(5.72, 7.3) * mm});
            skLineSegment(sketch, "E374", {"start": v(5.72, 7.3) * mm, "end": v(6.17, 7.88) * mm});
            skLineSegment(sketch, "E375", {"start": v(6.17, 7.88) * mm, "end": v(6.26, 8.41) * mm});
            skLineSegment(sketch, "E376", {"start": v(6.36, 8.95) * mm, "end": v(6.32, 9.07) * mm});
            skLineSegment(sketch, "E377", {"start": v(6.32, 9.07) * mm, "end": v(5.87, 9.46) * mm});
            skLineSegment(sketch, "E378", {"start": v(5.42, 9.86) * mm, "end": v(4.97, 9.94) * mm});
            skLineSegment(sketch, "E379", {"start": v(4.97, 9.94) * mm, "end": v(4.39, 9.7) * mm});
            skLineSegment(sketch, "E380", {"start": v(3.8, 9.46) * mm, "end": v(3.07, 8.41) * mm});
            skLineSegment(sketch, "E381", {"start": v(3.07, 8.41) * mm, "end": v(2.96, 8.04) * mm});
            skLineSegment(sketch, "E382", {"start": v(2.85, 7.66) * mm, "end": v(3.02, 5.24) * mm});
            skLineSegment(sketch, "E383", {"start": v(3.02, 5.24) * mm, "end": v(3.34, 1.56) * mm});
            skLineSegment(sketch, "E384", {"start": v(3.34, 1.56) * mm, "end": v(3.47, 1.25) * mm});
            skLineSegment(sketch, "E385", {"start": v(3.59, 0.95) * mm, "end": v(4.4, -0.1) * mm});
            skLineSegment(sketch, "E386", {"start": v(4.4, -0.1) * mm, "end": v(4.34, -0.24) * mm});
            skLineSegment(sketch, "E387", {"start": v(4.27, -0.37) * mm, "end": v(3.94, -0.37) * mm});
            skLineSegment(sketch, "E388", {"start": v(3.94, -0.37) * mm, "end": v(3.69, -0.32) * mm});
            skLineSegment(sketch, "E389", {"start": v(3.69, -0.32) * mm, "end": v(2.54, 0.24) * mm});
            skLineSegment(sketch, "E390", {"start": v(2.54, 0.24) * mm, "end": v(2.41, 0.35) * mm});
            skLineSegment(sketch, "E391", {"start": v(2.3, 0.46) * mm, "end": v(1.2, 2.17) * mm});
            skLineSegment(sketch, "E392", {"start": v(1.2, 2.17) * mm, "end": v(1.08, 2.29) * mm});
            skLineSegment(sketch, "E393", {"start": v(1.08, 2.29) * mm, "end": v(0.87, 2.4) * mm});
            skLineSegment(sketch, "E394", {"start": v(0.87, 2.4) * mm, "end": v(0.64, 2.32) * mm});
            skLineSegment(sketch, "E395", {"start": v(0.41, 2.25) * mm, "end": v(-0.23, 0.98) * mm});
            skLineSegment(sketch, "E396", {"start": v(-0.23, 0.98) * mm, "end": v(-0.33, 0.74) * mm});
            skLineSegment(sketch, "E397", {"start": v(-0.33, 0.74) * mm, "end": v(-0.5, 0.76) * mm});
            skLineSegment(sketch, "E398", {"start": v(-0.66, 0.78) * mm, "end": v(-0.68, 0.91) * mm});
            skLineSegment(sketch, "E399", {"start": v(-0.68, 0.91) * mm, "end": v(-1.37, 1.37) * mm});
            skLineSegment(sketch, "E400", {"start": v(-2.13, 1.86) * mm, "end": v(-2.36, 1.8) * mm});
            skLineSegment(sketch, "E401", {"start": v(-2.36, 1.8) * mm, "end": v(-2.73, 2.08) * mm});
            skLineSegment(sketch, "E402", {"start": v(-3.1, 2.36) * mm, "end": v(-3.24, 7.94) * mm});
            skLineSegment(sketch, "E403", {"start": v(-3.24, 7.94) * mm, "end": v(-3.16, 8.14) * mm});
            skLineSegment(sketch, "E404", {"start": v(-3.09, 8.35) * mm, "end": v(-2.9, 8.56) * mm});
            skLineSegment(sketch, "E405", {"start": v(-2.9, 8.56) * mm, "end": v(-2.9, 8.8) * mm});
            skLineSegment(sketch, "E406", {"start": v(-2.9, 9.03) * mm, "end": v(-3.72, 9.9) * mm});
            skLineSegment(sketch, "E407", {"start": v(-3.72, 9.9) * mm, "end": v(-3.96, 9.9) * mm});
            skLineSegment(sketch, "E408", {"start": v(-4.2, 9.92) * mm, "end": v(-5.03, 9.14) * mm});
            skLineSegment(sketch, "E409", {"start": v(-5.03, 9.14) * mm, "end": v(-5.2, 8.71) * mm});
            skLineSegment(sketch, "E410", {"start": v(-5.4, 8.29) * mm, "end": v(-5.4, 2.3) * mm});
            skLineSegment(sketch, "E411", {"start": v(-5.4, 2.3) * mm, "end": v(-5.5, 1.93) * mm});
            skLineSegment(sketch, "E412", {"start": v(-5.6, 1.56) * mm, "end": v(-5.87, 1.13) * mm});
            skLineSegment(sketch, "E413", {"start": v(-5.87, 1.13) * mm, "end": v(-6.02, 1.14) * mm});
            skLineSegment(sketch, "E414", {"start": v(-6.17, 1.16) * mm, "end": v(-6.58, 1.52) * mm});
            skLineSegment(sketch, "E415", {"start": v(-6.98, 1.89) * mm, "end": v(-7.31, 1.66) * mm});
            skLineSegment(sketch, "E416", {"start": v(-7.64, 1.44) * mm, "end": v(-7.99, 0.96) * mm});
            skLineSegment(sketch, "E417", {"start": v(-7.99, 0.96) * mm, "end": v(-8.1, 0.62) * mm});
            skLineSegment(sketch, "E418", {"start": v(-8.2, 0.28) * mm, "end": v(-8.2, -1.79) * mm});
            skLineSegment(sketch, "E419", {"start": v(-8.2, -1.79) * mm, "end": v(-8.34, -2.2) * mm});
            skLineSegment(sketch, "E420", {"start": v(-8.47, -2.61) * mm, "end": v(-9.63, -4.23) * mm});
            skLineSegment(sketch, "E421", {"start": v(-9.63, -4.23) * mm, "end": v(-9.83, -4.75) * mm});
            skLineSegment(sketch, "E422", {"start": v(-9.83, -4.75) * mm, "end": v(-9.9, -5.21) * mm});
            skLineSegment(sketch, "E423", {"start": v(-9.9, -5.21) * mm, "end": v(-9.77, -5.66) * mm});
            skLineSegment(sketch, "E424", {"start": v(-9.64, -6.11) * mm, "end": v(-9.08, -6.78) * mm});
            skLineSegment(sketch, "E425", {"start": v(-9.08, -6.78) * mm, "end": v(-8.63, -7) * mm});
            skLineSegment(sketch, "E426", {"start": v(-8.18, -7.2) * mm, "end": v(-7.43, -7.2) * mm});
            skLineSegment(sketch, "E427", {"start": v(-7.43, -7.2) * mm, "end": v(-7.3, -7.14) * mm});
            skLineSegment(sketch, "E428", {"start": v(-7.16, -7.07) * mm, "end": v(-6.15, -5.65) * mm});
            skLineSegment(sketch, "E429", {"start": v(-6.15, -5.65) * mm, "end": v(-6.03, -5.63) * mm});
            skLineSegment(sketch, "E430", {"start": v(-5.91, -5.61) * mm, "end": v(-5.7, -5.76) * mm});
            skLineSegment(sketch, "E431", {"start": v(-5.7, -5.76) * mm, "end": v(-5.67, -5.83) * mm});
            skLineSegment(sketch, "E432", {"start": v(-5.64, -5.9) * mm, "end": v(-5.64, -7.3) * mm});
            skLineSegment(sketch, "E433", {"start": v(-5.64, -7.3) * mm, "end": v(-5.69, -7.58) * mm});
            skLineSegment(sketch, "E434", {"start": v(-5.74, -7.85) * mm, "end": v(-6.26, -9.1) * mm});
            skLineSegment(sketch, "E435", {"start": v(-6.26, -9.1) * mm, "end": v(-6.2, -9.31) * mm});
            skLineSegment(sketch, "E436", {"start": v(-6.13, -9.52) * mm, "end": v(-5.59, -9.86) * mm});
            skLineSegment(sketch, "E437", {"start": v(-5.59, -9.86) * mm, "end": v(-5.34, -9.94) * mm});
            skLineSegment(sketch, "E438", {"start": v(-5.1, -10.03) * mm, "end": v(-3.5, -10.2) * mm});
            skLineSegment(sketch, "E439", {"start": v(-3.5, -10.2) * mm, "end": v(-3.04, -10.04) * mm});
            skLineSegment(sketch, "E440", {"start": v(-2.58, -9.89) * mm, "end": v(-2.16, -9.5) * mm});
            skLineSegment(sketch, "E441", {"start": v(-2.16, -9.5) * mm, "end": v(-2.49, -9.36) * mm});
            skLineSegment(sketch, "E442", {"start": v(-2.49, -9.36) * mm, "end": v(-2.89, -8.93) * mm});
            skLineSegment(sketch, "E443", {"start": v(-3.28, -8.5) * mm, "end": v(-3.56, -7.68) * mm});
            skLineSegment(sketch, "E444", {"start": v(-3.56, -7.68) * mm, "end": v(-3.6, -7.36) * mm});
            skLineSegment(sketch, "E445", {"start": v(-3.63, -7.03) * mm, "end": v(-3.43, -5.56) * mm});
            skLineSegment(sketch, "E446", {"start": v(-3.43, -5.56) * mm, "end": v(-3.09, -5.04) * mm});
            skLineSegment(sketch, "E447", {"start": v(-2.75, -4.53) * mm, "end": v(-2.64, -4.47) * mm});
            skLineSegment(sketch, "E448", {"start": v(-2.64, -4.47) * mm, "end": v(-2.52, -4.5) * mm});
            skLineSegment(sketch, "E449", {"start": v(-2.4, -4.54) * mm, "end": v(-1.58, -6.23) * mm});
            skLineSegment(sketch, "E450", {"start": v(-1.58, -6.23) * mm, "end": v(-0.17, -6) * mm});
            skLineSegment(sketch, "E451", {"start": v(-0.17, -6) * mm, "end": v(1.33, -4.99) * mm});
            skLineSegment(sketch, "E452", {"start": v(1.58, -5.2) * mm, "end": v(1.03, -6.44) * mm});
            skLineSegment(sketch, "E453", {"start": v(1.03, -6.44) * mm, "end": v(0.88, -6.65) * mm});
            skLineSegment(sketch, "E454", {"start": v(0.88, -6.65) * mm, "end": v(0.22, -7.23) * mm});
            skLineSegment(sketch, "E455", {"start": v(0.18, -7.7) * mm, "end": v(0.59, -8.17) * mm});
            skLineSegment(sketch, "E456", {"start": v(8.79, -3.63) * mm, "end": v(8.46, -3.16) * mm});
            skLineSegment(sketch, "E457", {"start": v(7.47, -3.1) * mm, "end": v(6.81, -3.19) * mm});
            skLineSegment(sketch, "E458", {"start": v(5.45, -4.43) * mm, "end": v(5.34, -4.5) * mm});
            skLineSegment(sketch, "E459", {"start": v(4.16, -4.74) * mm, "end": v(4.06, -4.61) * mm});
            skLineSegment(sketch, "E460", {"start": v(8.74, 1.87) * mm, "end": v(8.99, 2) * mm});
            skLineSegment(sketch, "E461", {"start": v(9.35, 2.73) * mm, "end": v(9.31, 2.84) * mm});
            skLineSegment(sketch, "E462", {"start": v(8.9, 3.06) * mm, "end": v(8.65, 3.08) * mm});
            skLineSegment(sketch, "E463", {"start": v(6.12, 1.03) * mm, "end": v(5.68, 1.06) * mm});
            skLineSegment(sketch, "E464", {"start": v(5.44, 1.44) * mm, "end": v(5.39, 1.6) * mm});
            skLineSegment(sketch, "E465", {"start": v(6.26, 8.41) * mm, "end": v(6.36, 8.95) * mm});
            skLineSegment(sketch, "E466", {"start": v(5.87, 9.46) * mm, "end": v(5.42, 9.86) * mm});
            skLineSegment(sketch, "E467", {"start": v(4.39, 9.7) * mm, "end": v(3.8, 9.46) * mm});
            skLineSegment(sketch, "E468", {"start": v(2.96, 8.04) * mm, "end": v(2.85, 7.66) * mm});
            skLineSegment(sketch, "E469", {"start": v(3.47, 1.25) * mm, "end": v(3.59, 0.95) * mm});
            skLineSegment(sketch, "E470", {"start": v(4.34, -0.24) * mm, "end": v(4.27, -0.37) * mm});
            skLineSegment(sketch, "E471", {"start": v(2.41, 0.35) * mm, "end": v(2.3, 0.46) * mm});
            skLineSegment(sketch, "E472", {"start": v(0.64, 2.32) * mm, "end": v(0.41, 2.25) * mm});
            skLineSegment(sketch, "E473", {"start": v(-0.5, 0.76) * mm, "end": v(-0.66, 0.78) * mm});
            skLineSegment(sketch, "E474", {"start": v(-1.37, 1.37) * mm, "end": v(-2.13, 1.86) * mm});
            skLineSegment(sketch, "E475", {"start": v(-2.73, 2.08) * mm, "end": v(-3.1, 2.36) * mm});
            skLineSegment(sketch, "E476", {"start": v(-3.16, 8.14) * mm, "end": v(-3.09, 8.35) * mm});
            skLineSegment(sketch, "E477", {"start": v(-2.9, 8.8) * mm, "end": v(-2.9, 9.03) * mm});
            skLineSegment(sketch, "E478", {"start": v(-3.96, 9.9) * mm, "end": v(-4.2, 9.92) * mm});
            skLineSegment(sketch, "E479", {"start": v(-5.2, 8.71) * mm, "end": v(-5.4, 8.29) * mm});
            skLineSegment(sketch, "E480", {"start": v(-5.5, 1.93) * mm, "end": v(-5.6, 1.56) * mm});
            skLineSegment(sketch, "E481", {"start": v(-6.02, 1.14) * mm, "end": v(-6.17, 1.16) * mm});
            skLineSegment(sketch, "E482", {"start": v(-6.58, 1.52) * mm, "end": v(-6.98, 1.89) * mm});
            skLineSegment(sketch, "E483", {"start": v(-7.31, 1.66) * mm, "end": v(-7.64, 1.44) * mm});
            skLineSegment(sketch, "E484", {"start": v(-8.1, 0.62) * mm, "end": v(-8.2, 0.28) * mm});
            skLineSegment(sketch, "E485", {"start": v(-8.34, -2.2) * mm, "end": v(-8.47, -2.61) * mm});
            skLineSegment(sketch, "E486", {"start": v(-9.77, -5.66) * mm, "end": v(-9.64, -6.11) * mm});
            skLineSegment(sketch, "E487", {"start": v(-8.63, -7) * mm, "end": v(-8.18, -7.2) * mm});
            skLineSegment(sketch, "E488", {"start": v(-7.3, -7.14) * mm, "end": v(-7.16, -7.07) * mm});
            skLineSegment(sketch, "E489", {"start": v(-6.03, -5.63) * mm, "end": v(-5.91, -5.61) * mm});
            skLineSegment(sketch, "E490", {"start": v(-5.67, -5.83) * mm, "end": v(-5.64, -5.9) * mm});
            skLineSegment(sketch, "E491", {"start": v(-5.69, -7.58) * mm, "end": v(-5.74, -7.85) * mm});
            skLineSegment(sketch, "E492", {"start": v(-6.2, -9.31) * mm, "end": v(-6.13, -9.52) * mm});
            skLineSegment(sketch, "E493", {"start": v(-5.34, -9.94) * mm, "end": v(-5.1, -10.03) * mm});
            skLineSegment(sketch, "E494", {"start": v(-3.04, -10.04) * mm, "end": v(-2.58, -9.89) * mm});
            skLineSegment(sketch, "E495", {"start": v(-2.89, -8.93) * mm, "end": v(-3.28, -8.5) * mm});
            skLineSegment(sketch, "E496", {"start": v(-3.6, -7.36) * mm, "end": v(-3.63, -7.03) * mm});
            skLineSegment(sketch, "E497", {"start": v(-2.52, -4.5) * mm, "end": v(-2.4, -4.54) * mm});
            skLineSegment(sketch, "E498", {"start": v(-3.09, -5.04) * mm, "end": v(-2.75, -4.53) * mm});
            skFitSpline(sketch, "E499", {"points": [v(1.04, -8.23) * mm, v(0.8, -8.29) * mm, v(0.59, -8.17) * mm], "startDerivative": vector(-0.48, -0.2) * mm, "endDerivative": vector(-0.42, 0.31) * mm});
            skFitSpline(sketch, "E500", {"points": [v(0.18, -7.7) * mm, v(0.1, -7.46) * mm, v(0.22, -7.23) * mm], "startDerivative": vector(-0.26, 0.5) * mm, "endDerivative": vector(0.33, 0.46) * mm});
            skFitSpline(sketch, "E501", {"points": [v(0.87, -6.65) * mm, v(0.96, -6.56) * mm, v(1.03, -6.44) * mm], "startDerivative": vector(0.2, 0.17) * mm, "endDerivative": vector(0.12, 0.24) * mm});
            skFitSpline(sketch, "E502", {"points": [v(1.58, -5.2) * mm, v(1.53, -5) * mm, v(1.33, -4.99) * mm], "startDerivative": vector(-0.01, 0.5) * mm, "endDerivative": vector(-0.49, -0.07) * mm});
            skFitSpline(sketch, "E503", {"points": [v(-2.4, -4.54) * mm, v(-2.5, -4.45) * mm, v(-2.64, -4.47) * mm], "startDerivative": vector(-0.2, 0.23) * mm, "endDerivative": vector(-0.29, -0.09) * mm});
            skFitSpline(sketch, "E504", {"points": [v(-2.75, -4.53) * mm, v(-3.2, -4.97) * mm, v(-3.43, -5.56) * mm], "startDerivative": vector(-1.04, -0.8) * mm, "endDerivative": vector(-0.33, -1.26) * mm});
            skFitSpline(sketch, "E505", {"points": [v(-3.63, -7.03) * mm, v(-3.64, -7.36) * mm, v(-3.56, -7.68) * mm], "startDerivative": vector(-0.05, -0.66) * mm, "endDerivative": vector(0.18, -0.64) * mm});
            skFitSpline(sketch, "E506", {"points": [v(-3.5, -10.2) * mm, v(-3, -10.14) * mm, v(-2.58, -9.89) * mm], "startDerivative": vector(1.02, 0) * mm, "endDerivative": vector(0.82, 0.6) * mm});
            skFitSpline(sketch, "E507", {"points": [v(-5.1, -10.03) * mm, v(-5.35, -9.97) * mm, v(-5.59, -9.86) * mm], "startDerivative": vector(-0.52, 0.09) * mm, "endDerivative": vector(-0.47, 0.25) * mm});
            skFitSpline(sketch, "E508", {"points": [v(-6.13, -9.52) * mm, v(-6.27, -9.34) * mm, v(-6.26, -9.1) * mm], "startDerivative": vector(-0.36, 0.34) * mm, "endDerivative": vector(0.1, 0.49) * mm});
            skFitSpline(sketch, "E509", {"points": [v(-5.75, -7.84) * mm, v(-5.66, -7.58) * mm, v(-5.64, -7.3) * mm], "startDerivative": vector(0.2, 0.52) * mm, "endDerivative": vector(0.03, 0.56) * mm});
            skFitSpline(sketch, "E510", {"points": [v(-5.64, -5.9) * mm, v(-5.65, -5.82) * mm, v(-5.7, -5.76) * mm], "startDerivative": vector(-0.02, 0.17) * mm, "endDerivative": vector(-0.12, 0.11) * mm});
            skFitSpline(sketch, "E511", {"points": [v(-5.91, -5.61) * mm, v(-6.04, -5.58) * mm, v(-6.15, -5.65) * mm], "startDerivative": vector(-0.26, 0.1) * mm, "endDerivative": vector(-0.21, -0.19) * mm});
            skFitSpline(sketch, "E512", {"points": [v(-7.16, -7.07) * mm, v(-7.28, -7.17) * mm, v(-7.43, -7.2) * mm], "startDerivative": vector(-0.22, -0.25) * mm, "endDerivative": vector(-0.33, -0.04) * mm});
            skFitSpline(sketch, "E513", {"points": [v(-8.18, -7.2) * mm, v(-8.68, -7.1) * mm, v(-9.08, -6.78) * mm], "startDerivative": vector(-1.04, 0.12) * mm, "endDerivative": vector(-0.76, 0.73) * mm});
            skFitSpline(sketch, "E514", {"points": [v(-9.64, -6.11) * mm, v(-9.86, -5.69) * mm, v(-9.9, -5.21) * mm], "startDerivative": vector(-0.54, 0.82) * mm, "endDerivative": vector(0.02, 0.98) * mm});
            skFitSpline(sketch, "E515", {"points": [v(-9.83, -4.75) * mm, v(-9.76, -4.48) * mm, v(-9.63, -4.23) * mm], "startDerivative": vector(0.11, 0.56) * mm, "endDerivative": vector(0.3, 0.49) * mm});
            skFitSpline(sketch, "E516", {"points": [v(-8.47, -2.61) * mm, v(-8.28, -2.22) * mm, v(-8.2, -1.79) * mm], "startDerivative": vector(0.46, 0.76) * mm, "endDerivative": vector(0.07, 0.89) * mm});
            skFitSpline(sketch, "E517", {"points": [v(-8.2, 0.28) * mm, v(-8.15, 0.64) * mm, v(-7.99, 0.96) * mm], "startDerivative": vector(0.06, 0.74) * mm, "endDerivative": vector(0.38, 0.63) * mm});
            skFitSpline(sketch, "E518", {"points": [v(-7.64, 1.44) * mm, v(-7.35, 1.72) * mm, v(-6.98, 1.89) * mm], "startDerivative": vector(0.54, 0.62) * mm, "endDerivative": vector(0.78, 0.27) * mm});
            skFitSpline(sketch, "E519", {"points": [v(-6.17, 1.16) * mm, v(-6.12, 1.1) * mm, v(-6.03, 1.05) * mm, v(-5.92, 1.07) * mm, v(-5.87, 1.13) * mm], "startDerivative": vector(0.16, -0.3) * mm, "endDerivative": vector(0.2, 0.26) * mm});
            skFitSpline(sketch, "E520", {"points": [v(-5.6, 1.56) * mm, v(-5.44, 1.92) * mm, v(-5.4, 2.3) * mm], "startDerivative": vector(0.37, 0.7) * mm, "endDerivative": vector(0.06, 0.8) * mm});
            skFitSpline(sketch, "E521", {"points": [v(-5.4, 8.29) * mm, v(-5.3, 8.75) * mm, v(-5.03, 9.14) * mm], "startDerivative": vector(0.1, 0.96) * mm, "endDerivative": vector(0.63, 0.74) * mm});
            skPoint(sketch, "E522.1.internal.snap0", {"position": v(-3.96, 10) * mm});
            skFitSpline(sketch, "E522", {"points": [v(-4.2, 9.92) * mm, v(-3.98, 10) * mm, v(-3.72, 9.9) * mm], "startDerivative": vector(0.45, 0.29) * mm, "endDerivative": vector(0.5, -0.3) * mm});
            skPoint(sketch, "E523.1.internal.snap0", {"position": v(-2.8, 8.8) * mm});
            skFitSpline(sketch, "E523", {"points": [v(-2.9, 9.03) * mm, v(-2.8, 8.8) * mm, v(-2.9, 8.56) * mm], "startDerivative": vector(0.28, -0.46) * mm, "endDerivative": vector(-0.27, -0.46) * mm});
            skFitSpline(sketch, "E524", {"points": [v(-3.09, 8.35) * mm, v(-3.2, 8.16) * mm, v(-3.24, 7.94) * mm], "startDerivative": vector(-0.28, -0.37) * mm, "endDerivative": vector(-0.04, -0.46) * mm});
            skFitSpline(sketch, "E525", {"points": [v(-3.1, 2.36) * mm, v(-3.03, 2.1) * mm, v(-2.86, 1.9) * mm, v(-2.6, 1.79) * mm, v(-2.36, 1.8) * mm], "startDerivative": vector(0.2, -1.1) * mm, "endDerivative": vector(0.97, 0.16) * mm});
            skFitSpline(sketch, "E526", {"points": [v(-2.13, 1.86) * mm, v(-1.32, 1.78) * mm, v(-0.83, 1.34) * mm, v(-0.68, 0.91) * mm], "startDerivative": vector(2.28, 0.08) * mm, "endDerivative": vector(0.39, -1.5) * mm});
            skFitSpline(sketch, "E527", {"points": [v(0.41, 2.25) * mm, v(0.53, 2.37) * mm, v(0.61, 2.41) * mm, v(0.78, 2.42) * mm, v(0.87, 2.4) * mm], "startDerivative": vector(0.42, 0.52) * mm, "endDerivative": vector(0.35, -0.18) * mm});
            skFitSpline(sketch, "E528", {"points": [v(1.08, 2.29) * mm, v(1.15, 2.24) * mm, v(1.2, 2.17) * mm], "startDerivative": vector(0.16, -0.1) * mm, "endDerivative": vector(0.1, -0.15) * mm});
            skFitSpline(sketch, "E529", {"points": [v(2.3, 0.46) * mm, v(2.4, 0.34) * mm, v(2.54, 0.24) * mm], "startDerivative": vector(0.19, -0.26) * mm, "endDerivative": vector(0.3, -0.17) * mm});
            skFitSpline(sketch, "E530", {"points": [v(3.69, -0.32) * mm, v(3.81, -0.36) * mm, v(3.94, -0.37) * mm], "startDerivative": vector(0.25, -0.1) * mm, "endDerivative": vector(0.27, -0.02) * mm});
            skFitSpline(sketch, "E531", {"points": [v(4.27, -0.37) * mm, v(4.35, -0.35) * mm, v(4.43, -0.26) * mm, v(4.43, -0.16) * mm, v(4.4, -0.1) * mm], "startDerivative": vector(0.35, 0.04) * mm, "endDerivative": vector(-0.16, 0.25) * mm});
            skFitSpline(sketch, "E532", {"points": [v(3.59, 0.95) * mm, v(3.42, 1.24) * mm, v(3.34, 1.56) * mm], "startDerivative": vector(-0.38, 0.56) * mm, "endDerivative": vector(-0.1, 0.67) * mm});
            skFitSpline(sketch, "E533", {"points": [v(2.85, 7.66) * mm, v(2.9, 8.06) * mm, v(3.07, 8.41) * mm], "startDerivative": vector(0.02, 0.8) * mm, "endDerivative": vector(0.4, 0.7) * mm});
            skFitSpline(sketch, "E534", {"points": [v(3.8, 9.46) * mm, v(4.1, 9.75) * mm, v(4.32, 9.87) * mm, v(4.7, 9.96) * mm, v(4.97, 9.94) * mm], "startDerivative": vector(1.1, 1.17) * mm, "endDerivative": vector(1.1, -0.16) * mm});
            skFitSpline(sketch, "E535", {"points": [v(5.42, 9.86) * mm, v(5.87, 9.67) * mm, v(5.98, 9.58) * mm, v(6.21, 9.3) * mm, v(6.32, 9.07) * mm], "startDerivative": vector(1.7, -0.67) * mm, "endDerivative": vector(0.34, -0.96) * mm});
            skFitSpline(sketch, "E536", {"points": [v(6.36, 8.95) * mm, v(6.4, 8.68) * mm, v(6.4, 8.4) * mm, v(6.31, 8.12) * mm, v(6.17, 7.88) * mm], "startDerivative": vector(0.27, -1.1) * mm, "endDerivative": vector(-0.63, -0.95) * mm});
            skFitSpline(sketch, "E537", {"points": [v(5.39, 1.6) * mm, v(5.4, 1.48) * mm, v(5.45, 1.38) * mm, v(5.5, 1.29) * mm], "startDerivative": vector(0.05, -0.34) * mm, "endDerivative": vector(0.18, -0.27) * mm});
            skFitSpline(sketch, "E538", {"points": [v(5.68, 1.06) * mm, v(5.77, 0.96) * mm, v(5.9, 0.88) * mm, v(6.04, 0.83) * mm, v(6.18, 0.82) * mm, v(6.32, 0.85) * mm, v(6.45, 0.9) * mm, v(6.57, 1) * mm], "startDerivative": vector(0.67, -0.76) * mm, "endDerivative": vector(0.77, 0.67) * mm});
            skPoint(sketch, "E539.3.internal.snap0", {"position": v(8.91, 3.17) * mm});
            skFitSpline(sketch, "E539", {"points": [v(8.65, 3.08) * mm, v(8.7, 3.12) * mm, v(8.79, 3.16) * mm, v(8.87, 3.17) * mm, v(8.96, 3.17) * mm, v(9.03, 3.14) * mm, v(9.1, 3.1) * mm, v(9.16, 3.04) * mm], "startDerivative": vector(0.41, 0.37) * mm, "endDerivative": vector(0.39, -0.44) * mm});
            skFitSpline(sketch, "E540", {"points": [v(9.31, 2.84) * mm, v(9.35, 2.78) * mm, v(9.38, 2.7) * mm, v(9.38, 2.63) * mm], "startDerivative": vector(0.12, -0.18) * mm, "endDerivative": vector(0.02, -0.23) * mm});
            skFitSpline(sketch, "E541", {"points": [v(8.99, 2) * mm, v(8.85, 1.98) * mm, v(8.71, 1.93) * mm, v(8.6, 1.85) * mm, v(8.5, 1.74) * mm], "startDerivative": vector(-0.57, -0.04) * mm, "endDerivative": vector(-0.36, -0.45) * mm});
            skFitSpline(sketch, "E542", {"points": [v(4.06, -4.61) * mm, v(4.04, -4.65) * mm, v(4.03, -4.7) * mm, v(4.03, -4.74) * mm, v(4.05, -4.78) * mm, v(4.07, -4.82) * mm, v(4.1, -4.85) * mm, v(4.13, -4.87) * mm, v(4.17, -4.88) * mm, v(4.22, -4.88) * mm, v(4.26, -4.87) * mm], "startDerivative": vector(-0.22, -0.36) * mm, "endDerivative": vector(0.4, 0.11) * mm});
            skFitSpline(sketch, "E543", {"points": [v(5.34, -4.5) * mm, v(5.45, -4.44) * mm, v(5.55, -4.37) * mm], "startDerivative": vector(0.23, 0.1) * mm, "endDerivative": vector(0.19, 0.16) * mm});
            skFitSpline(sketch, "E544", {"points": [v(6.81, -3.19) * mm, v(7.04, -3.02) * mm, v(7.3, -2.92) * mm, v(7.58, -2.87) * mm, v(7.86, -2.9) * mm, v(8.13, -3) * mm], "startDerivative": vector(1.1, 0.89) * mm, "endDerivative": vector(1.31, -0.53) * mm});
            skFitSpline(sketch, "E545", {"points": [v(8.46, -3.16) * mm, v(8.71, -3.32) * mm, v(8.91, -3.54) * mm, v(9.05, -3.81) * mm, v(9.11, -4.1) * mm], "startDerivative": vector(1.03, -0.61) * mm, "endDerivative": vector(0.2, -1.18) * mm});
            skFitSpline(sketch, "E546", {"points": [v(8.26, -5.86) * mm, v(7.51, -5.49) * mm, v(6.68, -5.6) * mm], "startDerivative": vector(-1.46, 1) * mm, "endDerivative": vector(-1.7, -0.46) * mm});
            skFitSpline(sketch, "E547", {"points": [v(5.93, -5.94) * mm, v(5.63, -6.12) * mm, v(5.37, -6.4) * mm, v(5.2, -6.72) * mm, v(5.1, -7.07) * mm], "startDerivative": vector(-1.24, -0.67) * mm, "endDerivative": vector(-0.27, -1.42) * mm});
            skFitSpline(sketch, "E548", {"points": [v(5.1, -7.07) * mm, v(5.2, -7.43) * mm, v(5.38, -7.76) * mm], "startDerivative": vector(0.14, -0.74) * mm, "endDerivative": vector(0.41, -0.63) * mm});
            skFitSpline(sketch, "E549", {"points": [v(6.1, -9.68) * mm, v(6.38, -9.67) * mm, v(6.62, -9.61) * mm, v(6.85, -9.5) * mm], "startDerivative": vector(0.8, -0.01) * mm, "endDerivative": vector(0.69, 0.38) * mm});
            skFitSpline(sketch, "E550", {"points": [v(6.04, -8.64) * mm, v(6.25, -8.87) * mm, v(6.54, -9.06) * mm, v(6.84, -9.17) * mm, v(7.3, -9.2) * mm], "startDerivative": vector(0.87, -1.03) * mm, "endDerivative": vector(1.7, -0.07) * mm});
            skFitSpline(sketch, "E551", {"points": [v(5.4, -9.61) * mm, v(5.17, -9.57) * mm, v(4.94, -9.47) * mm, v(4.75, -9.34) * mm], "startDerivative": vector(-0.68, 0.1) * mm, "endDerivative": vector(-0.55, 0.4) * mm});
            skFitSpline(sketch, "E552", {"points": [v(3.71, -8.48) * mm, v(3.38, -8.03) * mm, v(3.3, -7.48) * mm, v(3.35, -7.2) * mm], "startDerivative": vector(-1.03, 1.1) * mm, "endDerivative": vector(0.27, 0.92) * mm});
            skFitSpline(sketch, "E553", {"points": [v(3.44, -6.93) * mm, v(3.44, -6.8) * mm, v(3.38, -6.74) * mm, v(3.26, -6.7) * mm, v(3.18, -6.74) * mm], "startDerivative": vector(0.03, 0.49) * mm, "endDerivative": vector(-0.31, -0.18) * mm});
            skFitSpline(sketch, "E554", {"points": [v(0.78, -4.05) * mm, v(1.8, -4.3) * mm, v(2.14, -4.3) * mm, v(2.41, -4.1) * mm, v(3.68, -2.52) * mm, v(3.72, -2.26) * mm, v(3.63, -2.15) * mm, v(3.51, -2.1) * mm, v(1.67, -1.9) * mm, v(1.24, -1.77) * mm, v(0.9, -1.49) * mm, v(-0.31, -0.03) * mm, v(-0.45, 0.03) * mm, v(-0.51, 0.01) * mm, v(-0.6, -0.06) * mm, v(-0.62, -0.16) * mm, v(-0.29, -2.84) * mm, v(-0.05, -3.47) * mm, v(0.45, -3.92) * mm, v(0.78, -4.05) * mm]});
            skPoint(sketch, "E555.4.internal.snap0", {"position": v(-1.61, -3.52) * mm});
            skFitSpline(sketch, "E555", {"points": [v(-1.8, -3.59) * mm, v(-1.61, -3.52) * mm, v(-1.53, -3.34) * mm, v(-1.53, -2.17) * mm, v(-1.61, -1.98) * mm, v(-1.76, -1.91) * mm, v(-1.8, -1.94) * mm, v(-2.63, -2.34) * mm, v(-2.74, -2.44) * mm, v(-2.77, -2.6) * mm, v(-2.7, -3.32) * mm, v(-2.66, -3.44) * mm, v(-2.62, -3.48) * mm, v(-2.52, -3.54) * mm, v(-2.46, -3.55) * mm, v(-1.8, -3.59) * mm]});
            skFitSpline(sketch, "E556", {"points": [v(-0.33, 0.74) * mm, v(-0.38, 0.68) * mm, v(-0.5, 0.64) * mm, v(-0.62, 0.7) * mm, v(-0.66, 0.78) * mm], "startDerivative": vector(-0.18, -0.33) * mm, "endDerivative": vector(-0.1, 0.36) * mm});
            skPoint(sketch, "E557.11.internal.snap0", {"position": v(-3.03, -0.22) * mm});
            skFitSpline(sketch, "E557", {"points": [v(-2.6, -0.91) * mm, v(-1.77, -0.5) * mm, v(-1.65, -0.4) * mm, v(-1.63, -0.24) * mm, v(-1.76, 0.62) * mm, v(-1.87, 0.8) * mm, v(-2.08, 0.82) * mm, v(-2.4, 0.7) * mm, v(-2.64, 0.52) * mm, v(-3, 0.05) * mm, v(-3, 0.03) * mm, v(-3.03, -0.24) * mm, v(-3, -0.5) * mm, v(-2.97, -0.73) * mm, v(-2.92, -0.83) * mm, v(-2.83, -0.91) * mm, v(-2.72, -0.94) * mm, v(-2.6, -0.91) * mm]});
            skFitSpline(sketch, "E558", {"points": [v(-5.8, -0.04) * mm, v(-5.9, 0) * mm, v(-6.02, 0) * mm, v(-6.26, -0.14) * mm, v(-6.41, -0.37) * mm, v(-6.57, -0.8) * mm, v(-6.6, -0.94) * mm, v(-6.6, -1.1) * mm, v(-6.5, -1.27) * mm, v(-6.31, -1.31) * mm, v(-5.91, -1.26) * mm, v(-5.76, -1.17) * mm, v(-5.7, -1) * mm, v(-5.7, -0.25) * mm, v(-5.73, -0.13) * mm, v(-5.8, -0.04) * mm]});
            skFitSpline(sketch, "E559", {"points": [v(-5.8, -5.2) * mm, v(-5.73, -5.02) * mm, v(-5.73, -3.54) * mm, v(-5.73, -3.48) * mm, v(-5.75, -3.42) * mm, v(-5.93, -3.1) * mm, v(-5.95, -3.1) * mm, v(-6.23, -3.15) * mm, v(-6.5, -3.28) * mm, v(-6.61, -3.4) * mm, v(-6.72, -3.68) * mm, v(-6.71, -3.83) * mm, v(-6.54, -4.78) * mm, v(-6.44, -5.02) * mm, v(-6.35, -5.12) * mm, v(-6.25, -5.2) * mm, v(-6, -5.27) * mm, v(-5.8, -5.2) * mm]});
            skSolve(sketch);
        }
        {
            var Q0;
            Q0=makeQuery(id+"F30.imprint","IMPRINT",FACE,{"disambiguationData":[TD([[makeQuery(id+"F30.imprint","IMPRINT",EDGE,{"derivedFrom":sQuery(id+"F30.wireOp",EDGE,"E399")}),-1.0]])]});
            var Q1;
            Q1=makeQuery(id+"F30.imprint","IMPRINT",FACE,{"disambiguationData":[TD([[makeQuery(id+"F30.imprint","IMPRINT",EDGE,{"derivedFrom":sQuery(id+"F30.wireOp",EDGE,"E394")}),-1.0]])]});
            var Q2;
            Q2=makeQuery(id+"F30.imprint","IMPRINT",FACE,{"disambiguationData":[TD([[makeQuery(id+"F30.imprint","IMPRINT",EDGE,{"derivedFrom":sQuery(id+"F30.wireOp",EDGE,"E405")}),-1.0]])]});
            var Q3;
            Q3=makeQuery(id+"F30.imprint","IMPRINT",FACE,{"disambiguationData":[TD([[makeQuery(id+"F30.imprint","IMPRINT",EDGE,{"derivedFrom":sQuery(id+"F30.wireOp",EDGE,"E407")}),-1.0]])]});
            var Q4;
            Q4=makeQuery(id+"F30.imprint","IMPRINT",FACE,{"disambiguationData":[TD([[makeQuery(id+"F30.imprint","IMPRINT",EDGE,{"derivedFrom":sQuery(id+"F30.wireOp",EDGE,"E409")}),-1.0]])]});
            var Q5;
            Q5=makeQuery(id+"F30.imprint","IMPRINT",FACE,{"disambiguationData":[TD([[makeQuery(id+"F30.imprint","IMPRINT",EDGE,{"derivedFrom":sQuery(id+"F30.wireOp",EDGE,"E415")}),-1.0]])]});
            var Q6;
            Q6=makeQuery(id+"F30.imprint","IMPRINT",FACE,{"disambiguationData":[TD([[makeQuery(id+"F30.imprint","IMPRINT",EDGE,{"derivedFrom":sQuery(id+"F30.wireOp",EDGE,"E417")}),-1.0]])]});
            var Q7;
            Q7=makeQuery(id+"F30.imprint","IMPRINT",FACE,{"disambiguationData":[TD([[makeQuery(id+"F30.imprint","IMPRINT",EDGE,{"derivedFrom":sQuery(id+"F30.wireOp",EDGE,"E423")}),-1.0]])]});
            var Q8;
            Q8=makeQuery(id+"F30.imprint","IMPRINT",FACE,{"disambiguationData":[TD([[makeQuery(id+"F30.imprint","IMPRINT",EDGE,{"derivedFrom":sQuery(id+"F30.wireOp",EDGE,"E425")}),-1.0]])]});
            var Q9;
            Q9=makeQuery(id+"F30.imprint","IMPRINT",FACE,{"disambiguationData":[TD([[makeQuery(id+"F30.imprint","IMPRINT",EDGE,{"derivedFrom":sQuery(id+"F30.wireOp",EDGE,"E427")}),-1.0]])]});
            var Q10;
            Q10=makeQuery(id+"F30.imprint","IMPRINT",FACE,{"disambiguationData":[TD([[makeQuery(id+"F30.imprint","IMPRINT",EDGE,{"derivedFrom":sQuery(id+"F30.wireOp",EDGE,"E435")}),-1.0]])]});
            var Q11;
            Q11=makeQuery(id+"F30.imprint","IMPRINT",FACE,{"disambiguationData":[TD([[makeQuery(id+"F30.imprint","IMPRINT",EDGE,{"derivedFrom":sQuery(id+"F30.wireOp",EDGE,"E439")}),-1.0]])]});
            var Q12;
            Q12=makeQuery(id+"F30.imprint","IMPRINT",FACE,{"disambiguationData":[TD([[makeQuery(id+"F30.imprint","IMPRINT",EDGE,{"derivedFrom":sQuery(id+"F30.wireOp",EDGE,"E354")}),-1.0]])]});
            var Q13;
            Q13=makeQuery(id+"F30.imprint","IMPRINT",FACE,{"disambiguationData":[TD([[makeQuery(id+"F30.imprint","IMPRINT",EDGE,{"derivedFrom":sQuery(id+"F30.wireOp",EDGE,"E356")}),-1.0]])]});
            var Q14;
            Q14=makeQuery(id+"F30.imprint","IMPRINT",FACE,{"disambiguationData":[TD([[makeQuery(id+"F30.imprint","IMPRINT",EDGE,{"derivedFrom":sQuery(id+"F30.wireOp",EDGE,"E367")}),-1.0]])]});
            var Q15;
            Q15=makeQuery(id+"F30.imprint","IMPRINT",FACE,{"disambiguationData":[TD([[makeQuery(id+"F30.imprint","IMPRINT",EDGE,{"derivedFrom":sQuery(id+"F30.wireOp",EDGE,"E375")}),-1.0]])]});
            var Q16;
            Q16=makeQuery(id+"F30.imprint","IMPRINT",FACE,{"disambiguationData":[TD([[makeQuery(id+"F30.imprint","IMPRINT",EDGE,{"derivedFrom":sQuery(id+"F30.wireOp",EDGE,"E377")}),-1.0]])]});
            var Q17;
            Q17=makeQuery(id+"F30.imprint","IMPRINT",FACE,{"disambiguationData":[TD([[makeQuery(id+"F30.imprint","IMPRINT",EDGE,{"derivedFrom":sQuery(id+"F30.wireOp",EDGE,"E379")}),-1.0]])]});
            var Q18;
            Q18=makeQuery(id+"F30.imprint","IMPRINT",FACE,{"disambiguationData":[TD([[makeQuery(id+"F30.imprint","IMPRINT",EDGE,{"derivedFrom":sQuery(id+"F30.wireOp",EDGE,"E381")}),-1.0]])]});
            var Q19;
            Q19=makeQuery(id+"F30.imprint","IMPRINT",FACE,{"disambiguationData":[TD([[makeQuery(id+"F30.imprint","IMPRINT",EDGE,{"derivedFrom":sQuery(id+"F30.wireOp",EDGE,"E365")}),-1.0]])]});
            var Q20;
            Q20=makeQuery(id+"F30.imprint","IMPRINT",FACE,{"disambiguationData":[TD([[makeQuery(id+"F30.imprint","IMPRINT",EDGE,{"derivedFrom":sQuery(id+"F30.wireOp",EDGE,"E421")}),-1.0]])]});
            var Q21;
            Q21=makeQuery(id+"F30.imprint","IMPRINT",FACE,{"disambiguationData":[TD([[makeQuery(id+"F30.imprint","IMPRINT",EDGE,{"derivedFrom":sQuery(id+"F30.wireOp",EDGE,"E344")}),1.0]])]});
            extrude(context, id + "F31", {"entities" : qUnion([Q0, Q1, Q2, Q3, Q4, Q5, Q6, Q7, Q8, Q9, Q10, Q11, Q12, Q13, Q14, Q15, Q16, Q17, Q18, Q19, Q20, Q21]), "operationType" : NewBodyOperationType.ADD, "depth" : 0.25 * mm});
        }
        {
            var Q0;
            Q0=makeQuery(id+"F29.boolean.opBoolean","SPLIT",FACE,{"disambiguationData":[TD([makeQuery(id+"F29.opExtrude","SWEPT_FACE",FACE,{"disambiguationData":[OSD([sQuery(id+"F28.wireOp",EDGE,"E321")])]})])],"derivedFrom":makeQuery(id+"F35.opExtrude","CAP_FACE",FACE,{"disambiguationData":[OSD([sQuery(id+"F0.wireOp",EDGE,"E0")])],"isStart":false})});
            var sketch = newSketch(context, id + "F32", { "sketchPlane" : qUnion([Q0])});
            skLineSegment(sketch, "E560", {"start": v(11.88, -8.36) * mm, "end": v(12.62, -6.61) * mm});
            skLineSegment(sketch, "E561", {"start": v(12.62, -6.61) * mm, "end": v(12.41, -4.31) * mm});
            skLineSegment(sketch, "E562", {"start": v(12.41, -4.31) * mm, "end": v(10.11, -3.19) * mm});
            skLineSegment(sketch, "E563", {"start": v(10.11, -3.19) * mm, "end": v(7.57, -5.57) * mm});
            skLineSegment(sketch, "E564", {"start": v(7.57, -5.57) * mm, "end": v(5.9, -6.15) * mm});
            skLineSegment(sketch, "E565", {"start": v(5.9, -6.15) * mm, "end": v(11.86, 2.4) * mm});
            skLineSegment(sketch, "E566", {"start": v(11.86, 2.4) * mm, "end": v(12.84, 2.4) * mm});
            skLineSegment(sketch, "E567", {"start": v(12.84, 2.4) * mm, "end": v(12.84, 3.58) * mm});
            skLineSegment(sketch, "E568", {"start": v(12.84, 3.58) * mm, "end": v(12.1, 4.54) * mm});
            skLineSegment(sketch, "E569", {"start": v(12.1, 4.54) * mm, "end": v(8.47, 0.9) * mm});
            skLineSegment(sketch, "E570", {"start": v(8.47, 0.9) * mm, "end": v(7.73, 1.89) * mm});
            skLineSegment(sketch, "E571", {"start": v(7.73, 1.89) * mm, "end": v(7.4, 5.82) * mm});
            skLineSegment(sketch, "E572", {"start": v(7.4, 5.82) * mm, "end": v(8.14, 9.3) * mm});
            skLineSegment(sketch, "E573", {"start": v(8.14, 9.3) * mm, "end": v(9.23, 10.7) * mm});
            skLineSegment(sketch, "E574", {"start": v(9.23, 10.7) * mm, "end": v(8.6, 12.61) * mm});
            skLineSegment(sketch, "E575", {"start": v(8.6, 12.61) * mm, "end": v(6, 13.1) * mm});
            skLineSegment(sketch, "E576", {"start": v(6, 13.1) * mm, "end": v(4.1, 10.4) * mm});
            skLineSegment(sketch, "E577", {"start": v(4.1, 10.4) * mm, "end": v(4.36, 6.7) * mm});
            skLineSegment(sketch, "E578", {"start": v(4.36, 6.7) * mm, "end": v(4.82, 1.5) * mm});
            skLineSegment(sketch, "E579", {"start": v(4.82, 1.5) * mm, "end": v(6.24, -0.32) * mm});
            skLineSegment(sketch, "E580", {"start": v(6.24, -0.32) * mm, "end": v(5.57, -0.32) * mm});
            skLineSegment(sketch, "E581", {"start": v(5.57, -0.32) * mm, "end": v(3.82, 0.53) * mm});
            skLineSegment(sketch, "E582", {"start": v(3.82, 0.53) * mm, "end": v(2.25, 3) * mm});
            skLineSegment(sketch, "E583", {"start": v(2.25, 3) * mm, "end": v(1.3, 3.49) * mm});
            skLineSegment(sketch, "E584", {"start": v(1.3, 3.49) * mm, "end": v(0.2, 1.33) * mm});
            skLineSegment(sketch, "E585", {"start": v(0.2, 1.33) * mm, "end": v(0, 0.83) * mm});
            skLineSegment(sketch, "E586", {"start": v(0, 0.83) * mm, "end": v(-0.36, 3.13) * mm});
            skLineSegment(sketch, "E587", {"start": v(-0.36, 3.13) * mm, "end": v(-2.03, 2.57) * mm});
            skLineSegment(sketch, "E588", {"start": v(-2.03, 2.57) * mm, "end": v(-3.14, 2.27) * mm});
            skLineSegment(sketch, "E589", {"start": v(-3.14, 2.27) * mm, "end": v(-3.35, 10.42) * mm});
            skLineSegment(sketch, "E590", {"start": v(-3.35, 10.42) * mm, "end": v(-2.56, 11.28) * mm});
            skLineSegment(sketch, "E591", {"start": v(-2.56, 11.28) * mm, "end": v(-4.42, 13.24) * mm});
            skLineSegment(sketch, "E592", {"start": v(-4.42, 13.24) * mm, "end": v(-6.42, 11.34) * mm});
            skLineSegment(sketch, "E593", {"start": v(-6.42, 11.34) * mm, "end": v(-6.42, 2.48) * mm});
            skLineSegment(sketch, "E594", {"start": v(-6.42, 2.48) * mm, "end": v(-7.07, 1.44) * mm});
            skLineSegment(sketch, "E595", {"start": v(-7.07, 1.44) * mm, "end": v(-7.53, 2.63) * mm});
            skLineSegment(sketch, "E596", {"start": v(-7.53, 2.63) * mm, "end": v(-8.78, 2.63) * mm});
            skLineSegment(sketch, "E597", {"start": v(-8.78, 2.63) * mm, "end": v(-10.04, 0.9) * mm});
            skLineSegment(sketch, "E598", {"start": v(-10.04, 0.9) * mm, "end": v(-10.04, -2.82) * mm});
            skLineSegment(sketch, "E599", {"start": v(-10.04, -2.82) * mm, "end": v(-12.06, -5.67) * mm});
            skLineSegment(sketch, "E600", {"start": v(-12.06, -5.67) * mm, "end": v(-12.3, -7.38) * mm});
            skLineSegment(sketch, "E601", {"start": v(-12.3, -7.38) * mm, "end": v(-10.62, -9.4) * mm});
            skLineSegment(sketch, "E602", {"start": v(-10.62, -9.4) * mm, "end": v(-8.57, -9.4) * mm});
            skLineSegment(sketch, "E603", {"start": v(-8.57, -9.4) * mm, "end": v(-7.07, -7.3) * mm});
            skLineSegment(sketch, "E604", {"start": v(-7.07, -7.3) * mm, "end": v(-6.74, -7.53) * mm});
            skLineSegment(sketch, "E605", {"start": v(-6.74, -7.53) * mm, "end": v(-6.74, -9.7) * mm});
            skLineSegment(sketch, "E606", {"start": v(-6.74, -9.7) * mm, "end": v(-7.72, -12.08) * mm});
            skLineSegment(sketch, "E607", {"start": v(-7.72, -12.08) * mm, "end": v(-6.27, -12.98) * mm});
            skLineSegment(sketch, "E608", {"start": v(-6.27, -12.98) * mm, "end": v(-3.1, -13.31) * mm});
            skLineSegment(sketch, "E609", {"start": v(-3.1, -13.31) * mm, "end": v(-1.82, -12.12) * mm});
            skLineSegment(sketch, "E610", {"start": v(-1.82, -12.12) * mm, "end": v(-3.16, -11.56) * mm});
            skLineSegment(sketch, "E611", {"start": v(-3.16, -11.56) * mm, "end": v(-3.9, -9.43) * mm});
            skLineSegment(sketch, "E612", {"start": v(-3.9, -9.43) * mm, "end": v(-3.48, -6.36) * mm});
            skLineSegment(sketch, "E613", {"start": v(-3.48, -6.36) * mm, "end": v(-2.6, -5.83) * mm});
            skLineSegment(sketch, "E614", {"start": v(-2.6, -5.83) * mm, "end": v(-1.47, -8.17) * mm});
            skLineSegment(sketch, "E615", {"start": v(-1.47, -8.17) * mm, "end": v(0.5, -7.84) * mm});
            skLineSegment(sketch, "E616", {"start": v(0.5, -7.84) * mm, "end": v(2.6, -6.42) * mm});
            skLineSegment(sketch, "E617", {"start": v(2.6, -6.42) * mm, "end": v(1.77, -8.32) * mm});
            skLineSegment(sketch, "E618", {"start": v(1.77, -8.32) * mm, "end": v(0.37, -9.53) * mm});
            skLineSegment(sketch, "E619", {"start": v(0.37, -9.53) * mm, "end": v(1.63, -11) * mm});
            skLineSegment(sketch, "E620", {"start": v(1.63, -11) * mm, "end": v(4.97, -8.67) * mm});
            skLineSegment(sketch, "E621", {"start": v(4.97, -8.67) * mm, "end": v(4.43, -10.27) * mm});
            skLineSegment(sketch, "E622", {"start": v(4.43, -10.27) * mm, "end": v(4.43, -10.27) * mm});
            skLineSegment(sketch, "E623", {"start": v(4.43, -10.27) * mm, "end": v(7.03, -12.43) * mm});
            skLineSegment(sketch, "E624", {"start": v(7.03, -12.43) * mm, "end": v(9.04, -12.62) * mm});
            skLineSegment(sketch, "E625", {"start": v(9.04, -12.62) * mm, "end": v(10.56, -11.64) * mm});
            skLineSegment(sketch, "E626", {"start": v(10.56, -11.64) * mm, "end": v(9.02, -11.64) * mm});
            skLineSegment(sketch, "E627", {"start": v(9.02, -11.64) * mm, "end": v(7.35, -9.4) * mm});
            skLineSegment(sketch, "E628", {"start": v(7.35, -9.4) * mm, "end": v(7.35, -8.2) * mm});
            skLineSegment(sketch, "E629", {"start": v(7.35, -8.2) * mm, "end": v(10.31, -6.85) * mm});
            skLineSegment(sketch, "E630", {"start": v(10.31, -6.85) * mm, "end": v(10.31, -6.85) * mm});
            skLineSegment(sketch, "E631", {"start": v(10.31, -6.85) * mm, "end": v(11.88, -8.36) * mm});
            skLineSegment(sketch, "E632", {"start": v(2.6, -6.42) * mm, "end": v(8.47, 0.9) * mm});
            skLineSegment(sketch, "E633", {"start": v(5.43, -2.9) * mm, "end": v(2.1, -2.52) * mm});
            skLineSegment(sketch, "E634", {"start": v(2.1, -2.52) * mm, "end": v(0, 0) * mm});
            skLineSegment(sketch, "E635", {"start": v(0, 0) * mm, "end": v(0.58, -4.75) * mm});
            skLineSegment(sketch, "E636", {"start": v(0.58, -4.75) * mm, "end": v(3.38, -5.45) * mm});
            skLineSegment(sketch, "E637", {"start": v(-2.03, 2.57) * mm, "end": v(-1.48, -1.11) * mm});
            skLineSegment(sketch, "E638", {"start": v(-1.48, -1.11) * mm, "end": v(-1.48, -4.45) * mm});
            skLineSegment(sketch, "E639", {"start": v(-1.48, -4.45) * mm, "end": v(-2.6, -5.83) * mm});
            skLineSegment(sketch, "E640", {"start": v(-7.07, -7.3) * mm, "end": v(-7.49, -6.6) * mm});
            skLineSegment(sketch, "E641", {"start": v(-7.49, -6.6) * mm, "end": v(-7.96, -3.96) * mm});
            skLineSegment(sketch, "E642", {"start": v(-7.96, -3.96) * mm, "end": v(-8.36, -1.2) * mm});
            skLineSegment(sketch, "E643", {"start": v(-8.36, -1.2) * mm, "end": v(-7.52, 0.63) * mm});
            skLineSegment(sketch, "E644", {"start": v(-7.52, 0.63) * mm, "end": v(-7.07, 1.44) * mm});
            skLineSegment(sketch, "E645", {"start": v(-6.81, -0.14) * mm, "end": v(-6.81, -1.43) * mm});
            skLineSegment(sketch, "E646", {"start": v(-6.81, -1.43) * mm, "end": v(-7.63, -1.55) * mm});
            skLineSegment(sketch, "E647", {"start": v(-7.63, -1.55) * mm, "end": v(-7.67, -1.22) * mm});
            skLineSegment(sketch, "E648", {"start": v(-7.67, -1.22) * mm, "end": v(-7.27, -0.14) * mm});
            skLineSegment(sketch, "E649", {"start": v(-7.27, -0.14) * mm, "end": v(-6.81, -0.14) * mm});
            skLineSegment(sketch, "E650", {"start": v(-6.85, -6.6) * mm, "end": v(-6.85, -4.5) * mm});
            skLineSegment(sketch, "E651", {"start": v(-6.85, -4.5) * mm, "end": v(-7.04, -4.14) * mm});
            skLineSegment(sketch, "E652", {"start": v(-7.04, -4.14) * mm, "end": v(-7.9, -4.3) * mm});
            skLineSegment(sketch, "E653", {"start": v(-6.85, -6.6) * mm, "end": v(-7.49, -6.6) * mm});
            skLineSegment(sketch, "E654", {"start": v(-1.8, 0.96) * mm, "end": v(-2.83, 0.63) * mm});
            skLineSegment(sketch, "E655", {"start": v(-2.83, 0.63) * mm, "end": v(-3.12, -0.2) * mm});
            skLineSegment(sketch, "E656", {"start": v(-3.12, -0.2) * mm, "end": v(-2.95, -1.12) * mm});
            skLineSegment(sketch, "E657", {"start": v(-2.95, -1.12) * mm, "end": v(-1.58, -0.45) * mm});
            skLineSegment(sketch, "E658", {"start": v(-2.75, -3.2) * mm, "end": v(-1.58, -2.62) * mm});
            skLineSegment(sketch, "E659", {"start": v(-1.58, -2.62) * mm, "end": v(-1.48, -2.62) * mm});
            skLineSegment(sketch, "E660", {"start": v(-2.75, -3.2) * mm, "end": v(-2.63, -4.38) * mm});
            skLineSegment(sketch, "E661", {"start": v(-2.63, -4.38) * mm, "end": v(-1.48, -4.45) * mm});
            skSolve(sketch);
        }
        {
            var Q0;
            Q0=makeQuery(id+"F35.opExtrude","CAP_FACE",FACE,{"disambiguationData":[OSD([sQuery(id+"F0.wireOp",EDGE,"E0")])],"isStart":true});
            var Q1;
            Q1=makeQuery(id+"F35.opExtrude","CAP_EDGE",EDGE,{"disambiguationData":[OSD([sQuery(id+"F0.wireOp",EDGE,"E0")])],"isStart":false});
            var Q2;
            Q2=makeQuery(id+"F8.opExtrude","CAP_FACE",FACE,{"disambiguationData":[OSD([sQuery(id+"F7.wireOp",EDGE,"E6"),sQuery(id+"F7.wireOp",EDGE,"E7")])],"isStart":false});
            var Q3;
            Q3=makeQuery(id+"F8.opExtrude","CAP_FACE",FACE,{"disambiguationData":[OSD([sQuery(id+"F7.wireOp",EDGE,"E6"),sQuery(id+"F7.wireOp",EDGE,"E7")])],"isStart":true});
            var Q4;
            Q4=makeQuery(id+"F29.opExtrude","CAP_FACE",FACE,{"disambiguationData":[OSD([sQuery(id+"F28.wireOp",EDGE,"E320"),sQuery(id+"F28.wireOp",EDGE,"E321"),sQuery(id+"F28.wireOp",EDGE,"E330"),sQuery(id+"F28.wireOp",EDGE,"E331"),sQuery(id+"F28.wireOp",EDGE,"E334"),sQuery(id+"F28.wireOp",EDGE,"E335"),sQuery(id+"F28.wireOp",EDGE,"E338"),sQuery(id+"F28.wireOp",EDGE,"E339"),sQuery(id+"F28.wireOp",EDGE,"E342"),sQuery(id+"F28.wireOp",EDGE,"E343")])],"isStart":false});
            chamfer(context, id + "F33", {"entities" : qUnion([Q0, Q1, Q2, Q3, Q4]), "width" : 0.13 * mm, "tangentPropagation" : true});
        }
        {
            var Q0;
            Q0=makeQuery(id+"F31.opExtrude","CAP_EDGE",EDGE,{"disambiguationData":[OSD([sQuery(id+"F30.wireOp",EDGE,"E547")])],"isStart":false});
            var Q1;
            Q1=makeQuery(id+"F31.opExtrude","CAP_EDGE",EDGE,{"disambiguationData":[OSD([sQuery(id+"F30.wireOp",EDGE,"E350")])],"isStart":false});
            var Q2;
            Q2=makeQuery(id+"F31.opExtrude","CAP_EDGE",EDGE,{"disambiguationData":[OSD([sQuery(id+"F30.wireOp",EDGE,"E546")])],"isStart":false});
            var Q3;
            Q3=makeQuery(id+"F31.opExtrude","CAP_EDGE",EDGE,{"disambiguationData":[OSD([sQuery(id+"F30.wireOp",EDGE,"E351")])],"isStart":false});
            var Q4;
            Q4=makeQuery(id+"F31.opExtrude","CAP_EDGE",EDGE,{"disambiguationData":[OSD([sQuery(id+"F30.wireOp",EDGE,"E352")])],"isStart":false});
            var Q5;
            Q5=makeQuery(id+"F31.opExtrude","CAP_EDGE",EDGE,{"disambiguationData":[OSD([sQuery(id+"F30.wireOp",EDGE,"E353")])],"isStart":false});
            var Q6;
            Q6=makeQuery(id+"F31.opExtrude","CAP_EDGE",EDGE,{"disambiguationData":[OSD([sQuery(id+"F30.wireOp",EDGE,"E545")])],"isStart":false});
            var Q7;
            Q7=makeQuery(id+"F31.opExtrude","CAP_EDGE",EDGE,{"disambiguationData":[OSD([sQuery(id+"F30.wireOp",EDGE,"E355")])],"isStart":false});
            var Q8;
            Q8=makeQuery(id+"F31.opExtrude","CAP_EDGE",EDGE,{"disambiguationData":[OSD([sQuery(id+"F30.wireOp",EDGE,"E544")])],"isStart":false});
            var Q9;
            Q9=makeQuery(id+"F31.opExtrude","CAP_EDGE",EDGE,{"disambiguationData":[OSD([sQuery(id+"F30.wireOp",EDGE,"E357")])],"isStart":false});
            var Q10;
            Q10=makeQuery(id+"F31.opExtrude","CAP_EDGE",EDGE,{"disambiguationData":[OSD([sQuery(id+"F30.wireOp",EDGE,"E359")])],"isStart":false});
            var Q11;
            Q11=makeQuery(id+"F31.opExtrude","CAP_EDGE",EDGE,{"disambiguationData":[OSD([sQuery(id+"F30.wireOp",EDGE,"E542")])],"isStart":false});
            var Q12;
            Q12=makeQuery(id+"F31.opExtrude","CAP_EDGE",EDGE,{"disambiguationData":[OSD([sQuery(id+"F30.wireOp",EDGE,"E361")])],"isStart":false});
            var Q13;
            Q13=makeQuery(id+"F31.opExtrude","CAP_EDGE",EDGE,{"disambiguationData":[OSD([sQuery(id+"F30.wireOp",EDGE,"E541")])],"isStart":false});
            var Q14;
            Q14=makeQuery(id+"F31.opExtrude","CAP_EDGE",EDGE,{"disambiguationData":[OSD([sQuery(id+"F30.wireOp",EDGE,"E363")])],"isStart":false});
            var Q15;
            Q15=makeQuery(id+"F31.opExtrude","CAP_EDGE",EDGE,{"disambiguationData":[OSD([sQuery(id+"F30.wireOp",EDGE,"E364")])],"isStart":false});
            var Q16;
            Q16=makeQuery(id+"F31.opExtrude","CAP_EDGE",EDGE,{"disambiguationData":[OSD([sQuery(id+"F30.wireOp",EDGE,"E540")])],"isStart":false});
            var Q17;
            Q17=makeQuery(id+"F31.opExtrude","CAP_EDGE",EDGE,{"disambiguationData":[OSD([sQuery(id+"F30.wireOp",EDGE,"E366")])],"isStart":false});
            var Q18;
            Q18=makeQuery(id+"F31.opExtrude","CAP_EDGE",EDGE,{"disambiguationData":[OSD([sQuery(id+"F30.wireOp",EDGE,"E539")])],"isStart":false});
            var Q19;
            Q19=makeQuery(id+"F31.opExtrude","CAP_EDGE",EDGE,{"disambiguationData":[OSD([sQuery(id+"F30.wireOp",EDGE,"E368")])],"isStart":false});
            var Q20;
            Q20=makeQuery(id+"F31.opExtrude","CAP_EDGE",EDGE,{"disambiguationData":[OSD([sQuery(id+"F30.wireOp",EDGE,"E538")])],"isStart":false});
            var Q21;
            Q21=makeQuery(id+"F31.opExtrude","CAP_EDGE",EDGE,{"disambiguationData":[OSD([sQuery(id+"F30.wireOp",EDGE,"E370")])],"isStart":false});
            var Q22;
            Q22=makeQuery(id+"F31.opExtrude","CAP_EDGE",EDGE,{"disambiguationData":[OSD([sQuery(id+"F30.wireOp",EDGE,"E537")])],"isStart":false});
            var Q23;
            Q23=makeQuery(id+"F31.opExtrude","CAP_EDGE",EDGE,{"disambiguationData":[OSD([sQuery(id+"F30.wireOp",EDGE,"E372")])],"isStart":false});
            var Q24;
            Q24=makeQuery(id+"F31.opExtrude","CAP_EDGE",EDGE,{"disambiguationData":[OSD([sQuery(id+"F30.wireOp",EDGE,"E373")])],"isStart":false});
            var Q25;
            Q25=makeQuery(id+"F31.opExtrude","CAP_EDGE",EDGE,{"disambiguationData":[OSD([sQuery(id+"F30.wireOp",EDGE,"E374")])],"isStart":false});
            var Q26;
            Q26=makeQuery(id+"F31.opExtrude","CAP_EDGE",EDGE,{"disambiguationData":[OSD([sQuery(id+"F30.wireOp",EDGE,"E536")])],"isStart":false});
            var Q27;
            Q27=makeQuery(id+"F31.opExtrude","CAP_EDGE",EDGE,{"disambiguationData":[OSD([sQuery(id+"F30.wireOp",EDGE,"E376")])],"isStart":false});
            var Q28;
            Q28=makeQuery(id+"F31.opExtrude","CAP_EDGE",EDGE,{"disambiguationData":[OSD([sQuery(id+"F30.wireOp",EDGE,"E535")])],"isStart":false});
            var Q29;
            Q29=makeQuery(id+"F31.opExtrude","CAP_EDGE",EDGE,{"disambiguationData":[OSD([sQuery(id+"F30.wireOp",EDGE,"E378")])],"isStart":false});
            var Q30;
            Q30=makeQuery(id+"F31.opExtrude","CAP_EDGE",EDGE,{"disambiguationData":[OSD([sQuery(id+"F30.wireOp",EDGE,"E534")])],"isStart":false});
            var Q31;
            Q31=makeQuery(id+"F31.opExtrude","CAP_EDGE",EDGE,{"disambiguationData":[OSD([sQuery(id+"F30.wireOp",EDGE,"E380")])],"isStart":false});
            var Q32;
            Q32=makeQuery(id+"F31.opExtrude","CAP_EDGE",EDGE,{"disambiguationData":[OSD([sQuery(id+"F30.wireOp",EDGE,"E533")])],"isStart":false});
            var Q33;
            Q33=makeQuery(id+"F31.opExtrude","CAP_EDGE",EDGE,{"disambiguationData":[OSD([sQuery(id+"F30.wireOp",EDGE,"E382")])],"isStart":false});
            var Q34;
            Q34=makeQuery(id+"F31.opExtrude","CAP_EDGE",EDGE,{"disambiguationData":[OSD([sQuery(id+"F30.wireOp",EDGE,"E383")])],"isStart":false});
            var Q35;
            Q35=makeQuery(id+"F31.opExtrude","CAP_EDGE",EDGE,{"disambiguationData":[OSD([sQuery(id+"F30.wireOp",EDGE,"E384"),sQuery(id+"F30.wireOp",EDGE,"E469")])],"isStart":false});
            var Q36;
            Q36=makeQuery(id+"F31.opExtrude","CAP_EDGE",EDGE,{"disambiguationData":[OSD([sQuery(id+"F30.wireOp",EDGE,"E385")])],"isStart":false});
            var Q37;
            Q37=makeQuery(id+"F31.opExtrude","CAP_EDGE",EDGE,{"disambiguationData":[OSD([sQuery(id+"F30.wireOp",EDGE,"E531")])],"isStart":false});
            var Q38;
            Q38=makeQuery(id+"F31.opExtrude","CAP_EDGE",EDGE,{"disambiguationData":[OSD([sQuery(id+"F30.wireOp",EDGE,"E387")])],"isStart":false});
            var Q39;
            Q39=makeQuery(id+"F31.opExtrude","CAP_EDGE",EDGE,{"disambiguationData":[OSD([sQuery(id+"F30.wireOp",EDGE,"E530")])],"isStart":false});
            var Q40;
            Q40=makeQuery(id+"F31.opExtrude","CAP_EDGE",EDGE,{"disambiguationData":[OSD([sQuery(id+"F30.wireOp",EDGE,"E389")])],"isStart":false});
            var Q41;
            Q41=makeQuery(id+"F31.opExtrude","CAP_EDGE",EDGE,{"disambiguationData":[OSD([sQuery(id+"F30.wireOp",EDGE,"E529")])],"isStart":false});
            var Q42;
            Q42=makeQuery(id+"F31.opExtrude","CAP_EDGE",EDGE,{"disambiguationData":[OSD([sQuery(id+"F30.wireOp",EDGE,"E391")])],"isStart":false});
            var Q43;
            Q43=makeQuery(id+"F31.opExtrude","CAP_EDGE",EDGE,{"disambiguationData":[OSD([sQuery(id+"F30.wireOp",EDGE,"E392")])],"isStart":false});
            var Q44;
            Q44=makeQuery(id+"F31.opExtrude","CAP_EDGE",EDGE,{"disambiguationData":[OSD([sQuery(id+"F30.wireOp",EDGE,"E393")])],"isStart":false});
            var Q45;
            Q45=makeQuery(id+"F31.opExtrude","CAP_EDGE",EDGE,{"disambiguationData":[OSD([sQuery(id+"F30.wireOp",EDGE,"E527")])],"isStart":false});
            var Q46;
            Q46=makeQuery(id+"F31.opExtrude","CAP_EDGE",EDGE,{"disambiguationData":[OSD([sQuery(id+"F30.wireOp",EDGE,"E395")])],"isStart":false});
            var Q47;
            Q47=makeQuery(id+"F31.opExtrude","CAP_EDGE",EDGE,{"disambiguationData":[OSD([sQuery(id+"F30.wireOp",EDGE,"E396")])],"isStart":false});
            var Q48;
            Q48=makeQuery(id+"F31.opExtrude","CAP_EDGE",EDGE,{"disambiguationData":[OSD([sQuery(id+"F30.wireOp",EDGE,"E556")])],"isStart":false});
            var Q49;
            Q49=makeQuery(id+"F31.opExtrude","CAP_EDGE",EDGE,{"disambiguationData":[OSD([sQuery(id+"F30.wireOp",EDGE,"E398")])],"isStart":false});
            var Q50;
            Q50=makeQuery(id+"F31.opExtrude","CAP_EDGE",EDGE,{"disambiguationData":[OSD([sQuery(id+"F30.wireOp",EDGE,"E526")])],"isStart":false});
            var Q51;
            Q51=makeQuery(id+"F31.opExtrude","CAP_EDGE",EDGE,{"disambiguationData":[OSD([sQuery(id+"F30.wireOp",EDGE,"E400")])],"isStart":false});
            var Q52;
            Q52=makeQuery(id+"F31.opExtrude","CAP_EDGE",EDGE,{"disambiguationData":[OSD([sQuery(id+"F30.wireOp",EDGE,"E525")])],"isStart":false});
            var Q53;
            Q53=makeQuery(id+"F31.opExtrude","CAP_EDGE",EDGE,{"disambiguationData":[OSD([sQuery(id+"F30.wireOp",EDGE,"E402")])],"isStart":false});
            var Q54;
            Q54=makeQuery(id+"F31.opExtrude","CAP_EDGE",EDGE,{"disambiguationData":[OSD([sQuery(id+"F30.wireOp",EDGE,"E524")])],"isStart":false});
            var Q55;
            Q55=makeQuery(id+"F31.opExtrude","CAP_EDGE",EDGE,{"disambiguationData":[OSD([sQuery(id+"F30.wireOp",EDGE,"E404")])],"isStart":false});
            var Q56;
            Q56=makeQuery(id+"F31.opExtrude","CAP_EDGE",EDGE,{"disambiguationData":[OSD([sQuery(id+"F30.wireOp",EDGE,"E523")])],"isStart":false});
            var Q57;
            Q57=makeQuery(id+"F31.opExtrude","CAP_EDGE",EDGE,{"disambiguationData":[OSD([sQuery(id+"F30.wireOp",EDGE,"E406")])],"isStart":false});
            var Q58;
            Q58=makeQuery(id+"F31.opExtrude","CAP_EDGE",EDGE,{"disambiguationData":[OSD([sQuery(id+"F30.wireOp",EDGE,"E522")])],"isStart":false});
            var Q59;
            Q59=makeQuery(id+"F31.opExtrude","CAP_EDGE",EDGE,{"disambiguationData":[OSD([sQuery(id+"F30.wireOp",EDGE,"E408")])],"isStart":false});
            var Q60;
            Q60=makeQuery(id+"F31.opExtrude","CAP_EDGE",EDGE,{"disambiguationData":[OSD([sQuery(id+"F30.wireOp",EDGE,"E521")])],"isStart":false});
            var Q61;
            Q61=makeQuery(id+"F31.opExtrude","CAP_EDGE",EDGE,{"disambiguationData":[OSD([sQuery(id+"F30.wireOp",EDGE,"E410")])],"isStart":false});
            var Q62;
            Q62=makeQuery(id+"F31.opExtrude","CAP_EDGE",EDGE,{"disambiguationData":[OSD([sQuery(id+"F30.wireOp",EDGE,"E520")])],"isStart":false});
            var Q63;
            Q63=makeQuery(id+"F31.opExtrude","CAP_EDGE",EDGE,{"disambiguationData":[OSD([sQuery(id+"F30.wireOp",EDGE,"E412")])],"isStart":false});
            var Q64;
            Q64=makeQuery(id+"F31.opExtrude","CAP_EDGE",EDGE,{"disambiguationData":[OSD([sQuery(id+"F30.wireOp",EDGE,"E519")])],"isStart":false});
            var Q65;
            Q65=makeQuery(id+"F31.opExtrude","CAP_EDGE",EDGE,{"disambiguationData":[OSD([sQuery(id+"F30.wireOp",EDGE,"E414"),sQuery(id+"F30.wireOp",EDGE,"E482")])],"isStart":false});
            var Q66;
            Q66=makeQuery(id+"F31.opExtrude","CAP_EDGE",EDGE,{"disambiguationData":[OSD([sQuery(id+"F30.wireOp",EDGE,"E518")])],"isStart":false});
            var Q67;
            Q67=makeQuery(id+"F31.opExtrude","CAP_EDGE",EDGE,{"disambiguationData":[OSD([sQuery(id+"F30.wireOp",EDGE,"E416")])],"isStart":false});
            var Q68;
            Q68=makeQuery(id+"F31.opExtrude","CAP_EDGE",EDGE,{"disambiguationData":[OSD([sQuery(id+"F30.wireOp",EDGE,"E517")])],"isStart":false});
            var Q69;
            Q69=makeQuery(id+"F31.opExtrude","CAP_EDGE",EDGE,{"disambiguationData":[OSD([sQuery(id+"F30.wireOp",EDGE,"E418")])],"isStart":false});
            var Q70;
            Q70=makeQuery(id+"F31.opExtrude","CAP_EDGE",EDGE,{"disambiguationData":[OSD([sQuery(id+"F30.wireOp",EDGE,"E516")])],"isStart":false});
            var Q71;
            Q71=makeQuery(id+"F31.opExtrude","CAP_EDGE",EDGE,{"disambiguationData":[OSD([sQuery(id+"F30.wireOp",EDGE,"E420")])],"isStart":false});
            var Q72;
            Q72=makeQuery(id+"F31.opExtrude","CAP_EDGE",EDGE,{"disambiguationData":[OSD([sQuery(id+"F30.wireOp",EDGE,"E422")])],"isStart":false});
            var Q73;
            Q73=makeQuery(id+"F31.opExtrude","CAP_EDGE",EDGE,{"disambiguationData":[OSD([sQuery(id+"F30.wireOp",EDGE,"E514")])],"isStart":false});
            var Q74;
            Q74=makeQuery(id+"F31.opExtrude","CAP_EDGE",EDGE,{"disambiguationData":[OSD([sQuery(id+"F30.wireOp",EDGE,"E424")])],"isStart":false});
            var Q75;
            Q75=makeQuery(id+"F31.opExtrude","CAP_EDGE",EDGE,{"disambiguationData":[OSD([sQuery(id+"F30.wireOp",EDGE,"E513")])],"isStart":false});
            var Q76;
            Q76=makeQuery(id+"F31.opExtrude","CAP_EDGE",EDGE,{"disambiguationData":[OSD([sQuery(id+"F30.wireOp",EDGE,"E426")])],"isStart":false});
            var Q77;
            Q77=makeQuery(id+"F31.opExtrude","CAP_EDGE",EDGE,{"disambiguationData":[OSD([sQuery(id+"F30.wireOp",EDGE,"E512")])],"isStart":false});
            var Q78;
            Q78=makeQuery(id+"F31.opExtrude","CAP_EDGE",EDGE,{"disambiguationData":[OSD([sQuery(id+"F30.wireOp",EDGE,"E428")])],"isStart":false});
            var Q79;
            Q79=makeQuery(id+"F31.opExtrude","CAP_EDGE",EDGE,{"disambiguationData":[OSD([sQuery(id+"F30.wireOp",EDGE,"E429"),sQuery(id+"F30.wireOp",EDGE,"E489")])],"isStart":false});
            var Q80;
            Q80=makeQuery(id+"F31.opExtrude","CAP_EDGE",EDGE,{"disambiguationData":[OSD([sQuery(id+"F30.wireOp",EDGE,"E430")])],"isStart":false});
            var Q81;
            Q81=makeQuery(id+"F31.opExtrude","CAP_EDGE",EDGE,{"disambiguationData":[OSD([sQuery(id+"F30.wireOp",EDGE,"E510")])],"isStart":false});
            var Q82;
            Q82=makeQuery(id+"F31.opExtrude","CAP_EDGE",EDGE,{"disambiguationData":[OSD([sQuery(id+"F30.wireOp",EDGE,"E432")])],"isStart":false});
            var Q83;
            Q83=makeQuery(id+"F31.opExtrude","CAP_EDGE",EDGE,{"disambiguationData":[OSD([sQuery(id+"F30.wireOp",EDGE,"E509")])],"isStart":false});
            var Q84;
            Q84=makeQuery(id+"F31.opExtrude","CAP_EDGE",EDGE,{"disambiguationData":[OSD([sQuery(id+"F30.wireOp",EDGE,"E491")])],"isStart":false});
            var Q85;
            Q85=makeQuery(id+"F31.opExtrude","CAP_EDGE",EDGE,{"disambiguationData":[OSD([sQuery(id+"F30.wireOp",EDGE,"E434")])],"isStart":false});
            var Q86;
            Q86=makeQuery(id+"F31.opExtrude","CAP_EDGE",EDGE,{"disambiguationData":[OSD([sQuery(id+"F30.wireOp",EDGE,"E508")])],"isStart":false});
            var Q87;
            Q87=makeQuery(id+"F31.opExtrude","CAP_EDGE",EDGE,{"disambiguationData":[OSD([sQuery(id+"F30.wireOp",EDGE,"E436")])],"isStart":false});
            var Q88;
            Q88=makeQuery(id+"F31.opExtrude","CAP_EDGE",EDGE,{"disambiguationData":[OSD([sQuery(id+"F30.wireOp",EDGE,"E437"),sQuery(id+"F30.wireOp",EDGE,"E493")])],"isStart":false});
            var Q89;
            Q89=makeQuery(id+"F31.opExtrude","CAP_EDGE",EDGE,{"disambiguationData":[OSD([sQuery(id+"F30.wireOp",EDGE,"E438")])],"isStart":false});
            var Q90;
            Q90=makeQuery(id+"F31.opExtrude","CAP_EDGE",EDGE,{"disambiguationData":[OSD([sQuery(id+"F30.wireOp",EDGE,"E506")])],"isStart":false});
            var Q91;
            Q91=makeQuery(id+"F31.opExtrude","CAP_EDGE",EDGE,{"disambiguationData":[OSD([sQuery(id+"F30.wireOp",EDGE,"E440")])],"isStart":false});
            var Q92;
            Q92=makeQuery(id+"F31.opExtrude","CAP_EDGE",EDGE,{"disambiguationData":[OSD([sQuery(id+"F30.wireOp",EDGE,"E441")])],"isStart":false});
            var Q93;
            Q93=makeQuery(id+"F31.opExtrude","CAP_EDGE",EDGE,{"disambiguationData":[OSD([sQuery(id+"F30.wireOp",EDGE,"E442"),sQuery(id+"F30.wireOp",EDGE,"E495")])],"isStart":false});
            var Q94;
            Q94=makeQuery(id+"F31.opExtrude","CAP_EDGE",EDGE,{"disambiguationData":[OSD([sQuery(id+"F30.wireOp",EDGE,"E443")])],"isStart":false});
            var Q95;
            Q95=makeQuery(id+"F31.opExtrude","CAP_EDGE",EDGE,{"disambiguationData":[OSD([sQuery(id+"F30.wireOp",EDGE,"E505")])],"isStart":false});
            var Q96;
            Q96=makeQuery(id+"F31.opExtrude","CAP_EDGE",EDGE,{"disambiguationData":[OSD([sQuery(id+"F30.wireOp",EDGE,"E445")])],"isStart":false});
            var Q97;
            Q97=makeQuery(id+"F31.opExtrude","CAP_EDGE",EDGE,{"disambiguationData":[OSD([sQuery(id+"F30.wireOp",EDGE,"E504")])],"isStart":false});
            var Q98;
            Q98=makeQuery(id+"F31.opExtrude","CAP_EDGE",EDGE,{"disambiguationData":[OSD([sQuery(id+"F30.wireOp",EDGE,"E503")])],"isStart":false});
            var Q99;
            Q99=makeQuery(id+"F31.opExtrude","CAP_EDGE",EDGE,{"disambiguationData":[OSD([sQuery(id+"F30.wireOp",EDGE,"E447")])],"isStart":false});
            var Q100;
            Q100=makeQuery(id+"F31.opExtrude","CAP_EDGE",EDGE,{"disambiguationData":[OSD([sQuery(id+"F30.wireOp",EDGE,"E449")])],"isStart":false});
            var Q101;
            Q101=makeQuery(id+"F31.opExtrude","CAP_EDGE",EDGE,{"disambiguationData":[OSD([sQuery(id+"F30.wireOp",EDGE,"E450")])],"isStart":false});
            var Q102;
            Q102=makeQuery(id+"F31.opExtrude","CAP_EDGE",EDGE,{"disambiguationData":[OSD([sQuery(id+"F30.wireOp",EDGE,"E449")])],"isStart":false});
            var Q103;
            Q103=makeQuery(id+"F31.opExtrude","CAP_EDGE",EDGE,{"disambiguationData":[OSD([sQuery(id+"F30.wireOp",EDGE,"E451")])],"isStart":false});
            var Q104;
            Q104=makeQuery(id+"F31.opExtrude","CAP_EDGE",EDGE,{"disambiguationData":[OSD([sQuery(id+"F30.wireOp",EDGE,"E502")])],"isStart":false});
            var Q105;
            Q105=makeQuery(id+"F31.opExtrude","CAP_EDGE",EDGE,{"disambiguationData":[OSD([sQuery(id+"F30.wireOp",EDGE,"E452")])],"isStart":false});
            var Q106;
            Q106=makeQuery(id+"F31.opExtrude","CAP_EDGE",EDGE,{"disambiguationData":[OSD([sQuery(id+"F30.wireOp",EDGE,"E501")])],"isStart":false});
            var Q107;
            Q107=makeQuery(id+"F31.opExtrude","CAP_EDGE",EDGE,{"disambiguationData":[OSD([sQuery(id+"F30.wireOp",EDGE,"E453")])],"isStart":false});
            var Q108;
            Q108=makeQuery(id+"F31.opExtrude","CAP_EDGE",EDGE,{"disambiguationData":[OSD([sQuery(id+"F30.wireOp",EDGE,"E454")])],"isStart":false});
            var Q109;
            Q109=makeQuery(id+"F31.opExtrude","CAP_EDGE",EDGE,{"disambiguationData":[OSD([sQuery(id+"F30.wireOp",EDGE,"E500")])],"isStart":false});
            var Q110;
            Q110=makeQuery(id+"F31.opExtrude","CAP_EDGE",EDGE,{"disambiguationData":[OSD([sQuery(id+"F30.wireOp",EDGE,"E455")])],"isStart":false});
            var Q111;
            Q111=makeQuery(id+"F31.opExtrude","CAP_EDGE",EDGE,{"disambiguationData":[OSD([sQuery(id+"F30.wireOp",EDGE,"E499")])],"isStart":false});
            var Q112;
            Q112=makeQuery(id+"F31.opExtrude","CAP_EDGE",EDGE,{"disambiguationData":[OSD([sQuery(id+"F30.wireOp",EDGE,"E344")])],"isStart":false});
            var Q113;
            Q113=makeQuery(id+"F31.opExtrude","CAP_EDGE",EDGE,{"disambiguationData":[OSD([sQuery(id+"F30.wireOp",EDGE,"E553")])],"isStart":false});
            var Q114;
            Q114=makeQuery(id+"F31.opExtrude","CAP_EDGE",EDGE,{"disambiguationData":[OSD([sQuery(id+"F30.wireOp",EDGE,"E345")])],"isStart":false});
            var Q115;
            Q115=makeQuery(id+"F31.opExtrude","CAP_EDGE",EDGE,{"disambiguationData":[OSD([sQuery(id+"F30.wireOp",EDGE,"E552")])],"isStart":false});
            var Q116;
            Q116=makeQuery(id+"F31.opExtrude","CAP_EDGE",EDGE,{"disambiguationData":[OSD([sQuery(id+"F30.wireOp",EDGE,"E346")])],"isStart":false});
            var Q117;
            Q117=makeQuery(id+"F31.opExtrude","CAP_EDGE",EDGE,{"disambiguationData":[OSD([sQuery(id+"F30.wireOp",EDGE,"E551")])],"isStart":false});
            var Q118;
            Q118=makeQuery(id+"F31.opExtrude","CAP_EDGE",EDGE,{"disambiguationData":[OSD([sQuery(id+"F30.wireOp",EDGE,"E347")])],"isStart":false});
            var Q119;
            Q119=makeQuery(id+"F31.opExtrude","CAP_EDGE",EDGE,{"disambiguationData":[OSD([sQuery(id+"F30.wireOp",EDGE,"E549")])],"isStart":false});
            var Q120;
            Q120=makeQuery(id+"F31.opExtrude","CAP_EDGE",EDGE,{"disambiguationData":[OSD([sQuery(id+"F30.wireOp",EDGE,"E348")])],"isStart":false});
            var Q121;
            Q121=makeQuery(id+"F31.opExtrude","CAP_EDGE",EDGE,{"disambiguationData":[OSD([sQuery(id+"F30.wireOp",EDGE,"E349")])],"isStart":false});
            var Q122;
            Q122=makeQuery(id+"F31.opExtrude","CAP_EDGE",EDGE,{"disambiguationData":[OSD([sQuery(id+"F30.wireOp",EDGE,"E548")])],"isStart":false});
            var Q123;
            Q123=makeQuery(id+"F31.opExtrude","CAP_EDGE",EDGE,{"disambiguationData":[OSD([sQuery(id+"F30.wireOp",EDGE,"E543")])],"isStart":false});
            var Q124;
            Q124=makeQuery(id+"F31.opExtrude","CAP_EDGE",EDGE,{"disambiguationData":[OSD([sQuery(id+"F30.wireOp",EDGE,"E550")])],"isStart":false});
            var Q125;
            Q125=makeQuery(id+"F31.opExtrude","CAP_EDGE",EDGE,{"disambiguationData":[OSD([sQuery(id+"F30.wireOp",EDGE,"E515")])],"isStart":false});
            chamfer(context, id + "F34", {"entities" : qUnion([Q0, Q1, Q2, Q3, Q4, Q5, Q6, Q7, Q8, Q9, Q10, Q11, Q12, Q13, Q14, Q15, Q16, Q17, Q18, Q19, Q20, Q21, Q22, Q23, Q24, Q25, Q26, Q27, Q28, Q29, Q30, Q31, Q32, Q33, Q34, Q35, Q36, Q37, Q38, Q39, Q40, Q41, Q42, Q43, Q44, Q45, Q46, Q47, Q48, Q49, Q50, Q51, Q52, Q53, Q54, Q55, Q56, Q57, Q58, Q59, Q60, Q61, Q62, Q63, Q64, Q65, Q66, Q67, Q68, Q69, Q70, Q71, Q72, Q73, Q74, Q75, Q76, Q77, Q78, Q79, Q80, Q81, Q82, Q83, Q84, Q85, Q86, Q87, Q88, Q89, Q90, Q91, Q92, Q93, Q94, Q95, Q96, Q97, Q98, Q99, Q100, Q101, Q102, Q103, Q104, Q105, Q106, Q107, Q108, Q109, Q110, Q111, Q112, Q113, Q114, Q115, Q116, Q117, Q118, Q119, Q120, Q121, Q122, Q123, Q124, Q125]), "width" : 0.13 * mm, "tangentPropagation" : true});
        }
    });
